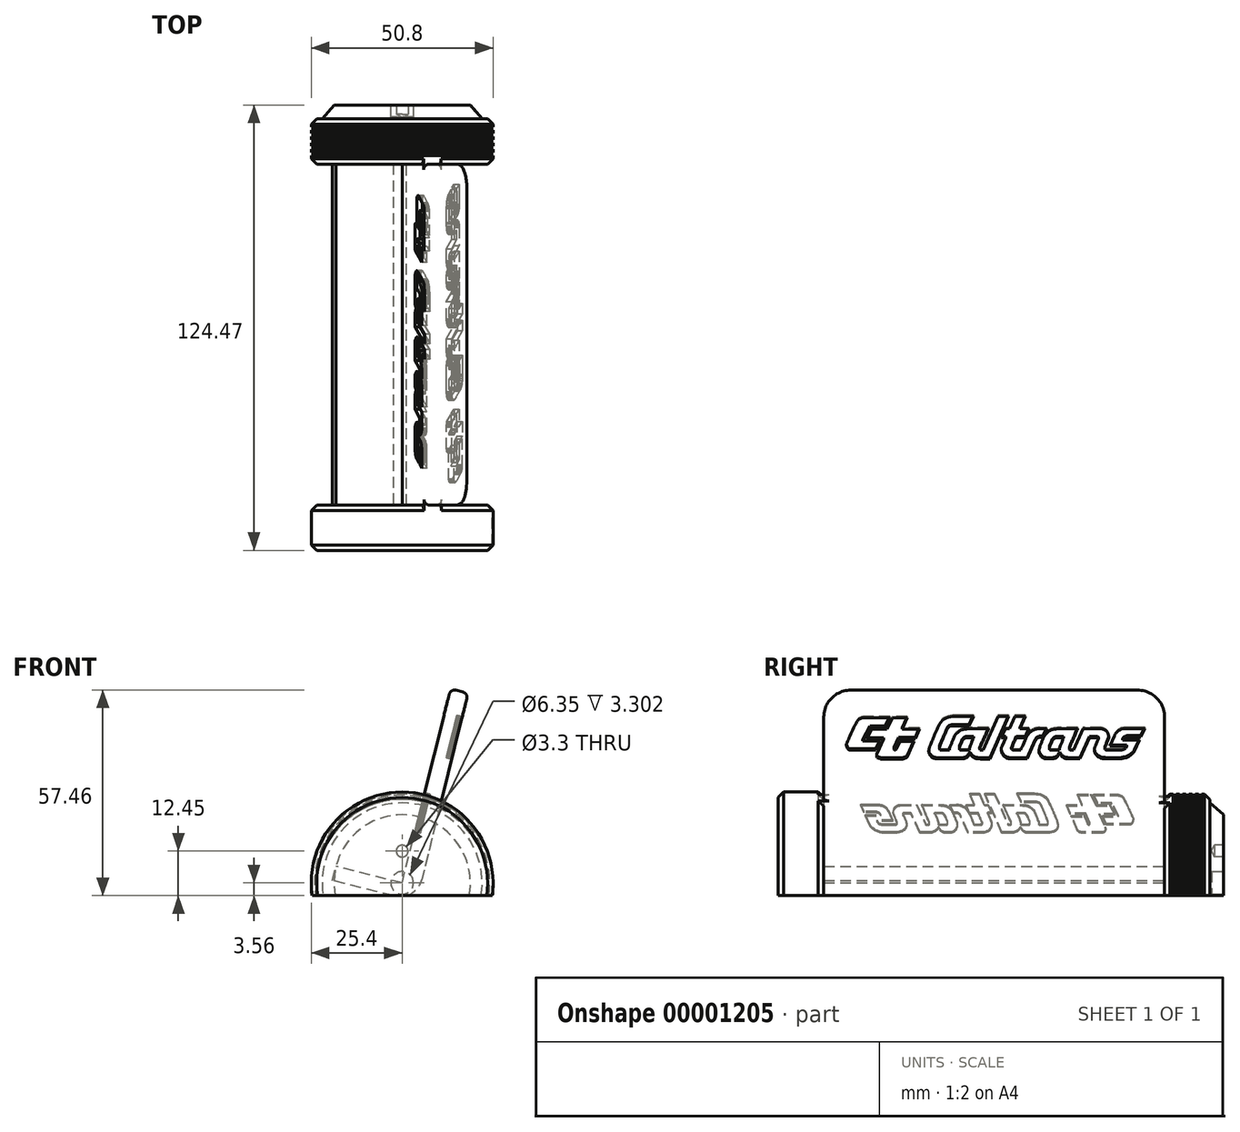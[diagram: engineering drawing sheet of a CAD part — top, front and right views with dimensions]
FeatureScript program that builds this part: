
annotation { "Feature Type Name" : "Feature", "Feature Type Description" : "" }
export const myFeature = defineFeature(function(context is Context, id is Id, definition is map)
    precondition{}
    {
        {
            var Q0;
            Q0=qCreatedBy(makeId("Front.planeOp"),FACE);
            var sketch = newSketch(context, id + "F0", { "sketchPlane" : qUnion([Q0])});
            skLineSegment(sketch, "E0", {"start": v(0, 0) * mm, "end": v(13.52, 54.22) * mm});
            skLineSegment(sketch, "E1", {"start": v(0, 0) * mm, "end": v(-18.48, 4.6) * mm});
            skLineSegment(sketch, "E2", {"start": v(13.52, 54.22) * mm, "end": v(18.45, 53) * mm});
            skLineSegment(sketch, "E3", {"start": v(18.45, 53) * mm, "end": v(3.95, -5.17) * mm});
            skLineSegment(sketch, "E4", {"start": v(3.95, -5.17) * mm, "end": v(-19.47, 0.67) * mm});
            skLineSegment(sketch, "E5", {"start": v(-19.47, 0.67) * mm, "end": v(-18.48, 4.6) * mm});
            skSolve(sketch);
        }
        {
            var Q0;
            Q0 = qSketchRegion(id + "F0", true);
            extrude(context, id + "F1", {"entities" : qUnion([Q0]), "depth" : 95.25 * mm, "offsetDistance" : 25.4 * mm, "symmetric" : true});
        }
        {
            var Q0;
            Q0=makeQuery(id+"F1.opExtrude","CAP_FACE",FACE,{"disambiguationData":[OSD([sQuery(id+"F0.wireOp",EDGE,"E0"),sQuery(id+"F0.wireOp",EDGE,"E1"),sQuery(id+"F0.wireOp",EDGE,"E2"),sQuery(id+"F0.wireOp",EDGE,"E3"),sQuery(id+"F0.wireOp",EDGE,"E4"),sQuery(id+"F0.wireOp",EDGE,"E5")])],"isStart":false});
            var sketch = newSketch(context, id + "F2", { "sketchPlane" : qUnion([Q0])});
            skCircle(sketch, "E6", {"center": v(0, 0) * mm, "radius": 25.4 * mm});
            skSolve(sketch);
        }
        {
            var Q0;
            Q0 = qSketchRegion(id + "F2", true);
            extrude(context, id + "F3", {"entities" : qUnion([Q0]), "operationType" : NewBodyOperationType.ADD, "depth" : 12.7 * mm, "offsetDistance" : 25.4 * mm});
        }
        {
            var Q0;
            Q0=makeQuery(id+"F1.opExtrude","SWEPT_FACE",FACE,{"disambiguationData":[OSD([sQuery(id+"F0.wireOp",EDGE,"E0")])]});
            var sketch = newSketch(context, id + "F4", { "sketchPlane" : qUnion([Q0])});
            skLineSegment(sketch, "E7", {"start": v(-27.75, 25.53) * mm, "end": v(-34.38, 25.53) * mm});
            skLineSegment(sketch, "E8", {"start": v(-34.38, 25.53) * mm, "end": v(-34.43, 25.53) * mm});
            skLineSegment(sketch, "E9", {"start": v(-34.43, 25.53) * mm, "end": v(-34.56, 25.52) * mm});
            skLineSegment(sketch, "E10", {"start": v(-34.56, 25.52) * mm, "end": v(-34.77, 25.48) * mm});
            skLineSegment(sketch, "E11", {"start": v(-34.77, 25.48) * mm, "end": v(-35.02, 25.41) * mm});
            skLineSegment(sketch, "E12", {"start": v(-35.02, 25.41) * mm, "end": v(-35.3, 25.3) * mm});
            skLineSegment(sketch, "E13", {"start": v(-35.3, 25.3) * mm, "end": v(-35.58, 25.15) * mm});
            skLineSegment(sketch, "E14", {"start": v(-35.58, 25.15) * mm, "end": v(-35.85, 24.93) * mm});
            skLineSegment(sketch, "E15", {"start": v(-35.85, 24.93) * mm, "end": v(-36.04, 24.72) * mm});
            skLineSegment(sketch, "E16", {"start": v(-36.04, 24.72) * mm, "end": v(-36.1, 24.64) * mm});
            skLineSegment(sketch, "E17", {"start": v(-36.1, 24.64) * mm, "end": v(-36.12, 24.6) * mm});
            skLineSegment(sketch, "E18", {"start": v(-36.12, 24.6) * mm, "end": v(-36.22, 24.43) * mm});
            skLineSegment(sketch, "E19", {"start": v(-36.22, 24.43) * mm, "end": v(-36.38, 24.14) * mm});
            skLineSegment(sketch, "E20", {"start": v(-36.38, 24.14) * mm, "end": v(-36.56, 23.77) * mm});
            skLineSegment(sketch, "E21", {"start": v(-36.56, 23.77) * mm, "end": v(-36.77, 23.34) * mm});
            skLineSegment(sketch, "E22", {"start": v(-36.77, 23.34) * mm, "end": v(-37, 22.86) * mm});
            skLineSegment(sketch, "E23", {"start": v(-37, 22.86) * mm, "end": v(-37.23, 22.36) * mm});
            skLineSegment(sketch, "E24", {"start": v(-37.23, 22.36) * mm, "end": v(-37.46, 21.84) * mm});
            skLineSegment(sketch, "E25", {"start": v(-37.46, 21.84) * mm, "end": v(-37.7, 21.3) * mm});
            skLineSegment(sketch, "E26", {"start": v(-37.7, 21.3) * mm, "end": v(-37.93, 20.8) * mm});
            skLineSegment(sketch, "E27", {"start": v(-37.93, 20.8) * mm, "end": v(-38.15, 20.3) * mm});
            skLineSegment(sketch, "E28", {"start": v(-38.15, 20.3) * mm, "end": v(-38.35, 19.85) * mm});
            skLineSegment(sketch, "E29", {"start": v(-38.35, 19.85) * mm, "end": v(-38.52, 19.44) * mm});
            skLineSegment(sketch, "E30", {"start": v(-38.52, 19.44) * mm, "end": v(-38.67, 19.1) * mm});
            skLineSegment(sketch, "E31", {"start": v(-38.67, 19.1) * mm, "end": v(-38.78, 18.85) * mm});
            skLineSegment(sketch, "E32", {"start": v(-38.78, 18.85) * mm, "end": v(-38.85, 18.68) * mm});
            skLineSegment(sketch, "E33", {"start": v(-38.85, 18.68) * mm, "end": v(-38.88, 18.62) * mm});
            skLineSegment(sketch, "E34", {"start": v(-38.88, 18.62) * mm, "end": v(-38.88, 18.57) * mm});
            skLineSegment(sketch, "E35", {"start": v(-38.88, 18.57) * mm, "end": v(-38.88, 18.42) * mm});
            skLineSegment(sketch, "E36", {"start": v(-38.88, 18.42) * mm, "end": v(-38.86, 18.21) * mm});
            skLineSegment(sketch, "E37", {"start": v(-38.86, 18.21) * mm, "end": v(-38.81, 17.96) * mm});
            skLineSegment(sketch, "E38", {"start": v(-38.81, 17.96) * mm, "end": v(-38.71, 17.7) * mm});
            skLineSegment(sketch, "E39", {"start": v(-38.71, 17.7) * mm, "end": v(-38.55, 17.43) * mm});
            skLineSegment(sketch, "E40", {"start": v(-38.55, 17.43) * mm, "end": v(-38.31, 17.2) * mm});
            skLineSegment(sketch, "E41", {"start": v(-38.31, 17.2) * mm, "end": v(-38.07, 17.07) * mm});
            skLineSegment(sketch, "E42", {"start": v(-38.07, 17.07) * mm, "end": v(-37.98, 17.05) * mm});
            skLineSegment(sketch, "E43", {"start": v(-37.98, 17.05) * mm, "end": v(-31.35, 17.05) * mm});
            skLineSegment(sketch, "E44", {"start": v(-31.35, 17.05) * mm, "end": v(-30.26, 19.42) * mm});
            skLineSegment(sketch, "E45", {"start": v(-30.26, 19.42) * mm, "end": v(-34.7, 19.42) * mm});
            skLineSegment(sketch, "E46", {"start": v(-34.7, 19.42) * mm, "end": v(-32.84, 23.08) * mm});
            skLineSegment(sketch, "E47", {"start": v(-32.84, 23.08) * mm, "end": v(-28.97, 23.08) * mm});
            skLineSegment(sketch, "E48", {"start": v(-28.97, 23.08) * mm, "end": v(-27.75, 25.53) * mm});
            skLineSegment(sketch, "E49", {"start": v(-28.52, 22.53) * mm, "end": v(-32.34, 22.53) * mm});
            skLineSegment(sketch, "E50", {"start": v(-32.34, 22.53) * mm, "end": v(-33.7, 19.9) * mm});
            skLineSegment(sketch, "E51", {"start": v(-33.7, 19.9) * mm, "end": v(-29.37, 19.9) * mm});
            skLineSegment(sketch, "E52", {"start": v(-29.37, 19.9) * mm, "end": v(-31.03, 16.2) * mm});
            skLineSegment(sketch, "E53", {"start": v(-31.03, 16.2) * mm, "end": v(-31.05, 16.15) * mm});
            skLineSegment(sketch, "E54", {"start": v(-31.05, 16.15) * mm, "end": v(-31.1, 16) * mm});
            skLineSegment(sketch, "E55", {"start": v(-31.1, 16) * mm, "end": v(-31.15, 15.8) * mm});
            skLineSegment(sketch, "E56", {"start": v(-31.15, 15.8) * mm, "end": v(-31.16, 15.55) * mm});
            skLineSegment(sketch, "E57", {"start": v(-31.16, 15.55) * mm, "end": v(-31.1, 15.3) * mm});
            skLineSegment(sketch, "E58", {"start": v(-31.1, 15.3) * mm, "end": v(-30.94, 15.05) * mm});
            skLineSegment(sketch, "E59", {"start": v(-30.94, 15.05) * mm, "end": v(-30.65, 14.84) * mm});
            skLineSegment(sketch, "E60", {"start": v(-30.65, 14.84) * mm, "end": v(-30.32, 14.72) * mm});
            skLineSegment(sketch, "E61", {"start": v(-30.32, 14.72) * mm, "end": v(-30.2, 14.7) * mm});
            skLineSegment(sketch, "E62", {"start": v(-30.2, 14.7) * mm, "end": v(-24.7, 14.7) * mm});
            skLineSegment(sketch, "E63", {"start": v(-24.7, 14.7) * mm, "end": v(-24.68, 14.7) * mm});
            skLineSegment(sketch, "E64", {"start": v(-24.68, 14.7) * mm, "end": v(-24.6, 14.7) * mm});
            skLineSegment(sketch, "E65", {"start": v(-24.6, 14.7) * mm, "end": v(-24.47, 14.7) * mm});
            skLineSegment(sketch, "E66", {"start": v(-24.47, 14.7) * mm, "end": v(-24.3, 14.73) * mm});
            skLineSegment(sketch, "E67", {"start": v(-24.3, 14.73) * mm, "end": v(-24.1, 14.79) * mm});
            skLineSegment(sketch, "E68", {"start": v(-24.1, 14.79) * mm, "end": v(-23.87, 14.88) * mm});
            skLineSegment(sketch, "E69", {"start": v(-23.87, 14.88) * mm, "end": v(-23.62, 15.02) * mm});
            skLineSegment(sketch, "E70", {"start": v(-23.62, 15.02) * mm, "end": v(-23.42, 15.17) * mm});
            skLineSegment(sketch, "E71", {"start": v(-23.42, 15.17) * mm, "end": v(-23.36, 15.23) * mm});
            skLineSegment(sketch, "E72", {"start": v(-23.36, 15.23) * mm, "end": v(-21.58, 19.36) * mm});
            skLineSegment(sketch, "E73", {"start": v(-21.58, 19.36) * mm, "end": v(-25.2, 19.36) * mm});
            skLineSegment(sketch, "E74", {"start": v(-25.2, 19.36) * mm, "end": v(-26.07, 17.34) * mm});
            skLineSegment(sketch, "E75", {"start": v(-26.07, 17.34) * mm, "end": v(-26.1, 17.3) * mm});
            skLineSegment(sketch, "E76", {"start": v(-26.1, 17.3) * mm, "end": v(-26.16, 17.24) * mm});
            skLineSegment(sketch, "E77", {"start": v(-26.16, 17.24) * mm, "end": v(-26.25, 17.16) * mm});
            skLineSegment(sketch, "E78", {"start": v(-26.25, 17.16) * mm, "end": v(-26.35, 17.09) * mm});
            skLineSegment(sketch, "E79", {"start": v(-26.35, 17.09) * mm, "end": v(-26.46, 17.05) * mm});
            skLineSegment(sketch, "E80", {"start": v(-26.46, 17.05) * mm, "end": v(-26.57, 17.06) * mm});
            skLineSegment(sketch, "E81", {"start": v(-26.57, 17.06) * mm, "end": v(-26.66, 17.16) * mm});
            skLineSegment(sketch, "E82", {"start": v(-26.66, 17.16) * mm, "end": v(-26.7, 17.3) * mm});
            skLineSegment(sketch, "E83", {"start": v(-26.7, 17.3) * mm, "end": v(-26.72, 17.36) * mm});
            skLineSegment(sketch, "E84", {"start": v(-26.72, 17.36) * mm, "end": v(-25.56, 20.05) * mm});
            skLineSegment(sketch, "E85", {"start": v(-25.56, 20.05) * mm, "end": v(-21.28, 20.05) * mm});
            skLineSegment(sketch, "E86", {"start": v(-21.28, 20.05) * mm, "end": v(-20.23, 22.53) * mm});
            skLineSegment(sketch, "E87", {"start": v(-20.23, 22.53) * mm, "end": v(-24.56, 22.53) * mm});
            skLineSegment(sketch, "E88", {"start": v(-24.56, 22.53) * mm, "end": v(-23.35, 25.55) * mm});
            skLineSegment(sketch, "E89", {"start": v(-23.35, 25.55) * mm, "end": v(-27.05, 25.55) * mm});
            skLineSegment(sketch, "E90", {"start": v(-27.05, 25.55) * mm, "end": v(-28.52, 22.53) * mm});
            skLineSegment(sketch, "E91", {"start": v(14.7, 20.26) * mm, "end": v(16.64, 20.25) * mm});
            skLineSegment(sketch, "E92", {"start": v(16.64, 20.25) * mm, "end": v(16.59, 20.13) * mm});
            skLineSegment(sketch, "E93", {"start": v(16.59, 20.13) * mm, "end": v(16.42, 19.76) * mm});
            skLineSegment(sketch, "E94", {"start": v(16.42, 19.76) * mm, "end": v(16.19, 19.25) * mm});
            skLineSegment(sketch, "E95", {"start": v(16.19, 19.25) * mm, "end": v(15.97, 18.75) * mm});
            skLineSegment(sketch, "E96", {"start": v(15.97, 18.75) * mm, "end": v(15.77, 18.26) * mm});
            skLineSegment(sketch, "E97", {"start": v(15.77, 18.26) * mm, "end": v(15.62, 17.83) * mm});
            skLineSegment(sketch, "E98", {"start": v(15.62, 17.83) * mm, "end": v(15.51, 17.45) * mm});
            skLineSegment(sketch, "E99", {"start": v(15.51, 17.45) * mm, "end": v(15.48, 17.17) * mm});
            skLineSegment(sketch, "E100", {"start": v(15.48, 17.17) * mm, "end": v(15.51, 17.02) * mm});
            skLineSegment(sketch, "E101", {"start": v(15.51, 17.02) * mm, "end": v(15.54, 16.99) * mm});
            skLineSegment(sketch, "E102", {"start": v(15.54, 16.99) * mm, "end": v(13.29, 16.99) * mm});
            skLineSegment(sketch, "E103", {"start": v(13.29, 16.99) * mm, "end": v(13.27, 16.99) * mm});
            skLineSegment(sketch, "E104", {"start": v(13.27, 16.99) * mm, "end": v(13.2, 17.01) * mm});
            skLineSegment(sketch, "E105", {"start": v(13.2, 17.01) * mm, "end": v(13.13, 17.06) * mm});
            skLineSegment(sketch, "E106", {"start": v(13.13, 17.06) * mm, "end": v(13.08, 17.13) * mm});
            skLineSegment(sketch, "E107", {"start": v(13.08, 17.13) * mm, "end": v(13.04, 17.2) * mm});
            skLineSegment(sketch, "E108", {"start": v(13.04, 17.2) * mm, "end": v(13.01, 17.29) * mm});
            skLineSegment(sketch, "E109", {"start": v(13.01, 17.29) * mm, "end": v(13, 17.35) * mm});
            skLineSegment(sketch, "E110", {"start": v(13, 17.35) * mm, "end": v(13, 17.4) * mm});
            skLineSegment(sketch, "E111", {"start": v(13, 17.4) * mm, "end": v(13.01, 17.42) * mm});
            skLineSegment(sketch, "E112", {"start": v(13.01, 17.42) * mm, "end": v(13.02, 17.42) * mm});
            skLineSegment(sketch, "E113", {"start": v(13.02, 17.42) * mm, "end": v(13.02, 17.51) * mm});
            skLineSegment(sketch, "E114", {"start": v(13.02, 17.51) * mm, "end": v(13.05, 17.78) * mm});
            skLineSegment(sketch, "E115", {"start": v(13.05, 17.78) * mm, "end": v(13.13, 18.09) * mm});
            skLineSegment(sketch, "E116", {"start": v(13.13, 18.09) * mm, "end": v(13.24, 18.38) * mm});
            skLineSegment(sketch, "E117", {"start": v(13.24, 18.38) * mm, "end": v(13.35, 18.63) * mm});
            skLineSegment(sketch, "E118", {"start": v(13.35, 18.63) * mm, "end": v(13.38, 18.7) * mm});
            skLineSegment(sketch, "E119", {"start": v(13.38, 18.7) * mm, "end": v(13.42, 18.8) * mm});
            skLineSegment(sketch, "E120", {"start": v(13.42, 18.8) * mm, "end": v(13.56, 19.18) * mm});
            skLineSegment(sketch, "E121", {"start": v(13.56, 19.18) * mm, "end": v(13.74, 19.54) * mm});
            skLineSegment(sketch, "E122", {"start": v(13.74, 19.54) * mm, "end": v(13.8, 19.62) * mm});
            skLineSegment(sketch, "E123", {"start": v(13.8, 19.62) * mm, "end": v(13.84, 19.68) * mm});
            skLineSegment(sketch, "E124", {"start": v(13.84, 19.68) * mm, "end": v(13.98, 19.86) * mm});
            skLineSegment(sketch, "E125", {"start": v(13.98, 19.86) * mm, "end": v(14.17, 20.06) * mm});
            skLineSegment(sketch, "E126", {"start": v(14.17, 20.06) * mm, "end": v(14.4, 20.2) * mm});
            skLineSegment(sketch, "E127", {"start": v(14.4, 20.2) * mm, "end": v(14.62, 20.26) * mm});
            skLineSegment(sketch, "E128", {"start": v(14.62, 20.26) * mm, "end": v(14.7, 20.26) * mm});
            skLineSegment(sketch, "E129", {"start": v(-8.28, 20.26) * mm, "end": v(-6.34, 20.25) * mm});
            skLineSegment(sketch, "E130", {"start": v(-6.34, 20.25) * mm, "end": v(-6.4, 20.13) * mm});
            skLineSegment(sketch, "E131", {"start": v(-6.4, 20.13) * mm, "end": v(-6.56, 19.76) * mm});
            skLineSegment(sketch, "E132", {"start": v(-6.56, 19.76) * mm, "end": v(-6.79, 19.25) * mm});
            skLineSegment(sketch, "E133", {"start": v(-6.79, 19.25) * mm, "end": v(-7.01, 18.75) * mm});
            skLineSegment(sketch, "E134", {"start": v(-7.01, 18.75) * mm, "end": v(-7.2, 18.26) * mm});
            skLineSegment(sketch, "E135", {"start": v(-7.2, 18.26) * mm, "end": v(-7.36, 17.83) * mm});
            skLineSegment(sketch, "E136", {"start": v(-7.36, 17.83) * mm, "end": v(-7.46, 17.45) * mm});
            skLineSegment(sketch, "E137", {"start": v(-7.46, 17.45) * mm, "end": v(-7.5, 17.17) * mm});
            skLineSegment(sketch, "E138", {"start": v(-7.5, 17.17) * mm, "end": v(-7.47, 17.02) * mm});
            skLineSegment(sketch, "E139", {"start": v(-7.47, 17.02) * mm, "end": v(-7.44, 16.99) * mm});
            skLineSegment(sketch, "E140", {"start": v(-7.44, 16.99) * mm, "end": v(-9.7, 16.99) * mm});
            skLineSegment(sketch, "E141", {"start": v(-9.7, 16.99) * mm, "end": v(-9.71, 16.99) * mm});
            skLineSegment(sketch, "E142", {"start": v(-9.71, 16.99) * mm, "end": v(-9.78, 17.01) * mm});
            skLineSegment(sketch, "E143", {"start": v(-9.78, 17.01) * mm, "end": v(-9.85, 17.06) * mm});
            skLineSegment(sketch, "E144", {"start": v(-9.85, 17.06) * mm, "end": v(-9.9, 17.13) * mm});
            skLineSegment(sketch, "E145", {"start": v(-9.9, 17.13) * mm, "end": v(-9.94, 17.2) * mm});
            skLineSegment(sketch, "E146", {"start": v(-9.94, 17.2) * mm, "end": v(-9.97, 17.29) * mm});
            skLineSegment(sketch, "E147", {"start": v(-9.97, 17.29) * mm, "end": v(-9.98, 17.35) * mm});
            skLineSegment(sketch, "E148", {"start": v(-9.98, 17.35) * mm, "end": v(-9.98, 17.4) * mm});
            skLineSegment(sketch, "E149", {"start": v(-9.98, 17.4) * mm, "end": v(-9.97, 17.42) * mm});
            skLineSegment(sketch, "E150", {"start": v(-9.97, 17.42) * mm, "end": v(-9.96, 17.42) * mm});
            skLineSegment(sketch, "E151", {"start": v(-9.96, 17.42) * mm, "end": v(-9.96, 17.51) * mm});
            skLineSegment(sketch, "E152", {"start": v(-9.96, 17.51) * mm, "end": v(-9.93, 17.78) * mm});
            skLineSegment(sketch, "E153", {"start": v(-9.93, 17.78) * mm, "end": v(-9.85, 18.09) * mm});
            skLineSegment(sketch, "E154", {"start": v(-9.85, 18.09) * mm, "end": v(-9.74, 18.38) * mm});
            skLineSegment(sketch, "E155", {"start": v(-9.74, 18.38) * mm, "end": v(-9.63, 18.63) * mm});
            skLineSegment(sketch, "E156", {"start": v(-9.63, 18.63) * mm, "end": v(-9.6, 18.7) * mm});
            skLineSegment(sketch, "E157", {"start": v(-9.6, 18.7) * mm, "end": v(-9.57, 18.8) * mm});
            skLineSegment(sketch, "E158", {"start": v(-9.57, 18.8) * mm, "end": v(-9.42, 19.18) * mm});
            skLineSegment(sketch, "E159", {"start": v(-9.42, 19.18) * mm, "end": v(-9.24, 19.54) * mm});
            skLineSegment(sketch, "E160", {"start": v(-9.24, 19.54) * mm, "end": v(-9.19, 19.62) * mm});
            skLineSegment(sketch, "E161", {"start": v(-9.19, 19.62) * mm, "end": v(-9.14, 19.68) * mm});
            skLineSegment(sketch, "E162", {"start": v(-9.14, 19.68) * mm, "end": v(-9, 19.86) * mm});
            skLineSegment(sketch, "E163", {"start": v(-9, 19.86) * mm, "end": v(-8.8, 20.06) * mm});
            skLineSegment(sketch, "E164", {"start": v(-8.8, 20.06) * mm, "end": v(-8.57, 20.2) * mm});
            skLineSegment(sketch, "E165", {"start": v(-8.57, 20.2) * mm, "end": v(-8.36, 20.26) * mm});
            skLineSegment(sketch, "E166", {"start": v(-8.36, 20.26) * mm, "end": v(-8.28, 20.26) * mm});
            skLineSegment(sketch, "E167", {"start": v(30.97, 14.72) * mm, "end": v(31.09, 14.72) * mm});
            skLineSegment(sketch, "E168", {"start": v(31.09, 14.72) * mm, "end": v(31.45, 14.75) * mm});
            skLineSegment(sketch, "E169", {"start": v(31.45, 14.75) * mm, "end": v(31.97, 14.85) * mm});
            skLineSegment(sketch, "E170", {"start": v(31.97, 14.85) * mm, "end": v(32.57, 15.05) * mm});
            skLineSegment(sketch, "E171", {"start": v(32.57, 15.05) * mm, "end": v(33.1, 15.29) * mm});
            skLineSegment(sketch, "E172", {"start": v(33.1, 15.29) * mm, "end": v(33.27, 15.38) * mm});
            skLineSegment(sketch, "E173", {"start": v(33.27, 15.38) * mm, "end": v(33.37, 15.43) * mm});
            skLineSegment(sketch, "E174", {"start": v(33.37, 15.43) * mm, "end": v(33.63, 15.6) * mm});
            skLineSegment(sketch, "E175", {"start": v(33.63, 15.6) * mm, "end": v(33.94, 15.83) * mm});
            skLineSegment(sketch, "E176", {"start": v(33.94, 15.83) * mm, "end": v(34.19, 16.07) * mm});
            skLineSegment(sketch, "E177", {"start": v(34.19, 16.07) * mm, "end": v(34.4, 16.3) * mm});
            skLineSegment(sketch, "E178", {"start": v(34.4, 16.3) * mm, "end": v(34.55, 16.51) * mm});
            skLineSegment(sketch, "E179", {"start": v(34.55, 16.51) * mm, "end": v(34.65, 16.68) * mm});
            skLineSegment(sketch, "E180", {"start": v(34.65, 16.68) * mm, "end": v(34.72, 16.8) * mm});
            skLineSegment(sketch, "E181", {"start": v(34.72, 16.8) * mm, "end": v(34.74, 16.83) * mm});
            skLineSegment(sketch, "E182", {"start": v(34.74, 16.83) * mm, "end": v(36, 19.68) * mm});
            skLineSegment(sketch, "E183", {"start": v(36, 19.68) * mm, "end": v(31.64, 19.68) * mm});
            skLineSegment(sketch, "E184", {"start": v(31.64, 19.68) * mm, "end": v(31.63, 19.67) * mm});
            skLineSegment(sketch, "E185", {"start": v(31.63, 19.67) * mm, "end": v(31.61, 19.63) * mm});
            skLineSegment(sketch, "E186", {"start": v(31.61, 19.63) * mm, "end": v(31.6, 19.6) * mm});
            skLineSegment(sketch, "E187", {"start": v(31.6, 19.6) * mm, "end": v(31.58, 19.57) * mm});
            skLineSegment(sketch, "E188", {"start": v(31.58, 19.57) * mm, "end": v(31.58, 19.57) * mm});
            skLineSegment(sketch, "E189", {"start": v(31.58, 19.57) * mm, "end": v(31.6, 19.61) * mm});
            skLineSegment(sketch, "E190", {"start": v(31.6, 19.61) * mm, "end": v(31.66, 19.7) * mm});
            skLineSegment(sketch, "E191", {"start": v(31.66, 19.7) * mm, "end": v(31.73, 19.82) * mm});
            skLineSegment(sketch, "E192", {"start": v(31.73, 19.82) * mm, "end": v(31.75, 19.86) * mm});
            skLineSegment(sketch, "E193", {"start": v(31.75, 19.86) * mm, "end": v(31.78, 19.91) * mm});
            skLineSegment(sketch, "E194", {"start": v(31.78, 19.91) * mm, "end": v(31.89, 20.05) * mm});
            skLineSegment(sketch, "E195", {"start": v(31.89, 20.05) * mm, "end": v(32.05, 20.2) * mm});
            skLineSegment(sketch, "E196", {"start": v(32.05, 20.2) * mm, "end": v(32.22, 20.31) * mm});
            skLineSegment(sketch, "E197", {"start": v(32.22, 20.31) * mm, "end": v(32.4, 20.4) * mm});
            skLineSegment(sketch, "E198", {"start": v(32.4, 20.4) * mm, "end": v(32.56, 20.46) * mm});
            skLineSegment(sketch, "E199", {"start": v(32.56, 20.46) * mm, "end": v(32.69, 20.5) * mm});
            skLineSegment(sketch, "E200", {"start": v(32.69, 20.5) * mm, "end": v(32.78, 20.52) * mm});
            skLineSegment(sketch, "E201", {"start": v(32.78, 20.52) * mm, "end": v(32.8, 20.53) * mm});
            skLineSegment(sketch, "E202", {"start": v(32.8, 20.53) * mm, "end": v(36.37, 20.53) * mm});
            skLineSegment(sketch, "E203", {"start": v(36.37, 20.53) * mm, "end": v(37.32, 22.64) * mm});
            skLineSegment(sketch, "E204", {"start": v(37.32, 22.64) * mm, "end": v(37.27, 22.64) * mm});
            skLineSegment(sketch, "E205", {"start": v(37.27, 22.64) * mm, "end": v(37.11, 22.64) * mm});
            skLineSegment(sketch, "E206", {"start": v(37.11, 22.64) * mm, "end": v(36.88, 22.64) * mm});
            skLineSegment(sketch, "E207", {"start": v(36.88, 22.64) * mm, "end": v(36.57, 22.64) * mm});
            skLineSegment(sketch, "E208", {"start": v(36.57, 22.64) * mm, "end": v(36.2, 22.64) * mm});
            skLineSegment(sketch, "E209", {"start": v(36.2, 22.64) * mm, "end": v(35.8, 22.64) * mm});
            skLineSegment(sketch, "E210", {"start": v(35.8, 22.64) * mm, "end": v(35.36, 22.64) * mm});
            skLineSegment(sketch, "E211", {"start": v(35.36, 22.64) * mm, "end": v(34.9, 22.64) * mm});
            skLineSegment(sketch, "E212", {"start": v(34.9, 22.64) * mm, "end": v(34.44, 22.64) * mm});
            skLineSegment(sketch, "E213", {"start": v(34.44, 22.64) * mm, "end": v(33.98, 22.64) * mm});
            skLineSegment(sketch, "E214", {"start": v(33.98, 22.64) * mm, "end": v(33.55, 22.64) * mm});
            skLineSegment(sketch, "E215", {"start": v(33.55, 22.64) * mm, "end": v(33.15, 22.64) * mm});
            skLineSegment(sketch, "E216", {"start": v(33.15, 22.64) * mm, "end": v(32.8, 22.64) * mm});
            skLineSegment(sketch, "E217", {"start": v(32.8, 22.64) * mm, "end": v(32.5, 22.64) * mm});
            skLineSegment(sketch, "E218", {"start": v(32.5, 22.64) * mm, "end": v(32.3, 22.64) * mm});
            skLineSegment(sketch, "E219", {"start": v(32.3, 22.64) * mm, "end": v(32.2, 22.64) * mm});
            skLineSegment(sketch, "E220", {"start": v(32.2, 22.64) * mm, "end": v(32.17, 22.64) * mm});
            skLineSegment(sketch, "E221", {"start": v(32.17, 22.64) * mm, "end": v(32.07, 22.65) * mm});
            skLineSegment(sketch, "E222", {"start": v(32.07, 22.65) * mm, "end": v(31.8, 22.61) * mm});
            skLineSegment(sketch, "E223", {"start": v(31.8, 22.61) * mm, "end": v(31.36, 22.5) * mm});
            skLineSegment(sketch, "E224", {"start": v(31.36, 22.5) * mm, "end": v(30.94, 22.34) * mm});
            skLineSegment(sketch, "E225", {"start": v(30.94, 22.34) * mm, "end": v(30.68, 22.2) * mm});
            skLineSegment(sketch, "E226", {"start": v(30.68, 22.2) * mm, "end": v(30.6, 22.13) * mm});
            skLineSegment(sketch, "E227", {"start": v(30.6, 22.13) * mm, "end": v(30.53, 22.06) * mm});
            skLineSegment(sketch, "E228", {"start": v(30.53, 22.06) * mm, "end": v(30.31, 21.86) * mm});
            skLineSegment(sketch, "E229", {"start": v(30.31, 21.86) * mm, "end": v(30.08, 21.6) * mm});
            skLineSegment(sketch, "E230", {"start": v(30.08, 21.6) * mm, "end": v(29.9, 21.38) * mm});
            skLineSegment(sketch, "E231", {"start": v(29.9, 21.38) * mm, "end": v(29.76, 21.18) * mm});
            skLineSegment(sketch, "E232", {"start": v(29.76, 21.18) * mm, "end": v(29.67, 21.03) * mm});
            skLineSegment(sketch, "E233", {"start": v(29.67, 21.03) * mm, "end": v(29.6, 20.9) * mm});
            skLineSegment(sketch, "E234", {"start": v(29.6, 20.9) * mm, "end": v(29.58, 20.83) * mm});
            skLineSegment(sketch, "E235", {"start": v(29.58, 20.83) * mm, "end": v(29.57, 20.8) * mm});
            skLineSegment(sketch, "E236", {"start": v(29.57, 20.8) * mm, "end": v(28.42, 18.07) * mm});
            skLineSegment(sketch, "E237", {"start": v(28.42, 18.07) * mm, "end": v(32.74, 18.07) * mm});
            skLineSegment(sketch, "E238", {"start": v(32.74, 18.07) * mm, "end": v(32.73, 18.04) * mm});
            skLineSegment(sketch, "E239", {"start": v(32.73, 18.04) * mm, "end": v(32.71, 17.97) * mm});
            skLineSegment(sketch, "E240", {"start": v(32.71, 17.97) * mm, "end": v(32.69, 17.9) * mm});
            skLineSegment(sketch, "E241", {"start": v(32.69, 17.9) * mm, "end": v(32.67, 17.85) * mm});
            skLineSegment(sketch, "E242", {"start": v(32.67, 17.85) * mm, "end": v(32.67, 17.84) * mm});
            skLineSegment(sketch, "E243", {"start": v(32.67, 17.84) * mm, "end": v(32.63, 17.77) * mm});
            skLineSegment(sketch, "E244", {"start": v(32.63, 17.77) * mm, "end": v(32.49, 17.57) * mm});
            skLineSegment(sketch, "E245", {"start": v(32.49, 17.57) * mm, "end": v(32.26, 17.36) * mm});
            skLineSegment(sketch, "E246", {"start": v(32.26, 17.36) * mm, "end": v(32, 17.22) * mm});
            skLineSegment(sketch, "E247", {"start": v(32, 17.22) * mm, "end": v(31.75, 17.13) * mm});
            skLineSegment(sketch, "E248", {"start": v(31.75, 17.13) * mm, "end": v(31.51, 17.07) * mm});
            skLineSegment(sketch, "E249", {"start": v(31.51, 17.07) * mm, "end": v(31.32, 17.05) * mm});
            skLineSegment(sketch, "E250", {"start": v(31.32, 17.05) * mm, "end": v(31.18, 17.04) * mm});
            skLineSegment(sketch, "E251", {"start": v(31.18, 17.04) * mm, "end": v(31.13, 17.04) * mm});
            skLineSegment(sketch, "E252", {"start": v(31.13, 17.04) * mm, "end": v(31, 17.04) * mm});
            skLineSegment(sketch, "E253", {"start": v(31, 17.04) * mm, "end": v(30.65, 17.03) * mm});
            skLineSegment(sketch, "E254", {"start": v(30.65, 17.03) * mm, "end": v(30.14, 17.03) * mm});
            skLineSegment(sketch, "E255", {"start": v(30.14, 17.03) * mm, "end": v(29.54, 17.03) * mm});
            skLineSegment(sketch, "E256", {"start": v(29.54, 17.03) * mm, "end": v(28.92, 17.03) * mm});
            skLineSegment(sketch, "E257", {"start": v(28.92, 17.03) * mm, "end": v(28.34, 17.03) * mm});
            skLineSegment(sketch, "E258", {"start": v(28.34, 17.03) * mm, "end": v(27.87, 17.03) * mm});
            skLineSegment(sketch, "E259", {"start": v(27.87, 17.03) * mm, "end": v(27.65, 17.03) * mm});
            skLineSegment(sketch, "E260", {"start": v(27.65, 17.03) * mm, "end": v(27.57, 17.04) * mm});
            skLineSegment(sketch, "E261", {"start": v(27.57, 17.04) * mm, "end": v(27.53, 17.04) * mm});
            skLineSegment(sketch, "E262", {"start": v(27.53, 17.04) * mm, "end": v(27.4, 17.07) * mm});
            skLineSegment(sketch, "E263", {"start": v(27.4, 17.07) * mm, "end": v(27.28, 17.13) * mm});
            skLineSegment(sketch, "E264", {"start": v(27.28, 17.13) * mm, "end": v(27.2, 17.22) * mm});
            skLineSegment(sketch, "E265", {"start": v(27.2, 17.22) * mm, "end": v(27.16, 17.33) * mm});
            skLineSegment(sketch, "E266", {"start": v(27.16, 17.33) * mm, "end": v(27.15, 17.46) * mm});
            skLineSegment(sketch, "E267", {"start": v(27.15, 17.46) * mm, "end": v(27.16, 17.59) * mm});
            skLineSegment(sketch, "E268", {"start": v(27.16, 17.59) * mm, "end": v(27.18, 17.72) * mm});
            skLineSegment(sketch, "E269", {"start": v(27.18, 17.72) * mm, "end": v(27.21, 17.81) * mm});
            skLineSegment(sketch, "E270", {"start": v(27.21, 17.81) * mm, "end": v(27.23, 17.84) * mm});
            skLineSegment(sketch, "E271", {"start": v(27.23, 17.84) * mm, "end": v(27.28, 17.99) * mm});
            skLineSegment(sketch, "E272", {"start": v(27.28, 17.99) * mm, "end": v(27.46, 18.4) * mm});
            skLineSegment(sketch, "E273", {"start": v(27.46, 18.4) * mm, "end": v(27.67, 18.91) * mm});
            skLineSegment(sketch, "E274", {"start": v(27.67, 18.91) * mm, "end": v(27.87, 19.39) * mm});
            skLineSegment(sketch, "E275", {"start": v(27.87, 19.39) * mm, "end": v(28.03, 19.76) * mm});
            skLineSegment(sketch, "E276", {"start": v(28.03, 19.76) * mm, "end": v(28.07, 19.89) * mm});
            skLineSegment(sketch, "E277", {"start": v(28.07, 19.89) * mm, "end": v(28.12, 20) * mm});
            skLineSegment(sketch, "E278", {"start": v(28.12, 20) * mm, "end": v(28.19, 20.4) * mm});
            skLineSegment(sketch, "E279", {"start": v(28.19, 20.4) * mm, "end": v(28.14, 20.9) * mm});
            skLineSegment(sketch, "E280", {"start": v(28.14, 20.9) * mm, "end": v(27.94, 21.4) * mm});
            skLineSegment(sketch, "E281", {"start": v(27.94, 21.4) * mm, "end": v(27.7, 21.79) * mm});
            skLineSegment(sketch, "E282", {"start": v(27.7, 21.79) * mm, "end": v(27.61, 21.9) * mm});
            skLineSegment(sketch, "E283", {"start": v(27.61, 21.9) * mm, "end": v(27.57, 21.97) * mm});
            skLineSegment(sketch, "E284", {"start": v(27.57, 21.97) * mm, "end": v(27.4, 22.14) * mm});
            skLineSegment(sketch, "E285", {"start": v(27.4, 22.14) * mm, "end": v(27.18, 22.31) * mm});
            skLineSegment(sketch, "E286", {"start": v(27.18, 22.31) * mm, "end": v(26.95, 22.44) * mm});
            skLineSegment(sketch, "E287", {"start": v(26.95, 22.44) * mm, "end": v(26.72, 22.53) * mm});
            skLineSegment(sketch, "E288", {"start": v(26.72, 22.53) * mm, "end": v(26.52, 22.58) * mm});
            skLineSegment(sketch, "E289", {"start": v(26.52, 22.58) * mm, "end": v(26.36, 22.6) * mm});
            skLineSegment(sketch, "E290", {"start": v(26.36, 22.6) * mm, "end": v(26.25, 22.62) * mm});
            skLineSegment(sketch, "E291", {"start": v(26.25, 22.62) * mm, "end": v(26.21, 22.62) * mm});
            skLineSegment(sketch, "E292", {"start": v(26.21, 22.62) * mm, "end": v(21.62, 22.62) * mm});
            skLineSegment(sketch, "E293", {"start": v(21.62, 22.62) * mm, "end": v(19.11, 17) * mm});
            skLineSegment(sketch, "E294", {"start": v(19.11, 17) * mm, "end": v(19.09, 17) * mm});
            skLineSegment(sketch, "E295", {"start": v(19.09, 17) * mm, "end": v(19, 17) * mm});
            skLineSegment(sketch, "E296", {"start": v(19, 17) * mm, "end": v(18.8, 17) * mm});
            skLineSegment(sketch, "E297", {"start": v(18.8, 17) * mm, "end": v(18.57, 17) * mm});
            skLineSegment(sketch, "E298", {"start": v(18.57, 17) * mm, "end": v(18.5, 17) * mm});
            skLineSegment(sketch, "E299", {"start": v(18.5, 17) * mm, "end": v(18.45, 17) * mm});
            skLineSegment(sketch, "E300", {"start": v(18.45, 17) * mm, "end": v(18.33, 17.02) * mm});
            skLineSegment(sketch, "E301", {"start": v(18.33, 17.02) * mm, "end": v(18.21, 17.08) * mm});
            skLineSegment(sketch, "E302", {"start": v(18.21, 17.08) * mm, "end": v(18.14, 17.17) * mm});
            skLineSegment(sketch, "E303", {"start": v(18.14, 17.17) * mm, "end": v(18.1, 17.28) * mm});
            skLineSegment(sketch, "E304", {"start": v(18.1, 17.28) * mm, "end": v(18.1, 17.4) * mm});
            skLineSegment(sketch, "E305", {"start": v(18.1, 17.4) * mm, "end": v(18.12, 17.54) * mm});
            skLineSegment(sketch, "E306", {"start": v(18.12, 17.54) * mm, "end": v(18.15, 17.67) * mm});
            skLineSegment(sketch, "E307", {"start": v(18.15, 17.67) * mm, "end": v(18.18, 17.77) * mm});
            skLineSegment(sketch, "E308", {"start": v(18.18, 17.77) * mm, "end": v(18.2, 17.8) * mm});
            skLineSegment(sketch, "E309", {"start": v(18.2, 17.8) * mm, "end": v(18.23, 17.89) * mm});
            skLineSegment(sketch, "E310", {"start": v(18.23, 17.89) * mm, "end": v(18.35, 18.16) * mm});
            skLineSegment(sketch, "E311", {"start": v(18.35, 18.16) * mm, "end": v(18.5, 18.54) * mm});
            skLineSegment(sketch, "E312", {"start": v(18.5, 18.54) * mm, "end": v(18.68, 18.94) * mm});
            skLineSegment(sketch, "E313", {"start": v(18.68, 18.94) * mm, "end": v(18.84, 19.34) * mm});
            skLineSegment(sketch, "E314", {"start": v(18.84, 19.34) * mm, "end": v(19.01, 19.75) * mm});
            skLineSegment(sketch, "E315", {"start": v(19.01, 19.75) * mm, "end": v(19.18, 20.15) * mm});
            skLineSegment(sketch, "E316", {"start": v(19.18, 20.15) * mm, "end": v(19.34, 20.54) * mm});
            skLineSegment(sketch, "E317", {"start": v(19.34, 20.54) * mm, "end": v(19.5, 20.91) * mm});
            skLineSegment(sketch, "E318", {"start": v(19.5, 20.91) * mm, "end": v(19.64, 21.26) * mm});
            skLineSegment(sketch, "E319", {"start": v(19.64, 21.26) * mm, "end": v(19.77, 21.59) * mm});
            skLineSegment(sketch, "E320", {"start": v(19.77, 21.59) * mm, "end": v(19.9, 21.88) * mm});
            skLineSegment(sketch, "E321", {"start": v(19.9, 21.88) * mm, "end": v(20, 22.13) * mm});
            skLineSegment(sketch, "E322", {"start": v(20, 22.13) * mm, "end": v(20.08, 22.34) * mm});
            skLineSegment(sketch, "E323", {"start": v(20.08, 22.34) * mm, "end": v(20.14, 22.5) * mm});
            skLineSegment(sketch, "E324", {"start": v(20.14, 22.5) * mm, "end": v(20.18, 22.59) * mm});
            skLineSegment(sketch, "E325", {"start": v(20.18, 22.59) * mm, "end": v(20.2, 22.62) * mm});
            skLineSegment(sketch, "E326", {"start": v(20.2, 22.62) * mm, "end": v(15.12, 22.62) * mm});
            skLineSegment(sketch, "E327", {"start": v(15.12, 22.62) * mm, "end": v(15.06, 22.62) * mm});
            skLineSegment(sketch, "E328", {"start": v(15.06, 22.62) * mm, "end": v(14.9, 22.61) * mm});
            skLineSegment(sketch, "E329", {"start": v(14.9, 22.61) * mm, "end": v(14.69, 22.6) * mm});
            skLineSegment(sketch, "E330", {"start": v(14.69, 22.6) * mm, "end": v(14.42, 22.56) * mm});
            skLineSegment(sketch, "E331", {"start": v(14.42, 22.56) * mm, "end": v(14.13, 22.52) * mm});
            skLineSegment(sketch, "E332", {"start": v(14.13, 22.52) * mm, "end": v(13.83, 22.46) * mm});
            skLineSegment(sketch, "E333", {"start": v(13.83, 22.46) * mm, "end": v(13.57, 22.38) * mm});
            skLineSegment(sketch, "E334", {"start": v(13.57, 22.38) * mm, "end": v(13.4, 22.3) * mm});
            skLineSegment(sketch, "E335", {"start": v(13.4, 22.3) * mm, "end": v(13.35, 22.28) * mm});
            skLineSegment(sketch, "E336", {"start": v(13.35, 22.28) * mm, "end": v(13.3, 22.25) * mm});
            skLineSegment(sketch, "E337", {"start": v(13.3, 22.25) * mm, "end": v(13.14, 22.15) * mm});
            skLineSegment(sketch, "E338", {"start": v(13.14, 22.15) * mm, "end": v(12.92, 22.01) * mm});
            skLineSegment(sketch, "E339", {"start": v(12.92, 22.01) * mm, "end": v(12.68, 21.84) * mm});
            skLineSegment(sketch, "E340", {"start": v(12.68, 21.84) * mm, "end": v(12.42, 21.63) * mm});
            skLineSegment(sketch, "E341", {"start": v(12.42, 21.63) * mm, "end": v(12.17, 21.37) * mm});
            skLineSegment(sketch, "E342", {"start": v(12.17, 21.37) * mm, "end": v(11.92, 21.06) * mm});
            skLineSegment(sketch, "E343", {"start": v(11.92, 21.06) * mm, "end": v(11.68, 20.7) * mm});
            skLineSegment(sketch, "E344", {"start": v(11.68, 20.7) * mm, "end": v(11.51, 20.37) * mm});
            skLineSegment(sketch, "E345", {"start": v(11.51, 20.37) * mm, "end": v(11.46, 20.25) * mm});
            skLineSegment(sketch, "E346", {"start": v(11.46, 20.25) * mm, "end": v(11.42, 20.15) * mm});
            skLineSegment(sketch, "E347", {"start": v(11.42, 20.15) * mm, "end": v(11.29, 19.84) * mm});
            skLineSegment(sketch, "E348", {"start": v(11.29, 19.84) * mm, "end": v(11.16, 19.52) * mm});
            skLineSegment(sketch, "E349", {"start": v(11.16, 19.52) * mm, "end": v(11.06, 19.26) * mm});
            skLineSegment(sketch, "E350", {"start": v(11.06, 19.26) * mm, "end": v(10.99, 19.05) * mm});
            skLineSegment(sketch, "E351", {"start": v(10.99, 19.05) * mm, "end": v(10.91, 18.85) * mm});
            skLineSegment(sketch, "E352", {"start": v(10.91, 18.85) * mm, "end": v(10.82, 18.62) * mm});
            skLineSegment(sketch, "E353", {"start": v(10.82, 18.62) * mm, "end": v(10.7, 18.35) * mm});
            skLineSegment(sketch, "E354", {"start": v(10.7, 18.35) * mm, "end": v(10.6, 18.09) * mm});
            skLineSegment(sketch, "E355", {"start": v(10.6, 18.09) * mm, "end": v(10.55, 18) * mm});
            skLineSegment(sketch, "E356", {"start": v(10.55, 18) * mm, "end": v(10.5, 17.89) * mm});
            skLineSegment(sketch, "E357", {"start": v(10.5, 17.89) * mm, "end": v(10.4, 17.52) * mm});
            skLineSegment(sketch, "E358", {"start": v(10.4, 17.52) * mm, "end": v(10.33, 17) * mm});
            skLineSegment(sketch, "E359", {"start": v(10.33, 17) * mm, "end": v(10.36, 16.47) * mm});
            skLineSegment(sketch, "E360", {"start": v(10.36, 16.47) * mm, "end": v(10.47, 16.09) * mm});
            skLineSegment(sketch, "E361", {"start": v(10.47, 16.09) * mm, "end": v(10.52, 15.97) * mm});
            skLineSegment(sketch, "E362", {"start": v(10.52, 15.97) * mm, "end": v(10.55, 15.91) * mm});
            skLineSegment(sketch, "E363", {"start": v(10.55, 15.91) * mm, "end": v(10.64, 15.74) * mm});
            skLineSegment(sketch, "E364", {"start": v(10.64, 15.74) * mm, "end": v(10.77, 15.5) * mm});
            skLineSegment(sketch, "E365", {"start": v(10.77, 15.5) * mm, "end": v(10.92, 15.3) * mm});
            skLineSegment(sketch, "E366", {"start": v(10.92, 15.3) * mm, "end": v(11.1, 15.11) * mm});
            skLineSegment(sketch, "E367", {"start": v(11.1, 15.11) * mm, "end": v(11.34, 14.95) * mm});
            skLineSegment(sketch, "E368", {"start": v(11.34, 14.95) * mm, "end": v(11.62, 14.83) * mm});
            skLineSegment(sketch, "E369", {"start": v(11.62, 14.83) * mm, "end": v(11.96, 14.75) * mm});
            skLineSegment(sketch, "E370", {"start": v(11.96, 14.75) * mm, "end": v(12.28, 14.72) * mm});
            skLineSegment(sketch, "E371", {"start": v(12.28, 14.72) * mm, "end": v(12.38, 14.72) * mm});
            skLineSegment(sketch, "E372", {"start": v(12.38, 14.72) * mm, "end": v(12.57, 14.72) * mm});
            skLineSegment(sketch, "E373", {"start": v(12.57, 14.72) * mm, "end": v(13.14, 14.72) * mm});
            skLineSegment(sketch, "E374", {"start": v(13.14, 14.72) * mm, "end": v(13.61, 14.72) * mm});
            skLineSegment(sketch, "E375", {"start": v(13.61, 14.72) * mm, "end": v(13.85, 14.72) * mm});
            skLineSegment(sketch, "E376", {"start": v(13.85, 14.72) * mm, "end": v(13.92, 14.72) * mm});
            skLineSegment(sketch, "E377", {"start": v(13.92, 14.72) * mm, "end": v(13.95, 14.72) * mm});
            skLineSegment(sketch, "E378", {"start": v(13.95, 14.72) * mm, "end": v(14.04, 14.74) * mm});
            skLineSegment(sketch, "E379", {"start": v(14.04, 14.74) * mm, "end": v(14.17, 14.78) * mm});
            skLineSegment(sketch, "E380", {"start": v(14.17, 14.78) * mm, "end": v(14.33, 14.83) * mm});
            skLineSegment(sketch, "E381", {"start": v(14.33, 14.83) * mm, "end": v(14.51, 14.91) * mm});
            skLineSegment(sketch, "E382", {"start": v(14.51, 14.91) * mm, "end": v(14.7, 15.02) * mm});
            skLineSegment(sketch, "E383", {"start": v(14.7, 15.02) * mm, "end": v(14.87, 15.16) * mm});
            skLineSegment(sketch, "E384", {"start": v(14.87, 15.16) * mm, "end": v(15, 15.3) * mm});
            skLineSegment(sketch, "E385", {"start": v(15, 15.3) * mm, "end": v(15.03, 15.34) * mm});
            skLineSegment(sketch, "E386", {"start": v(15.03, 15.34) * mm, "end": v(15.09, 15.43) * mm});
            skLineSegment(sketch, "E387", {"start": v(15.09, 15.43) * mm, "end": v(15.28, 15.7) * mm});
            skLineSegment(sketch, "E388", {"start": v(15.28, 15.7) * mm, "end": v(15.46, 15.96) * mm});
            skLineSegment(sketch, "E389", {"start": v(15.46, 15.96) * mm, "end": v(15.58, 16.13) * mm});
            skLineSegment(sketch, "E390", {"start": v(15.58, 16.13) * mm, "end": v(15.62, 16.19) * mm});
            skLineSegment(sketch, "E391", {"start": v(15.62, 16.19) * mm, "end": v(15.63, 16.16) * mm});
            skLineSegment(sketch, "E392", {"start": v(15.63, 16.16) * mm, "end": v(15.67, 16.08) * mm});
            skLineSegment(sketch, "E393", {"start": v(15.67, 16.08) * mm, "end": v(15.73, 15.96) * mm});
            skLineSegment(sketch, "E394", {"start": v(15.73, 15.96) * mm, "end": v(15.81, 15.8) * mm});
            skLineSegment(sketch, "E395", {"start": v(15.81, 15.8) * mm, "end": v(15.93, 15.64) * mm});
            skLineSegment(sketch, "E396", {"start": v(15.93, 15.64) * mm, "end": v(16.08, 15.47) * mm});
            skLineSegment(sketch, "E397", {"start": v(16.08, 15.47) * mm, "end": v(16.26, 15.3) * mm});
            skLineSegment(sketch, "E398", {"start": v(16.26, 15.3) * mm, "end": v(16.42, 15.18) * mm});
            skLineSegment(sketch, "E399", {"start": v(16.42, 15.18) * mm, "end": v(16.48, 15.15) * mm});
            skLineSegment(sketch, "E400", {"start": v(16.48, 15.15) * mm, "end": v(16.58, 15.09) * mm});
            skLineSegment(sketch, "E401", {"start": v(16.58, 15.09) * mm, "end": v(16.88, 14.92) * mm});
            skLineSegment(sketch, "E402", {"start": v(16.88, 14.92) * mm, "end": v(17.2, 14.8) * mm});
            skLineSegment(sketch, "E403", {"start": v(17.2, 14.8) * mm, "end": v(17.5, 14.74) * mm});
            skLineSegment(sketch, "E404", {"start": v(17.5, 14.74) * mm, "end": v(17.75, 14.72) * mm});
            skLineSegment(sketch, "E405", {"start": v(17.75, 14.72) * mm, "end": v(17.83, 14.72) * mm});
            skLineSegment(sketch, "E406", {"start": v(17.83, 14.72) * mm, "end": v(17.9, 14.72) * mm});
            skLineSegment(sketch, "E407", {"start": v(17.9, 14.72) * mm, "end": v(18.1, 14.72) * mm});
            skLineSegment(sketch, "E408", {"start": v(18.1, 14.72) * mm, "end": v(18.5, 14.72) * mm});
            skLineSegment(sketch, "E409", {"start": v(18.5, 14.72) * mm, "end": v(18.98, 14.72) * mm});
            skLineSegment(sketch, "E410", {"start": v(18.98, 14.72) * mm, "end": v(19.5, 14.72) * mm});
            skLineSegment(sketch, "E411", {"start": v(19.5, 14.72) * mm, "end": v(19.98, 14.72) * mm});
            skLineSegment(sketch, "E412", {"start": v(19.98, 14.72) * mm, "end": v(20.4, 14.72) * mm});
            skLineSegment(sketch, "E413", {"start": v(20.4, 14.72) * mm, "end": v(20.68, 14.72) * mm});
            skLineSegment(sketch, "E414", {"start": v(20.68, 14.72) * mm, "end": v(20.8, 14.72) * mm});
            skLineSegment(sketch, "E415", {"start": v(20.8, 14.72) * mm, "end": v(23.23, 20.26) * mm});
            skLineSegment(sketch, "E416", {"start": v(23.23, 20.26) * mm, "end": v(25.27, 20.26) * mm});
            skLineSegment(sketch, "E417", {"start": v(25.27, 20.26) * mm, "end": v(25.29, 20.25) * mm});
            skLineSegment(sketch, "E418", {"start": v(25.29, 20.25) * mm, "end": v(25.32, 20.24) * mm});
            skLineSegment(sketch, "E419", {"start": v(25.32, 20.24) * mm, "end": v(25.37, 20.22) * mm});
            skLineSegment(sketch, "E420", {"start": v(25.37, 20.22) * mm, "end": v(25.42, 20.18) * mm});
            skLineSegment(sketch, "E421", {"start": v(25.42, 20.18) * mm, "end": v(25.46, 20.12) * mm});
            skLineSegment(sketch, "E422", {"start": v(25.46, 20.12) * mm, "end": v(25.48, 20.04) * mm});
            skLineSegment(sketch, "E423", {"start": v(25.48, 20.04) * mm, "end": v(25.48, 19.92) * mm});
            skLineSegment(sketch, "E424", {"start": v(25.48, 19.92) * mm, "end": v(25.45, 19.8) * mm});
            skLineSegment(sketch, "E425", {"start": v(25.45, 19.8) * mm, "end": v(25.43, 19.77) * mm});
            skLineSegment(sketch, "E426", {"start": v(25.43, 19.77) * mm, "end": v(25.41, 19.72) * mm});
            skLineSegment(sketch, "E427", {"start": v(25.41, 19.72) * mm, "end": v(25.34, 19.57) * mm});
            skLineSegment(sketch, "E428", {"start": v(25.34, 19.57) * mm, "end": v(25.23, 19.3) * mm});
            skLineSegment(sketch, "E429", {"start": v(25.23, 19.3) * mm, "end": v(25.1, 18.98) * mm});
            skLineSegment(sketch, "E430", {"start": v(25.1, 18.98) * mm, "end": v(24.95, 18.67) * mm});
            skLineSegment(sketch, "E431", {"start": v(24.95, 18.67) * mm, "end": v(24.82, 18.37) * mm});
            skLineSegment(sketch, "E432", {"start": v(24.82, 18.37) * mm, "end": v(24.7, 18.12) * mm});
            skLineSegment(sketch, "E433", {"start": v(24.7, 18.12) * mm, "end": v(24.63, 17.95) * mm});
            skLineSegment(sketch, "E434", {"start": v(24.63, 17.95) * mm, "end": v(24.6, 17.9) * mm});
            skLineSegment(sketch, "E435", {"start": v(24.6, 17.9) * mm, "end": v(24.6, 17.85) * mm});
            skLineSegment(sketch, "E436", {"start": v(24.6, 17.85) * mm, "end": v(24.56, 17.72) * mm});
            skLineSegment(sketch, "E437", {"start": v(24.56, 17.72) * mm, "end": v(24.51, 17.53) * mm});
            skLineSegment(sketch, "E438", {"start": v(24.51, 17.53) * mm, "end": v(24.48, 17.3) * mm});
            skLineSegment(sketch, "E439", {"start": v(24.48, 17.3) * mm, "end": v(24.47, 17.02) * mm});
            skLineSegment(sketch, "E440", {"start": v(24.47, 17.02) * mm, "end": v(24.5, 16.71) * mm});
            skLineSegment(sketch, "E441", {"start": v(24.5, 16.71) * mm, "end": v(24.56, 16.4) * mm});
            skLineSegment(sketch, "E442", {"start": v(24.56, 16.4) * mm, "end": v(24.66, 16.16) * mm});
            skLineSegment(sketch, "E443", {"start": v(24.66, 16.16) * mm, "end": v(24.7, 16.1) * mm});
            skLineSegment(sketch, "E444", {"start": v(24.7, 16.1) * mm, "end": v(24.75, 16.02) * mm});
            skLineSegment(sketch, "E445", {"start": v(24.75, 16.02) * mm, "end": v(24.9, 15.8) * mm});
            skLineSegment(sketch, "E446", {"start": v(24.9, 15.8) * mm, "end": v(25.13, 15.53) * mm});
            skLineSegment(sketch, "E447", {"start": v(25.13, 15.53) * mm, "end": v(25.42, 15.3) * mm});
            skLineSegment(sketch, "E448", {"start": v(25.42, 15.3) * mm, "end": v(25.76, 15.1) * mm});
            skLineSegment(sketch, "E449", {"start": v(25.76, 15.1) * mm, "end": v(26.15, 14.94) * mm});
            skLineSegment(sketch, "E450", {"start": v(26.15, 14.94) * mm, "end": v(26.6, 14.82) * mm});
            skLineSegment(sketch, "E451", {"start": v(26.6, 14.82) * mm, "end": v(27.13, 14.74) * mm});
            skLineSegment(sketch, "E452", {"start": v(27.13, 14.74) * mm, "end": v(27.58, 14.72) * mm});
            skLineSegment(sketch, "E453", {"start": v(27.58, 14.72) * mm, "end": v(27.73, 14.72) * mm});
            skLineSegment(sketch, "E454", {"start": v(27.73, 14.72) * mm, "end": v(27.97, 14.72) * mm});
            skLineSegment(sketch, "E455", {"start": v(27.97, 14.72) * mm, "end": v(28.68, 14.72) * mm});
            skLineSegment(sketch, "E456", {"start": v(28.68, 14.72) * mm, "end": v(29.6, 14.72) * mm});
            skLineSegment(sketch, "E457", {"start": v(29.6, 14.72) * mm, "end": v(30.38, 14.72) * mm});
            skLineSegment(sketch, "E458", {"start": v(30.38, 14.72) * mm, "end": v(30.82, 14.72) * mm});
            skLineSegment(sketch, "E459", {"start": v(30.82, 14.72) * mm, "end": v(30.97, 14.72) * mm});
            skLineSegment(sketch, "E460", {"start": v(9.33, 19.38) * mm, "end": v(9.35, 19.43) * mm});
            skLineSegment(sketch, "E461", {"start": v(9.35, 19.43) * mm, "end": v(9.4, 19.54) * mm});
            skLineSegment(sketch, "E462", {"start": v(9.4, 19.54) * mm, "end": v(9.5, 19.7) * mm});
            skLineSegment(sketch, "E463", {"start": v(9.5, 19.7) * mm, "end": v(9.62, 19.88) * mm});
            skLineSegment(sketch, "E464", {"start": v(9.62, 19.88) * mm, "end": v(9.78, 20.06) * mm});
            skLineSegment(sketch, "E465", {"start": v(9.78, 20.06) * mm, "end": v(9.96, 20.22) * mm});
            skLineSegment(sketch, "E466", {"start": v(9.96, 20.22) * mm, "end": v(10.16, 20.33) * mm});
            skLineSegment(sketch, "E467", {"start": v(10.16, 20.33) * mm, "end": v(10.33, 20.37) * mm});
            skLineSegment(sketch, "E468", {"start": v(10.33, 20.37) * mm, "end": v(10.39, 20.37) * mm});
            skLineSegment(sketch, "E469", {"start": v(10.39, 20.37) * mm, "end": v(10.49, 20.37) * mm});
            skLineSegment(sketch, "E470", {"start": v(10.49, 20.37) * mm, "end": v(10.8, 20.37) * mm});
            skLineSegment(sketch, "E471", {"start": v(10.8, 20.37) * mm, "end": v(11.08, 20.37) * mm});
            skLineSegment(sketch, "E472", {"start": v(11.08, 20.37) * mm, "end": v(11.25, 20.37) * mm});
            skLineSegment(sketch, "E473", {"start": v(11.25, 20.37) * mm, "end": v(11.3, 20.37) * mm});
            skLineSegment(sketch, "E474", {"start": v(11.3, 20.37) * mm, "end": v(12.32, 22.62) * mm});
            skLineSegment(sketch, "E475", {"start": v(12.32, 22.62) * mm, "end": v(10.58, 22.62) * mm});
            skLineSegment(sketch, "E476", {"start": v(10.58, 22.62) * mm, "end": v(10.54, 22.62) * mm});
            skLineSegment(sketch, "E477", {"start": v(10.54, 22.62) * mm, "end": v(10.43, 22.63) * mm});
            skLineSegment(sketch, "E478", {"start": v(10.43, 22.63) * mm, "end": v(10.27, 22.63) * mm});
            skLineSegment(sketch, "E479", {"start": v(10.27, 22.63) * mm, "end": v(10.07, 22.63) * mm});
            skLineSegment(sketch, "E480", {"start": v(10.07, 22.63) * mm, "end": v(9.84, 22.61) * mm});
            skLineSegment(sketch, "E481", {"start": v(9.84, 22.61) * mm, "end": v(9.6, 22.58) * mm});
            skLineSegment(sketch, "E482", {"start": v(9.6, 22.58) * mm, "end": v(9.35, 22.52) * mm});
            skLineSegment(sketch, "E483", {"start": v(9.35, 22.52) * mm, "end": v(9.18, 22.46) * mm});
            skLineSegment(sketch, "E484", {"start": v(9.18, 22.46) * mm, "end": v(9.13, 22.43) * mm});
            skLineSegment(sketch, "E485", {"start": v(9.13, 22.43) * mm, "end": v(9.07, 22.4) * mm});
            skLineSegment(sketch, "E486", {"start": v(9.07, 22.4) * mm, "end": v(8.9, 22.32) * mm});
            skLineSegment(sketch, "E487", {"start": v(8.9, 22.32) * mm, "end": v(8.64, 22.18) * mm});
            skLineSegment(sketch, "E488", {"start": v(8.64, 22.18) * mm, "end": v(8.37, 22) * mm});
            skLineSegment(sketch, "E489", {"start": v(8.37, 22) * mm, "end": v(8.09, 21.78) * mm});
            skLineSegment(sketch, "E490", {"start": v(8.09, 21.78) * mm, "end": v(7.8, 21.5) * mm});
            skLineSegment(sketch, "E491", {"start": v(7.8, 21.5) * mm, "end": v(7.51, 21.15) * mm});
            skLineSegment(sketch, "E492", {"start": v(7.51, 21.15) * mm, "end": v(7.24, 20.73) * mm});
            skLineSegment(sketch, "E493", {"start": v(7.24, 20.73) * mm, "end": v(7.04, 20.34) * mm});
            skLineSegment(sketch, "E494", {"start": v(7.04, 20.34) * mm, "end": v(6.99, 20.2) * mm});
            skLineSegment(sketch, "E495", {"start": v(6.99, 20.2) * mm, "end": v(6.92, 20.05) * mm});
            skLineSegment(sketch, "E496", {"start": v(6.92, 20.05) * mm, "end": v(6.71, 19.56) * mm});
            skLineSegment(sketch, "E497", {"start": v(6.71, 19.56) * mm, "end": v(6.46, 18.96) * mm});
            skLineSegment(sketch, "E498", {"start": v(6.46, 18.96) * mm, "end": v(6.23, 18.41) * mm});
            skLineSegment(sketch, "E499", {"start": v(6.23, 18.41) * mm, "end": v(6.03, 17.94) * mm});
            skLineSegment(sketch, "E500", {"start": v(6.03, 17.94) * mm, "end": v(5.86, 17.54) * mm});
            skLineSegment(sketch, "E501", {"start": v(5.86, 17.54) * mm, "end": v(5.74, 17.24) * mm});
            skLineSegment(sketch, "E502", {"start": v(5.74, 17.24) * mm, "end": v(5.66, 17.05) * mm});
            skLineSegment(sketch, "E503", {"start": v(5.66, 17.05) * mm, "end": v(5.64, 16.99) * mm});
            skLineSegment(sketch, "E504", {"start": v(5.64, 16.99) * mm, "end": v(3.87, 16.99) * mm});
            skLineSegment(sketch, "E505", {"start": v(3.87, 16.99) * mm, "end": v(3.83, 17) * mm});
            skLineSegment(sketch, "E506", {"start": v(3.83, 17) * mm, "end": v(3.75, 17.01) * mm});
            skLineSegment(sketch, "E507", {"start": v(3.75, 17.01) * mm, "end": v(3.64, 17.05) * mm});
            skLineSegment(sketch, "E508", {"start": v(3.64, 17.05) * mm, "end": v(3.51, 17.1) * mm});
            skLineSegment(sketch, "E509", {"start": v(3.51, 17.1) * mm, "end": v(3.4, 17.18) * mm});
            skLineSegment(sketch, "E510", {"start": v(3.4, 17.18) * mm, "end": v(3.32, 17.29) * mm});
            skLineSegment(sketch, "E511", {"start": v(3.32, 17.29) * mm, "end": v(3.3, 17.42) * mm});
            skLineSegment(sketch, "E512", {"start": v(3.3, 17.42) * mm, "end": v(3.32, 17.55) * mm});
            skLineSegment(sketch, "E513", {"start": v(3.32, 17.55) * mm, "end": v(3.33, 17.6) * mm});
            skLineSegment(sketch, "E514", {"start": v(3.33, 17.6) * mm, "end": v(3.36, 17.64) * mm});
            skLineSegment(sketch, "E515", {"start": v(3.36, 17.64) * mm, "end": v(3.42, 17.8) * mm});
            skLineSegment(sketch, "E516", {"start": v(3.42, 17.8) * mm, "end": v(3.57, 18.14) * mm});
            skLineSegment(sketch, "E517", {"start": v(3.57, 18.14) * mm, "end": v(3.75, 18.57) * mm});
            skLineSegment(sketch, "E518", {"start": v(3.75, 18.57) * mm, "end": v(3.95, 19.04) * mm});
            skLineSegment(sketch, "E519", {"start": v(3.95, 19.04) * mm, "end": v(4.15, 19.5) * mm});
            skLineSegment(sketch, "E520", {"start": v(4.15, 19.5) * mm, "end": v(4.3, 19.88) * mm});
            skLineSegment(sketch, "E521", {"start": v(4.3, 19.88) * mm, "end": v(4.42, 20.15) * mm});
            skLineSegment(sketch, "E522", {"start": v(4.42, 20.15) * mm, "end": v(4.47, 20.25) * mm});
            skLineSegment(sketch, "E523", {"start": v(4.47, 20.25) * mm, "end": v(6.9, 20.25) * mm});
            skLineSegment(sketch, "E524", {"start": v(6.9, 20.25) * mm, "end": v(7.75, 22.62) * mm});
            skLineSegment(sketch, "E525", {"start": v(7.75, 22.62) * mm, "end": v(5.5, 22.62) * mm});
            skLineSegment(sketch, "E526", {"start": v(5.5, 22.62) * mm, "end": v(6.82, 25.86) * mm});
            skLineSegment(sketch, "E527", {"start": v(6.82, 25.86) * mm, "end": v(4.16, 25.86) * mm});
            skLineSegment(sketch, "E528", {"start": v(4.16, 25.86) * mm, "end": v(2.76, 22.62) * mm});
            skLineSegment(sketch, "E529", {"start": v(2.76, 22.62) * mm, "end": v(1.68, 22.62) * mm});
            skLineSegment(sketch, "E530", {"start": v(1.68, 22.62) * mm, "end": v(0.7, 20.28) * mm});
            skLineSegment(sketch, "E531", {"start": v(0.7, 20.28) * mm, "end": v(1.86, 20.28) * mm});
            skLineSegment(sketch, "E532", {"start": v(1.86, 20.28) * mm, "end": v(0.9, 18.1) * mm});
            skLineSegment(sketch, "E533", {"start": v(0.9, 18.1) * mm, "end": v(0.88, 18.06) * mm});
            skLineSegment(sketch, "E534", {"start": v(0.88, 18.06) * mm, "end": v(0.84, 17.97) * mm});
            skLineSegment(sketch, "E535", {"start": v(0.84, 17.97) * mm, "end": v(0.79, 17.83) * mm});
            skLineSegment(sketch, "E536", {"start": v(0.79, 17.83) * mm, "end": v(0.74, 17.64) * mm});
            skLineSegment(sketch, "E537", {"start": v(0.74, 17.64) * mm, "end": v(0.7, 17.42) * mm});
            skLineSegment(sketch, "E538", {"start": v(0.7, 17.42) * mm, "end": v(0.67, 17.18) * mm});
            skLineSegment(sketch, "E539", {"start": v(0.67, 17.18) * mm, "end": v(0.68, 16.92) * mm});
            skLineSegment(sketch, "E540", {"start": v(0.68, 16.92) * mm, "end": v(0.72, 16.71) * mm});
            skLineSegment(sketch, "E541", {"start": v(0.72, 16.71) * mm, "end": v(0.74, 16.65) * mm});
            skLineSegment(sketch, "E542", {"start": v(0.74, 16.65) * mm, "end": v(0.76, 16.57) * mm});
            skLineSegment(sketch, "E543", {"start": v(0.76, 16.57) * mm, "end": v(0.83, 16.36) * mm});
            skLineSegment(sketch, "E544", {"start": v(0.83, 16.36) * mm, "end": v(0.97, 16.04) * mm});
            skLineSegment(sketch, "E545", {"start": v(0.97, 16.04) * mm, "end": v(1.16, 15.72) * mm});
            skLineSegment(sketch, "E546", {"start": v(1.16, 15.72) * mm, "end": v(1.4, 15.4) * mm});
            skLineSegment(sketch, "E547", {"start": v(1.4, 15.4) * mm, "end": v(1.7, 15.13) * mm});
            skLineSegment(sketch, "E548", {"start": v(1.7, 15.13) * mm, "end": v(2.07, 14.91) * mm});
            skLineSegment(sketch, "E549", {"start": v(2.07, 14.91) * mm, "end": v(2.5, 14.77) * mm});
            skLineSegment(sketch, "E550", {"start": v(2.5, 14.77) * mm, "end": v(2.89, 14.71) * mm});
            skLineSegment(sketch, "E551", {"start": v(2.89, 14.71) * mm, "end": v(3.02, 14.71) * mm});
            skLineSegment(sketch, "E552", {"start": v(3.02, 14.71) * mm, "end": v(7.31, 14.71) * mm});
            skLineSegment(sketch, "E553", {"start": v(7.31, 14.71) * mm, "end": v(9.33, 19.38) * mm});
            skLineSegment(sketch, "E554", {"start": v(-4.42, 17) * mm, "end": v(-4.46, 17) * mm});
            skLineSegment(sketch, "E555", {"start": v(-4.46, 17) * mm, "end": v(-4.58, 17.02) * mm});
            skLineSegment(sketch, "E556", {"start": v(-4.58, 17.02) * mm, "end": v(-4.7, 17.08) * mm});
            skLineSegment(sketch, "E557", {"start": v(-4.7, 17.08) * mm, "end": v(-4.78, 17.17) * mm});
            skLineSegment(sketch, "E558", {"start": v(-4.78, 17.17) * mm, "end": v(-4.82, 17.29) * mm});
            skLineSegment(sketch, "E559", {"start": v(-4.82, 17.29) * mm, "end": v(-4.82, 17.41) * mm});
            skLineSegment(sketch, "E560", {"start": v(-4.82, 17.41) * mm, "end": v(-4.8, 17.55) * mm});
            skLineSegment(sketch, "E561", {"start": v(-4.8, 17.55) * mm, "end": v(-4.77, 17.68) * mm});
            skLineSegment(sketch, "E562", {"start": v(-4.77, 17.68) * mm, "end": v(-4.74, 17.77) * mm});
            skLineSegment(sketch, "E563", {"start": v(-4.74, 17.77) * mm, "end": v(-4.72, 17.8) * mm});
            skLineSegment(sketch, "E564", {"start": v(-4.72, 17.8) * mm, "end": v(-4.68, 17.89) * mm});
            skLineSegment(sketch, "E565", {"start": v(-4.68, 17.89) * mm, "end": v(-4.55, 18.16) * mm});
            skLineSegment(sketch, "E566", {"start": v(-4.55, 18.16) * mm, "end": v(-4.37, 18.54) * mm});
            skLineSegment(sketch, "E567", {"start": v(-4.37, 18.54) * mm, "end": v(-4.18, 18.93) * mm});
            skLineSegment(sketch, "E568", {"start": v(-4.18, 18.93) * mm, "end": v(-4, 19.33) * mm});
            skLineSegment(sketch, "E569", {"start": v(-4, 19.33) * mm, "end": v(-3.81, 19.74) * mm});
            skLineSegment(sketch, "E570", {"start": v(-3.81, 19.74) * mm, "end": v(-3.63, 20.14) * mm});
            skLineSegment(sketch, "E571", {"start": v(-3.63, 20.14) * mm, "end": v(-3.46, 20.53) * mm});
            skLineSegment(sketch, "E572", {"start": v(-3.46, 20.53) * mm, "end": v(-3.3, 20.9) * mm});
            skLineSegment(sketch, "E573", {"start": v(-3.3, 20.9) * mm, "end": v(-3.14, 21.26) * mm});
            skLineSegment(sketch, "E574", {"start": v(-3.14, 21.26) * mm, "end": v(-3, 21.58) * mm});
            skLineSegment(sketch, "E575", {"start": v(-3, 21.58) * mm, "end": v(-2.87, 21.88) * mm});
            skLineSegment(sketch, "E576", {"start": v(-2.87, 21.88) * mm, "end": v(-2.76, 22.13) * mm});
            skLineSegment(sketch, "E577", {"start": v(-2.76, 22.13) * mm, "end": v(-2.67, 22.33) * mm});
            skLineSegment(sketch, "E578", {"start": v(-2.67, 22.33) * mm, "end": v(-2.6, 22.49) * mm});
            skLineSegment(sketch, "E579", {"start": v(-2.6, 22.49) * mm, "end": v(-2.56, 22.59) * mm});
            skLineSegment(sketch, "E580", {"start": v(-2.56, 22.59) * mm, "end": v(-2.55, 22.62) * mm});
            skLineSegment(sketch, "E581", {"start": v(-2.55, 22.62) * mm, "end": v(-7.8, 22.62) * mm});
            skLineSegment(sketch, "E582", {"start": v(-7.8, 22.62) * mm, "end": v(-7.85, 22.62) * mm});
            skLineSegment(sketch, "E583", {"start": v(-7.85, 22.62) * mm, "end": v(-8, 22.6) * mm});
            skLineSegment(sketch, "E584", {"start": v(-8, 22.6) * mm, "end": v(-8.23, 22.6) * mm});
            skLineSegment(sketch, "E585", {"start": v(-8.23, 22.6) * mm, "end": v(-8.5, 22.56) * mm});
            skLineSegment(sketch, "E586", {"start": v(-8.5, 22.56) * mm, "end": v(-8.79, 22.52) * mm});
            skLineSegment(sketch, "E587", {"start": v(-8.79, 22.52) * mm, "end": v(-9.08, 22.46) * mm});
            skLineSegment(sketch, "E588", {"start": v(-9.08, 22.46) * mm, "end": v(-9.35, 22.38) * mm});
            skLineSegment(sketch, "E589", {"start": v(-9.35, 22.38) * mm, "end": v(-9.52, 22.3) * mm});
            skLineSegment(sketch, "E590", {"start": v(-9.52, 22.3) * mm, "end": v(-9.57, 22.28) * mm});
            skLineSegment(sketch, "E591", {"start": v(-9.57, 22.28) * mm, "end": v(-9.62, 22.25) * mm});
            skLineSegment(sketch, "E592", {"start": v(-9.62, 22.25) * mm, "end": v(-9.77, 22.15) * mm});
            skLineSegment(sketch, "E593", {"start": v(-9.77, 22.15) * mm, "end": v(-10, 22.01) * mm});
            skLineSegment(sketch, "E594", {"start": v(-10, 22.01) * mm, "end": v(-10.24, 21.84) * mm});
            skLineSegment(sketch, "E595", {"start": v(-10.24, 21.84) * mm, "end": v(-10.5, 21.63) * mm});
            skLineSegment(sketch, "E596", {"start": v(-10.5, 21.63) * mm, "end": v(-10.75, 21.37) * mm});
            skLineSegment(sketch, "E597", {"start": v(-10.75, 21.37) * mm, "end": v(-11, 21.06) * mm});
            skLineSegment(sketch, "E598", {"start": v(-11, 21.06) * mm, "end": v(-11.24, 20.7) * mm});
            skLineSegment(sketch, "E599", {"start": v(-11.24, 20.7) * mm, "end": v(-11.4, 20.37) * mm});
            skLineSegment(sketch, "E600", {"start": v(-11.4, 20.37) * mm, "end": v(-11.45, 20.25) * mm});
            skLineSegment(sketch, "E601", {"start": v(-11.45, 20.25) * mm, "end": v(-11.5, 20.15) * mm});
            skLineSegment(sketch, "E602", {"start": v(-11.5, 20.15) * mm, "end": v(-11.63, 19.84) * mm});
            skLineSegment(sketch, "E603", {"start": v(-11.63, 19.84) * mm, "end": v(-11.76, 19.52) * mm});
            skLineSegment(sketch, "E604", {"start": v(-11.76, 19.52) * mm, "end": v(-11.85, 19.26) * mm});
            skLineSegment(sketch, "E605", {"start": v(-11.85, 19.26) * mm, "end": v(-11.93, 19.05) * mm});
            skLineSegment(sketch, "E606", {"start": v(-11.93, 19.05) * mm, "end": v(-12, 18.85) * mm});
            skLineSegment(sketch, "E607", {"start": v(-12, 18.85) * mm, "end": v(-12.1, 18.62) * mm});
            skLineSegment(sketch, "E608", {"start": v(-12.1, 18.62) * mm, "end": v(-12.2, 18.35) * mm});
            skLineSegment(sketch, "E609", {"start": v(-12.2, 18.35) * mm, "end": v(-12.32, 18.09) * mm});
            skLineSegment(sketch, "E610", {"start": v(-12.32, 18.09) * mm, "end": v(-12.36, 18) * mm});
            skLineSegment(sketch, "E611", {"start": v(-12.36, 18) * mm, "end": v(-12.4, 17.93) * mm});
            skLineSegment(sketch, "E612", {"start": v(-12.4, 17.93) * mm, "end": v(-12.5, 17.53) * mm});
            skLineSegment(sketch, "E613", {"start": v(-12.5, 17.53) * mm, "end": v(-12.56, 17.1) * mm});
            skLineSegment(sketch, "E614", {"start": v(-12.56, 17.1) * mm, "end": v(-12.56, 17) * mm});
            skLineSegment(sketch, "E615", {"start": v(-12.56, 17) * mm, "end": v(-14.58, 17) * mm});
            skLineSegment(sketch, "E616", {"start": v(-14.58, 17) * mm, "end": v(-14.62, 17) * mm});
            skLineSegment(sketch, "E617", {"start": v(-14.62, 17) * mm, "end": v(-14.78, 17.01) * mm});
            skLineSegment(sketch, "E618", {"start": v(-14.78, 17.01) * mm, "end": v(-14.93, 17.09) * mm});
            skLineSegment(sketch, "E619", {"start": v(-14.93, 17.09) * mm, "end": v(-14.96, 17.11) * mm});
            skLineSegment(sketch, "E620", {"start": v(-14.96, 17.11) * mm, "end": v(-15, 17.14) * mm});
            skLineSegment(sketch, "E621", {"start": v(-15, 17.14) * mm, "end": v(-15.06, 17.23) * mm});
            skLineSegment(sketch, "E622", {"start": v(-15.06, 17.23) * mm, "end": v(-15.12, 17.36) * mm});
            skLineSegment(sketch, "E623", {"start": v(-15.12, 17.36) * mm, "end": v(-15.13, 17.5) * mm});
            skLineSegment(sketch, "E624", {"start": v(-15.13, 17.5) * mm, "end": v(-15.11, 17.64) * mm});
            skLineSegment(sketch, "E625", {"start": v(-15.11, 17.64) * mm, "end": v(-15.1, 17.68) * mm});
            skLineSegment(sketch, "E626", {"start": v(-15.1, 17.68) * mm, "end": v(-15.08, 17.76) * mm});
            skLineSegment(sketch, "E627", {"start": v(-15.08, 17.76) * mm, "end": v(-14.99, 18.1) * mm});
            skLineSegment(sketch, "E628", {"start": v(-14.99, 18.1) * mm, "end": v(-14.87, 18.44) * mm});
            skLineSegment(sketch, "E629", {"start": v(-14.87, 18.44) * mm, "end": v(-14.84, 18.52) * mm});
            skLineSegment(sketch, "E630", {"start": v(-14.84, 18.52) * mm, "end": v(-14.78, 18.66) * mm});
            skLineSegment(sketch, "E631", {"start": v(-14.78, 18.66) * mm, "end": v(-14.6, 19.07) * mm});
            skLineSegment(sketch, "E632", {"start": v(-14.6, 19.07) * mm, "end": v(-14.4, 19.57) * mm});
            skLineSegment(sketch, "E633", {"start": v(-14.4, 19.57) * mm, "end": v(-14.2, 20.04) * mm});
            skLineSegment(sketch, "E634", {"start": v(-14.2, 20.04) * mm, "end": v(-14.02, 20.49) * mm});
            skLineSegment(sketch, "E635", {"start": v(-14.02, 20.49) * mm, "end": v(-13.83, 20.94) * mm});
            skLineSegment(sketch, "E636", {"start": v(-13.83, 20.94) * mm, "end": v(-13.63, 21.4) * mm});
            skLineSegment(sketch, "E637", {"start": v(-13.63, 21.4) * mm, "end": v(-13.41, 21.89) * mm});
            skLineSegment(sketch, "E638", {"start": v(-13.41, 21.89) * mm, "end": v(-13.23, 22.3) * mm});
            skLineSegment(sketch, "E639", {"start": v(-13.23, 22.3) * mm, "end": v(-13.17, 22.43) * mm});
            skLineSegment(sketch, "E640", {"start": v(-13.17, 22.43) * mm, "end": v(-13.16, 22.45) * mm});
            skLineSegment(sketch, "E641", {"start": v(-13.16, 22.45) * mm, "end": v(-13.13, 22.54) * mm});
            skLineSegment(sketch, "E642", {"start": v(-13.13, 22.54) * mm, "end": v(-13.1, 22.63) * mm});
            skLineSegment(sketch, "E643", {"start": v(-13.1, 22.63) * mm, "end": v(-13.09, 22.66) * mm});
            skLineSegment(sketch, "E644", {"start": v(-13.09, 22.66) * mm, "end": v(-13.05, 22.74) * mm});
            skLineSegment(sketch, "E645", {"start": v(-13.05, 22.74) * mm, "end": v(-12.87, 22.97) * mm});
            skLineSegment(sketch, "E646", {"start": v(-12.87, 22.97) * mm, "end": v(-12.6, 23.19) * mm});
            skLineSegment(sketch, "E647", {"start": v(-12.6, 23.19) * mm, "end": v(-12.26, 23.33) * mm});
            skLineSegment(sketch, "E648", {"start": v(-12.26, 23.33) * mm, "end": v(-11.97, 23.4) * mm});
            skLineSegment(sketch, "E649", {"start": v(-11.97, 23.4) * mm, "end": v(-11.88, 23.42) * mm});
            skLineSegment(sketch, "E650", {"start": v(-11.88, 23.42) * mm, "end": v(-11.84, 23.42) * mm});
            skLineSegment(sketch, "E651", {"start": v(-11.84, 23.42) * mm, "end": v(-11.71, 23.43) * mm});
            skLineSegment(sketch, "E652", {"start": v(-11.71, 23.43) * mm, "end": v(-11.55, 23.44) * mm});
            skLineSegment(sketch, "E653", {"start": v(-11.55, 23.44) * mm, "end": v(-11.42, 23.44) * mm});
            skLineSegment(sketch, "E654", {"start": v(-11.42, 23.44) * mm, "end": v(-11.37, 23.44) * mm});
            skLineSegment(sketch, "E655", {"start": v(-11.37, 23.44) * mm, "end": v(-7.5, 23.44) * mm});
            skLineSegment(sketch, "E656", {"start": v(-7.5, 23.44) * mm, "end": v(-6.4, 25.9) * mm});
            skLineSegment(sketch, "E657", {"start": v(-6.4, 25.9) * mm, "end": v(-6.6, 25.9) * mm});
            skLineSegment(sketch, "E658", {"start": v(-6.6, 25.9) * mm, "end": v(-7.21, 25.9) * mm});
            skLineSegment(sketch, "E659", {"start": v(-7.21, 25.9) * mm, "end": v(-7.91, 25.9) * mm});
            skLineSegment(sketch, "E660", {"start": v(-7.91, 25.9) * mm, "end": v(-8.53, 25.91) * mm});
            skLineSegment(sketch, "E661", {"start": v(-8.53, 25.91) * mm, "end": v(-9.08, 25.91) * mm});
            skLineSegment(sketch, "E662", {"start": v(-9.08, 25.91) * mm, "end": v(-9.6, 25.91) * mm});
            skLineSegment(sketch, "E663", {"start": v(-9.6, 25.91) * mm, "end": v(-10.1, 25.9) * mm});
            skLineSegment(sketch, "E664", {"start": v(-10.1, 25.9) * mm, "end": v(-10.6, 25.9) * mm});
            skLineSegment(sketch, "E665", {"start": v(-10.6, 25.9) * mm, "end": v(-11, 25.9) * mm});
            skLineSegment(sketch, "E666", {"start": v(-11, 25.9) * mm, "end": v(-11.14, 25.9) * mm});
            skLineSegment(sketch, "E667", {"start": v(-11.14, 25.9) * mm, "end": v(-11.29, 25.9) * mm});
            skLineSegment(sketch, "E668", {"start": v(-11.29, 25.9) * mm, "end": v(-11.73, 25.87) * mm});
            skLineSegment(sketch, "E669", {"start": v(-11.73, 25.87) * mm, "end": v(-12.31, 25.8) * mm});
            skLineSegment(sketch, "E670", {"start": v(-12.31, 25.8) * mm, "end": v(-12.88, 25.66) * mm});
            skLineSegment(sketch, "E671", {"start": v(-12.88, 25.66) * mm, "end": v(-13.41, 25.45) * mm});
            skLineSegment(sketch, "E672", {"start": v(-13.41, 25.45) * mm, "end": v(-13.91, 25.16) * mm});
            skLineSegment(sketch, "E673", {"start": v(-13.91, 25.16) * mm, "end": v(-14.38, 24.78) * mm});
            skLineSegment(sketch, "E674", {"start": v(-14.38, 24.78) * mm, "end": v(-14.79, 24.3) * mm});
            skLineSegment(sketch, "E675", {"start": v(-14.79, 24.3) * mm, "end": v(-15.07, 23.84) * mm});
            skLineSegment(sketch, "E676", {"start": v(-15.07, 23.84) * mm, "end": v(-15.15, 23.69) * mm});
            skLineSegment(sketch, "E677", {"start": v(-15.15, 23.69) * mm, "end": v(-15.2, 23.6) * mm});
            skLineSegment(sketch, "E678", {"start": v(-15.2, 23.6) * mm, "end": v(-15.32, 23.33) * mm});
            skLineSegment(sketch, "E679", {"start": v(-15.32, 23.33) * mm, "end": v(-15.5, 22.93) * mm});
            skLineSegment(sketch, "E680", {"start": v(-15.5, 22.93) * mm, "end": v(-15.7, 22.5) * mm});
            skLineSegment(sketch, "E681", {"start": v(-15.7, 22.5) * mm, "end": v(-15.9, 22.04) * mm});
            skLineSegment(sketch, "E682", {"start": v(-15.9, 22.04) * mm, "end": v(-16.1, 21.57) * mm});
            skLineSegment(sketch, "E683", {"start": v(-16.1, 21.57) * mm, "end": v(-16.31, 21.09) * mm});
            skLineSegment(sketch, "E684", {"start": v(-16.31, 21.09) * mm, "end": v(-16.51, 20.61) * mm});
            skLineSegment(sketch, "E685", {"start": v(-16.51, 20.61) * mm, "end": v(-16.7, 20.15) * mm});
            skLineSegment(sketch, "E686", {"start": v(-16.7, 20.15) * mm, "end": v(-16.9, 19.7) * mm});
            skLineSegment(sketch, "E687", {"start": v(-16.9, 19.7) * mm, "end": v(-17.06, 19.3) * mm});
            skLineSegment(sketch, "E688", {"start": v(-17.06, 19.3) * mm, "end": v(-17.22, 18.92) * mm});
            skLineSegment(sketch, "E689", {"start": v(-17.22, 18.92) * mm, "end": v(-17.35, 18.6) * mm});
            skLineSegment(sketch, "E690", {"start": v(-17.35, 18.6) * mm, "end": v(-17.46, 18.33) * mm});
            skLineSegment(sketch, "E691", {"start": v(-17.46, 18.33) * mm, "end": v(-17.54, 18.12) * mm});
            skLineSegment(sketch, "E692", {"start": v(-17.54, 18.12) * mm, "end": v(-17.6, 18) * mm});
            skLineSegment(sketch, "E693", {"start": v(-17.6, 18) * mm, "end": v(-17.61, 17.95) * mm});
            skLineSegment(sketch, "E694", {"start": v(-17.61, 17.95) * mm, "end": v(-17.62, 17.9) * mm});
            skLineSegment(sketch, "E695", {"start": v(-17.62, 17.9) * mm, "end": v(-17.65, 17.8) * mm});
            skLineSegment(sketch, "E696", {"start": v(-17.65, 17.8) * mm, "end": v(-17.7, 17.64) * mm});
            skLineSegment(sketch, "E697", {"start": v(-17.7, 17.64) * mm, "end": v(-17.74, 17.45) * mm});
            skLineSegment(sketch, "E698", {"start": v(-17.74, 17.45) * mm, "end": v(-17.78, 17.25) * mm});
            skLineSegment(sketch, "E699", {"start": v(-17.78, 17.25) * mm, "end": v(-17.82, 17.04) * mm});
            skLineSegment(sketch, "E700", {"start": v(-17.82, 17.04) * mm, "end": v(-17.84, 16.85) * mm});
            skLineSegment(sketch, "E701", {"start": v(-17.84, 16.85) * mm, "end": v(-17.84, 16.73) * mm});
            skLineSegment(sketch, "E702", {"start": v(-17.84, 16.73) * mm, "end": v(-17.84, 16.7) * mm});
            skLineSegment(sketch, "E703", {"start": v(-17.84, 16.7) * mm, "end": v(-17.83, 16.63) * mm});
            skLineSegment(sketch, "E704", {"start": v(-17.83, 16.63) * mm, "end": v(-17.8, 16.42) * mm});
            skLineSegment(sketch, "E705", {"start": v(-17.8, 16.42) * mm, "end": v(-17.7, 16.1) * mm});
            skLineSegment(sketch, "E706", {"start": v(-17.7, 16.1) * mm, "end": v(-17.56, 15.78) * mm});
            skLineSegment(sketch, "E707", {"start": v(-17.56, 15.78) * mm, "end": v(-17.34, 15.46) * mm});
            skLineSegment(sketch, "E708", {"start": v(-17.34, 15.46) * mm, "end": v(-17.03, 15.17) * mm});
            skLineSegment(sketch, "E709", {"start": v(-17.03, 15.17) * mm, "end": v(-16.62, 14.94) * mm});
            skLineSegment(sketch, "E710", {"start": v(-16.62, 14.94) * mm, "end": v(-16.1, 14.78) * mm});
            skLineSegment(sketch, "E711", {"start": v(-16.1, 14.78) * mm, "end": v(-15.6, 14.72) * mm});
            skLineSegment(sketch, "E712", {"start": v(-15.6, 14.72) * mm, "end": v(-15.44, 14.72) * mm});
            skLineSegment(sketch, "E713", {"start": v(-15.44, 14.72) * mm, "end": v(-15.32, 14.72) * mm});
            skLineSegment(sketch, "E714", {"start": v(-15.32, 14.72) * mm, "end": v(-14.94, 14.72) * mm});
            skLineSegment(sketch, "E715", {"start": v(-14.94, 14.72) * mm, "end": v(-14.33, 14.72) * mm});
            skLineSegment(sketch, "E716", {"start": v(-14.33, 14.72) * mm, "end": v(-13.6, 14.72) * mm});
            skLineSegment(sketch, "E717", {"start": v(-13.6, 14.72) * mm, "end": v(-12.8, 14.71) * mm});
            skLineSegment(sketch, "E718", {"start": v(-12.8, 14.71) * mm, "end": v(-11.92, 14.71) * mm});
            skLineSegment(sketch, "E719", {"start": v(-11.92, 14.71) * mm, "end": v(-10.99, 14.71) * mm});
            skLineSegment(sketch, "E720", {"start": v(-10.99, 14.71) * mm, "end": v(-10, 14.71) * mm});
            skLineSegment(sketch, "E721", {"start": v(-10, 14.71) * mm, "end": v(-9.24, 14.72) * mm});
            skLineSegment(sketch, "E722", {"start": v(-9.24, 14.72) * mm, "end": v(-9, 14.72) * mm});
            skLineSegment(sketch, "E723", {"start": v(-9, 14.72) * mm, "end": v(-8.96, 14.72) * mm});
            skLineSegment(sketch, "E724", {"start": v(-8.96, 14.72) * mm, "end": v(-8.87, 14.74) * mm});
            skLineSegment(sketch, "E725", {"start": v(-8.87, 14.74) * mm, "end": v(-8.74, 14.78) * mm});
            skLineSegment(sketch, "E726", {"start": v(-8.74, 14.78) * mm, "end": v(-8.58, 14.83) * mm});
            skLineSegment(sketch, "E727", {"start": v(-8.58, 14.83) * mm, "end": v(-8.4, 14.91) * mm});
            skLineSegment(sketch, "E728", {"start": v(-8.4, 14.91) * mm, "end": v(-8.22, 15.02) * mm});
            skLineSegment(sketch, "E729", {"start": v(-8.22, 15.02) * mm, "end": v(-8.05, 15.16) * mm});
            skLineSegment(sketch, "E730", {"start": v(-8.05, 15.16) * mm, "end": v(-7.93, 15.3) * mm});
            skLineSegment(sketch, "E731", {"start": v(-7.93, 15.3) * mm, "end": v(-7.9, 15.34) * mm});
            skLineSegment(sketch, "E732", {"start": v(-7.9, 15.34) * mm, "end": v(-7.83, 15.43) * mm});
            skLineSegment(sketch, "E733", {"start": v(-7.83, 15.43) * mm, "end": v(-7.64, 15.7) * mm});
            skLineSegment(sketch, "E734", {"start": v(-7.64, 15.7) * mm, "end": v(-7.45, 15.96) * mm});
            skLineSegment(sketch, "E735", {"start": v(-7.45, 15.96) * mm, "end": v(-7.34, 16.13) * mm});
            skLineSegment(sketch, "E736", {"start": v(-7.34, 16.13) * mm, "end": v(-7.3, 16.19) * mm});
            skLineSegment(sketch, "E737", {"start": v(-7.3, 16.19) * mm, "end": v(-7.28, 16.16) * mm});
            skLineSegment(sketch, "E738", {"start": v(-7.28, 16.16) * mm, "end": v(-7.25, 16.08) * mm});
            skLineSegment(sketch, "E739", {"start": v(-7.25, 16.08) * mm, "end": v(-7.19, 15.96) * mm});
            skLineSegment(sketch, "E740", {"start": v(-7.19, 15.96) * mm, "end": v(-7.1, 15.8) * mm});
            skLineSegment(sketch, "E741", {"start": v(-7.1, 15.8) * mm, "end": v(-6.99, 15.64) * mm});
            skLineSegment(sketch, "E742", {"start": v(-6.99, 15.64) * mm, "end": v(-6.84, 15.47) * mm});
            skLineSegment(sketch, "E743", {"start": v(-6.84, 15.47) * mm, "end": v(-6.66, 15.3) * mm});
            skLineSegment(sketch, "E744", {"start": v(-6.66, 15.3) * mm, "end": v(-6.5, 15.18) * mm});
            skLineSegment(sketch, "E745", {"start": v(-6.5, 15.18) * mm, "end": v(-6.44, 15.15) * mm});
            skLineSegment(sketch, "E746", {"start": v(-6.44, 15.15) * mm, "end": v(-6.34, 15.09) * mm});
            skLineSegment(sketch, "E747", {"start": v(-6.34, 15.09) * mm, "end": v(-6.03, 14.92) * mm});
            skLineSegment(sketch, "E748", {"start": v(-6.03, 14.92) * mm, "end": v(-5.71, 14.8) * mm});
            skLineSegment(sketch, "E749", {"start": v(-5.71, 14.8) * mm, "end": v(-5.42, 14.74) * mm});
            skLineSegment(sketch, "E750", {"start": v(-5.42, 14.74) * mm, "end": v(-5.17, 14.72) * mm});
            skLineSegment(sketch, "E751", {"start": v(-5.17, 14.72) * mm, "end": v(-5.09, 14.72) * mm});
            skLineSegment(sketch, "E752", {"start": v(-5.09, 14.72) * mm, "end": v(-4.59, 14.68) * mm});
            skLineSegment(sketch, "E753", {"start": v(-4.59, 14.68) * mm, "end": v(-4.5, 14.68) * mm});
            skLineSegment(sketch, "E754", {"start": v(-4.5, 14.68) * mm, "end": v(-4.2, 14.68) * mm});
            skLineSegment(sketch, "E755", {"start": v(-4.2, 14.68) * mm, "end": v(-3.8, 14.68) * mm});
            skLineSegment(sketch, "E756", {"start": v(-3.8, 14.68) * mm, "end": v(-3.39, 14.68) * mm});
            skLineSegment(sketch, "E757", {"start": v(-3.39, 14.68) * mm, "end": v(-3, 14.68) * mm});
            skLineSegment(sketch, "E758", {"start": v(-3, 14.68) * mm, "end": v(-2.67, 14.68) * mm});
            skLineSegment(sketch, "E759", {"start": v(-2.67, 14.68) * mm, "end": v(-2.4, 14.68) * mm});
            skLineSegment(sketch, "E760", {"start": v(-2.4, 14.68) * mm, "end": v(-2.23, 14.68) * mm});
            skLineSegment(sketch, "E761", {"start": v(-2.23, 14.68) * mm, "end": v(-2.17, 14.68) * mm});
            skLineSegment(sketch, "E762", {"start": v(-2.17, 14.68) * mm, "end": v(2.6, 25.88) * mm});
            skLineSegment(sketch, "E763", {"start": v(2.6, 25.88) * mm, "end": v(-0.08, 25.86) * mm});
            skLineSegment(sketch, "E764", {"start": v(-0.08, 25.86) * mm, "end": v(-3.9, 17) * mm});
            skLineSegment(sketch, "E765", {"start": v(-3.9, 17) * mm, "end": v(-4.42, 17) * mm});
            skSolve(sketch);
        }
        {
            var Q0;
            Q0 = qSketchRegion(id + "F4", true);
            extrude(context, id + "F5", {"entities" : qUnion([Q0]), "operationType" : NewBodyOperationType.REMOVE, "oppositeDirection" : true, "depth" : 1.52 * mm, "offsetDistance" : 25.4 * mm});
        }
        {
            var Q0;
            Q0=makeQuery(id+"F1.opExtrude","CAP_EDGE",EDGE,{"disambiguationData":[OSD([sQuery(id+"F0.wireOp",EDGE,"E2")])],"isStart":true});
            var Q1;
            Q1=makeQuery(id+"F1.opExtrude","CAP_EDGE",EDGE,{"disambiguationData":[OSD([sQuery(id+"F0.wireOp",EDGE,"E2")])],"isStart":false});
            fillet(context, id + "F6", {"entities" : qUnion([Q0, Q1]), "tangentPropagation" : true, "radius" : 7.62 * mm, "defaultsChanged" : true, "vertexSettings" : [], "allowEdgeOverflow" : false});
        }
        {
            var Q0;
            Q0=makeQuery(id+"F1.opExtrude","CAP_FACE",FACE,{"disambiguationData":[OSD([sQuery(id+"F0.wireOp",EDGE,"E0"),sQuery(id+"F0.wireOp",EDGE,"E1"),sQuery(id+"F0.wireOp",EDGE,"E2"),sQuery(id+"F0.wireOp",EDGE,"E3"),sQuery(id+"F0.wireOp",EDGE,"E4"),sQuery(id+"F0.wireOp",EDGE,"E5")])],"isStart":true});
            var sketch = newSketch(context, id + "F7", { "sketchPlane" : qUnion([Q0])});
            skCircle(sketch, "E766", {"center": v(0, -0.55) * mm, "radius": 25.4 * mm});
            skSolve(sketch);
        }
        {
            var Q0;
            Q0 = qSketchRegion(id + "F7", true);
            extrude(context, id + "F8", {"entities" : qUnion([Q0]), "operationType" : NewBodyOperationType.ADD, "depth" : 12.7 * mm, "offsetDistance" : 25.4 * mm});
        }
        {
            var Q0;
            Q0=makeQuery(id+"F1.opExtrude","SWEPT_EDGE",EDGE,{"disambiguationData":[OSD([sQuery(id+"F0.wireOp",EDGE,"E3"),sQuery(id+"F0.wireOp",EDGE,"E4")])]});
            fillet(context, id + "F9", {"entities" : qUnion([Q0]), "tangentPropagation" : true, "radius" : 6.35 * mm, "defaultsChanged" : true, "vertexSettings" : [], "allowEdgeOverflow" : false});
        }
        {
            var Q0;
            {var subQ0=sQuery(id+"F0.wireOp",EDGE,"E0");Q0=makeQuery(id+"F8.boolean.opBoolean","SPLIT",EDGE,{"disambiguationData":[topologyDisambiguationEdgeConnected([makeQuery(id+"F1.opExtrude","CAP_FACE",FACE,{"disambiguationData":[OSD([subQ0,sQuery(id+"F0.wireOp",EDGE,"E1"),sQuery(id+"F0.wireOp",EDGE,"E2"),sQuery(id+"F0.wireOp",EDGE,"E3"),sQuery(id+"F0.wireOp",EDGE,"E4"),sQuery(id+"F0.wireOp",EDGE,"E5")])],"isStart":true})])],"derivedFrom":makeQuery(id+"F1.opExtrude","CAP_EDGE",EDGE,{"disambiguationData":[OSD([subQ0])],"isStart":true})});}
            var Q1;
            Q1=makeQuery(id+"F1.opExtrude","SWEPT_EDGE",EDGE,{"disambiguationData":[OSD([sQuery(id+"F0.wireOp",EDGE,"E2"),sQuery(id+"F0.wireOp",EDGE,"E3")])]});
            fillet(context, id + "F10", {"entities" : qUnion([Q0, Q1]), "tangentPropagation" : true, "radius" : 1.52 * mm, "defaultsChanged" : false, "vertexSettings" : [], "allowEdgeOverflow" : false});
        }
        {
            var Q0;
            Q0=makeQuery(id+"F8.opExtrude","CAP_EDGE",EDGE,{"disambiguationData":[OSD([sQuery(id+"F7.wireOp",EDGE,"E766")])],"isStart":false});
            var Q1;
            {var subQ0=sQuery(id+"F7.wireOp",EDGE,"E766");Q1=makeQuery(id+"F8.boolean.opBoolean","SPLIT",EDGE,{"disambiguationData":[topologyDisambiguationEdgeConnected([makeQuery(id+"F8.opExtrude","CAP_FACE",FACE,{"disambiguationData":[OSD([subQ0])],"isStart":true})])],"derivedFrom":makeQuery(id+"F8.opExtrude","CAP_EDGE",EDGE,{"disambiguationData":[OSD([subQ0])],"isStart":true})});}
            var Q2;
            {var subQ0=sQuery(id+"F2.wireOp",EDGE,"E6");Q2=makeQuery(id+"F3.boolean.opBoolean","SPLIT",EDGE,{"disambiguationData":[topologyDisambiguationEdgeConnected([makeQuery(id+"F3.opExtrude","CAP_FACE",FACE,{"disambiguationData":[OSD([subQ0])],"isStart":true})])],"derivedFrom":makeQuery(id+"F3.opExtrude","CAP_EDGE",EDGE,{"disambiguationData":[OSD([subQ0])],"isStart":true})});}
            var Q3;
            Q3=makeQuery(id+"F3.opExtrude","CAP_EDGE",EDGE,{"disambiguationData":[OSD([sQuery(id+"F2.wireOp",EDGE,"E6")])],"isStart":false});
            chamfer(context, id + "F11", {"entities" : qUnion([Q0, Q1, Q2, Q3]), "width" : 1.52 * mm, "tangentPropagation" : true});
        }
        {
            var Q0;
            Q0=qCreatedBy(makeId("Top.planeOp"),FACE);
            var sketch = newSketch(context, id + "F12", { "sketchPlane" : qUnion([Q0])});
            skLineSegment(sketch, "E767", {"start": v(0, 63.66) * mm, "end": v(0, 42.88) * mm, "construction": true});
            skLineSegment(sketch, "E768.bottom", {"start": v(25.48, 57.99) * mm, "end": v(24.51, 57.99) * mm});
            skLineSegment(sketch, "E768.top", {"start": v(25.48, 57.1) * mm, "end": v(24.51, 57.1) * mm});
            skLineSegment(sketch, "E768.left", {"start": v(25.48, 57.99) * mm, "end": v(25.48, 57.1) * mm});
            skLineSegment(sketch, "E768.right", {"start": v(24.51, 57.99) * mm, "end": v(24.51, 57.1) * mm});
            skLineSegment(sketch, "E769", {"start": v(24.51, 57.99) * mm, "end": v(24.51, 49.16) * mm, "construction": true});
            skLineSegment(sketch, "E770.bottom", {"start": v(24.51, 56.21) * mm, "end": v(25.48, 56.21) * mm});
            skLineSegment(sketch, "E770.top", {"start": v(24.51, 55.32) * mm, "end": v(25.48, 55.32) * mm});
            skLineSegment(sketch, "E770.left", {"start": v(24.51, 56.21) * mm, "end": v(24.51, 55.32) * mm});
            skLineSegment(sketch, "E770.right", {"start": v(25.48, 56.21) * mm, "end": v(25.48, 55.32) * mm});
            skLineSegment(sketch, "E771.bottom", {"start": v(24.51, 54.43) * mm, "end": v(25.48, 54.43) * mm});
            skLineSegment(sketch, "E771.top", {"start": v(24.51, 53.54) * mm, "end": v(25.48, 53.54) * mm});
            skLineSegment(sketch, "E771.left", {"start": v(24.51, 54.43) * mm, "end": v(24.51, 53.54) * mm});
            skLineSegment(sketch, "E771.right", {"start": v(25.48, 54.43) * mm, "end": v(25.48, 53.54) * mm});
            skLineSegment(sketch, "E772.bottom", {"start": v(24.51, 52.65) * mm, "end": v(25.48, 52.65) * mm});
            skLineSegment(sketch, "E772.top", {"start": v(24.51, 51.77) * mm, "end": v(25.48, 51.77) * mm});
            skLineSegment(sketch, "E772.left", {"start": v(24.51, 52.65) * mm, "end": v(24.51, 51.77) * mm});
            skLineSegment(sketch, "E772.right", {"start": v(25.48, 52.65) * mm, "end": v(25.48, 51.77) * mm});
            skLineSegment(sketch, "E773.bottom", {"start": v(24.51, 50.88) * mm, "end": v(25.48, 50.88) * mm});
            skLineSegment(sketch, "E773.top", {"start": v(24.51, 49.96) * mm, "end": v(25.48, 49.96) * mm});
            skLineSegment(sketch, "E773.left", {"start": v(24.51, 50.88) * mm, "end": v(24.51, 49.96) * mm});
            skLineSegment(sketch, "E773.right", {"start": v(25.48, 50.88) * mm, "end": v(25.48, 49.96) * mm});
            skLineSegment(sketch, "E774", {"start": v(25.48, 57.99) * mm, "end": v(25.48, 49.87) * mm, "construction": true});
            skSolve(sketch);
        }
        {
            var Q0;
            Q0 = qSketchRegion(id + "F12", true);
            var Q1;
            Q1=sQuery(id+"F12.wireOp",EDGE,"E767");
            revolve(context, id + "F13", {"operationType" : NewBodyOperationType.REMOVE, "surfaceOperationType" : NewSurfaceOperationType.NEW, "entities" : qUnion([Q0]), "axis" : qUnion([Q1]), "revolveType" : RevolveType.FULL, "oppositeDirection" : true});
        }
        {
            var Q0;
            Q0=qCreatedBy(makeId("Right.planeOp"),FACE);
            var sketch = newSketch(context, id + "F14", { "sketchPlane" : qUnion([Q0])});
            skLineSegment(sketch, "E775", {"start": v(60.33, 0) * mm, "end": v(60.33, 22.35) * mm});
            skLineSegment(sketch, "E776", {"start": v(60.33, 22.35) * mm, "end": v(64.14, 19.05) * mm});
            skLineSegment(sketch, "E777", {"start": v(64.14, 19.05) * mm, "end": v(64.14, 3.18) * mm});
            skLineSegment(sketch, "E778", {"start": v(64.14, 3.18) * mm, "end": v(60.83, 3.18) * mm});
            skLineSegment(sketch, "E779", {"start": v(60.83, 3.18) * mm, "end": v(60.83, 0) * mm});
            skLineSegment(sketch, "E780", {"start": v(60.83, 0) * mm, "end": v(60.33, 0) * mm});
            skLineSegment(sketch, "E781", {"start": v(72.3, 0) * mm, "end": v(45.47, 0) * mm, "construction": true});
            skSolve(sketch);
        }
        {
            var Q0;
            Q0 = qSketchRegion(id + "F14", true);
            var Q1;
            Q1=sQuery(id+"F14.wireOp",EDGE,"E781");
            revolve(context, id + "F15", {"operationType" : NewBodyOperationType.ADD, "surfaceOperationType" : NewSurfaceOperationType.NEW, "entities" : qUnion([Q0]), "axis" : qUnion([Q1]), "revolveType" : RevolveType.FULL});
        }
        {
            var Q0;
            Q0=makeQuery(id+"F15.opRevolve","SWEPT_FACE",FACE,{"disambiguationData":[OSD([sQuery(id+"F14.wireOp",EDGE,"E777")])]});
            var sketch = newSketch(context, id + "F16", { "sketchPlane" : qUnion([Q0])});
            skPoint(sketch, "E782", {"position": v(0, 8.9) * mm});
            skSolve(sketch);
        }
        {
            var Q0;
            Q0=sQuery(id+"F16.wireOp",VERTEX,"E782");
            var Q1;
            Q1=makeQuery(id+"F1.opExtrude","SWEPT_BODY",BODY,{"disambiguationData":[OSD([sQuery(id+"F0.wireOp",EDGE,"E0"),sQuery(id+"F0.wireOp",EDGE,"E1"),sQuery(id+"F0.wireOp",EDGE,"E2"),sQuery(id+"F0.wireOp",EDGE,"E3"),sQuery(id+"F0.wireOp",EDGE,"E4"),sQuery(id+"F0.wireOp",EDGE,"E5")])]});
            hole(context, id + "F17", {"style" : HoleStyle.SIMPLE, "endStyle" : HoleEndStyle.BLIND, "holeDiameter" : 3.3 * mm, "majorDiameter" : 6.35 * mm, "holeDepth" : 2.54 * mm, "isTappedThrough" : true, "tappedDepth" : 12.7 * mm, "tapClearance" : 3, "locations" : qUnion([Q0]), "scope" : qUnion([Q1]), "startStyle" : HoleStartStyle.SKETCH});
        }
        {
            var Q0;
            Q0=makeQuery(id+"F15.opRevolve","SWEPT_FACE",FACE,{"disambiguationData":[OSD([sQuery(id+"F14.wireOp",EDGE,"E777")])]});
            var sketch = newSketch(context, id + "F18", { "sketchPlane" : qUnion([Q0])});
            skLineSegment(sketch, "E783.bottom", {"start": v(-25.4, -3.56) * mm, "end": v(25.4, -3.56) * mm});
            skLineSegment(sketch, "E783.top", {"start": v(-25.4, -34.04) * mm, "end": v(25.4, -34.04) * mm});
            skLineSegment(sketch, "E783.left", {"start": v(-25.4, -3.56) * mm, "end": v(-25.4, -34.04) * mm});
            skLineSegment(sketch, "E783.right", {"start": v(25.4, -3.56) * mm, "end": v(25.4, -34.04) * mm});
            skSolve(sketch);
        }
        {
            var Q0;
            Q0 = qSketchRegion(id + "F18", true);
            extrude(context, id + "F19", {"entities" : qUnion([Q0]), "operationType" : NewBodyOperationType.REMOVE, "endBound" : BoundingType.THROUGH_ALL, "oppositeDirection" : true, "depth" : 25.4 * mm, "offsetDistance" : 25.4 * mm});
        }
        {
            var Q0;
            Q0=makeQuery(id+"F1.opExtrude","SWEPT_FACE",FACE,{"disambiguationData":[OSD([sQuery(id+"F0.wireOp",EDGE,"E3")])]});
            var sketch = newSketch(context, id + "F20", { "sketchPlane" : qUnion([Q0])});
            skLineSegment(sketch, "E784", {"start": v(-29.14, 48.82) * mm, "end": v(-36.4, 48.82) * mm});
            skLineSegment(sketch, "E785", {"start": v(-36.4, 48.82) * mm, "end": v(-36.45, 48.82) * mm});
            skLineSegment(sketch, "E786", {"start": v(-36.45, 48.82) * mm, "end": v(-36.6, 48.8) * mm});
            skLineSegment(sketch, "E787", {"start": v(-36.6, 48.8) * mm, "end": v(-36.82, 48.76) * mm});
            skLineSegment(sketch, "E788", {"start": v(-36.82, 48.76) * mm, "end": v(-37.1, 48.69) * mm});
            skLineSegment(sketch, "E789", {"start": v(-37.1, 48.69) * mm, "end": v(-37.4, 48.57) * mm});
            skLineSegment(sketch, "E790", {"start": v(-37.4, 48.57) * mm, "end": v(-37.7, 48.4) * mm});
            skLineSegment(sketch, "E791", {"start": v(-37.7, 48.4) * mm, "end": v(-38, 48.16) * mm});
            skLineSegment(sketch, "E792", {"start": v(-38, 48.16) * mm, "end": v(-38.2, 47.93) * mm});
            skLineSegment(sketch, "E793", {"start": v(-38.2, 47.93) * mm, "end": v(-38.27, 47.85) * mm});
            skLineSegment(sketch, "E794", {"start": v(-38.27, 47.85) * mm, "end": v(-38.3, 47.8) * mm});
            skLineSegment(sketch, "E795", {"start": v(-38.3, 47.8) * mm, "end": v(-38.4, 47.62) * mm});
            skLineSegment(sketch, "E796", {"start": v(-38.4, 47.62) * mm, "end": v(-38.58, 47.3) * mm});
            skLineSegment(sketch, "E797", {"start": v(-38.58, 47.3) * mm, "end": v(-38.78, 46.89) * mm});
            skLineSegment(sketch, "E798", {"start": v(-38.78, 46.89) * mm, "end": v(-39, 46.42) * mm});
            skLineSegment(sketch, "E799", {"start": v(-39, 46.42) * mm, "end": v(-39.25, 45.9) * mm});
            skLineSegment(sketch, "E800", {"start": v(-39.25, 45.9) * mm, "end": v(-39.5, 45.35) * mm});
            skLineSegment(sketch, "E801", {"start": v(-39.5, 45.35) * mm, "end": v(-39.77, 44.78) * mm});
            skLineSegment(sketch, "E802", {"start": v(-39.77, 44.78) * mm, "end": v(-40.03, 44.2) * mm});
            skLineSegment(sketch, "E803", {"start": v(-40.03, 44.2) * mm, "end": v(-40.28, 43.63) * mm});
            skLineSegment(sketch, "E804", {"start": v(-40.28, 43.63) * mm, "end": v(-40.52, 43.1) * mm});
            skLineSegment(sketch, "E805", {"start": v(-40.52, 43.1) * mm, "end": v(-40.73, 42.6) * mm});
            skLineSegment(sketch, "E806", {"start": v(-40.73, 42.6) * mm, "end": v(-40.93, 42.16) * mm});
            skLineSegment(sketch, "E807", {"start": v(-40.93, 42.16) * mm, "end": v(-41.09, 41.79) * mm});
            skLineSegment(sketch, "E808", {"start": v(-41.09, 41.79) * mm, "end": v(-41.2, 41.5) * mm});
            skLineSegment(sketch, "E809", {"start": v(-41.2, 41.5) * mm, "end": v(-41.29, 41.33) * mm});
            skLineSegment(sketch, "E810", {"start": v(-41.29, 41.33) * mm, "end": v(-41.31, 41.26) * mm});
            skLineSegment(sketch, "E811", {"start": v(-41.31, 41.26) * mm, "end": v(-41.32, 41.2) * mm});
            skLineSegment(sketch, "E812", {"start": v(-41.32, 41.2) * mm, "end": v(-41.32, 41.04) * mm});
            skLineSegment(sketch, "E813", {"start": v(-41.32, 41.04) * mm, "end": v(-41.3, 40.81) * mm});
            skLineSegment(sketch, "E814", {"start": v(-41.3, 40.81) * mm, "end": v(-41.24, 40.54) * mm});
            skLineSegment(sketch, "E815", {"start": v(-41.24, 40.54) * mm, "end": v(-41.13, 40.24) * mm});
            skLineSegment(sketch, "E816", {"start": v(-41.13, 40.24) * mm, "end": v(-40.96, 39.96) * mm});
            skLineSegment(sketch, "E817", {"start": v(-40.96, 39.96) * mm, "end": v(-40.7, 39.71) * mm});
            skLineSegment(sketch, "E818", {"start": v(-40.7, 39.71) * mm, "end": v(-40.43, 39.57) * mm});
            skLineSegment(sketch, "E819", {"start": v(-40.43, 39.57) * mm, "end": v(-40.33, 39.53) * mm});
            skLineSegment(sketch, "E820", {"start": v(-40.33, 39.53) * mm, "end": v(-33.08, 39.53) * mm});
            skLineSegment(sketch, "E821", {"start": v(-33.08, 39.53) * mm, "end": v(-31.89, 42.14) * mm});
            skLineSegment(sketch, "E822", {"start": v(-31.89, 42.14) * mm, "end": v(-36.73, 42.14) * mm});
            skLineSegment(sketch, "E823", {"start": v(-36.73, 42.14) * mm, "end": v(-34.7, 46.13) * mm});
            skLineSegment(sketch, "E824", {"start": v(-34.7, 46.13) * mm, "end": v(-30.48, 46.13) * mm});
            skLineSegment(sketch, "E825", {"start": v(-30.48, 46.13) * mm, "end": v(-29.14, 48.82) * mm});
            skLineSegment(sketch, "E826", {"start": v(-29.98, 45.54) * mm, "end": v(-34.16, 45.54) * mm});
            skLineSegment(sketch, "E827", {"start": v(-34.16, 45.54) * mm, "end": v(-35.65, 42.66) * mm});
            skLineSegment(sketch, "E828", {"start": v(-35.65, 42.66) * mm, "end": v(-30.91, 42.66) * mm});
            skLineSegment(sketch, "E829", {"start": v(-30.91, 42.66) * mm, "end": v(-32.72, 38.61) * mm});
            skLineSegment(sketch, "E830", {"start": v(-32.72, 38.61) * mm, "end": v(-32.75, 38.55) * mm});
            skLineSegment(sketch, "E831", {"start": v(-32.75, 38.55) * mm, "end": v(-32.8, 38.4) * mm});
            skLineSegment(sketch, "E832", {"start": v(-32.8, 38.4) * mm, "end": v(-32.86, 38.17) * mm});
            skLineSegment(sketch, "E833", {"start": v(-32.86, 38.17) * mm, "end": v(-32.87, 37.9) * mm});
            skLineSegment(sketch, "E834", {"start": v(-32.87, 37.9) * mm, "end": v(-32.8, 37.62) * mm});
            skLineSegment(sketch, "E835", {"start": v(-32.8, 37.62) * mm, "end": v(-32.63, 37.35) * mm});
            skLineSegment(sketch, "E836", {"start": v(-32.63, 37.35) * mm, "end": v(-32.32, 37.13) * mm});
            skLineSegment(sketch, "E837", {"start": v(-32.32, 37.13) * mm, "end": v(-31.95, 37) * mm});
            skLineSegment(sketch, "E838", {"start": v(-31.95, 37) * mm, "end": v(-31.82, 36.97) * mm});
            skLineSegment(sketch, "E839", {"start": v(-31.82, 36.97) * mm, "end": v(-25.8, 36.97) * mm});
            skLineSegment(sketch, "E840", {"start": v(-25.8, 36.97) * mm, "end": v(-25.78, 36.97) * mm});
            skLineSegment(sketch, "E841", {"start": v(-25.78, 36.97) * mm, "end": v(-25.69, 36.97) * mm});
            skLineSegment(sketch, "E842", {"start": v(-25.69, 36.97) * mm, "end": v(-25.55, 36.97) * mm});
            skLineSegment(sketch, "E843", {"start": v(-25.55, 36.97) * mm, "end": v(-25.37, 37) * mm});
            skLineSegment(sketch, "E844", {"start": v(-25.37, 37) * mm, "end": v(-25.15, 37.06) * mm});
            skLineSegment(sketch, "E845", {"start": v(-25.15, 37.06) * mm, "end": v(-24.9, 37.17) * mm});
            skLineSegment(sketch, "E846", {"start": v(-24.9, 37.17) * mm, "end": v(-24.63, 37.32) * mm});
            skLineSegment(sketch, "E847", {"start": v(-24.63, 37.32) * mm, "end": v(-24.4, 37.48) * mm});
            skLineSegment(sketch, "E848", {"start": v(-24.4, 37.48) * mm, "end": v(-24.34, 37.54) * mm});
            skLineSegment(sketch, "E849", {"start": v(-24.34, 37.54) * mm, "end": v(-22.4, 42.06) * mm});
            skLineSegment(sketch, "E850", {"start": v(-22.4, 42.06) * mm, "end": v(-26.36, 42.06) * mm});
            skLineSegment(sketch, "E851", {"start": v(-26.36, 42.06) * mm, "end": v(-27.3, 39.85) * mm});
            skLineSegment(sketch, "E852", {"start": v(-27.3, 39.85) * mm, "end": v(-27.33, 39.82) * mm});
            skLineSegment(sketch, "E853", {"start": v(-27.33, 39.82) * mm, "end": v(-27.4, 39.75) * mm});
            skLineSegment(sketch, "E854", {"start": v(-27.4, 39.75) * mm, "end": v(-27.5, 39.66) * mm});
            skLineSegment(sketch, "E855", {"start": v(-27.5, 39.66) * mm, "end": v(-27.61, 39.58) * mm});
            skLineSegment(sketch, "E856", {"start": v(-27.61, 39.58) * mm, "end": v(-27.73, 39.54) * mm});
            skLineSegment(sketch, "E857", {"start": v(-27.73, 39.54) * mm, "end": v(-27.85, 39.55) * mm});
            skLineSegment(sketch, "E858", {"start": v(-27.85, 39.55) * mm, "end": v(-27.94, 39.66) * mm});
            skLineSegment(sketch, "E859", {"start": v(-27.94, 39.66) * mm, "end": v(-28, 39.82) * mm});
            skLineSegment(sketch, "E860", {"start": v(-28, 39.82) * mm, "end": v(-28, 39.88) * mm});
            skLineSegment(sketch, "E861", {"start": v(-28, 39.88) * mm, "end": v(-26.75, 42.82) * mm});
            skLineSegment(sketch, "E862", {"start": v(-26.75, 42.82) * mm, "end": v(-22.06, 42.82) * mm});
            skLineSegment(sketch, "E863", {"start": v(-22.06, 42.82) * mm, "end": v(-20.91, 45.54) * mm});
            skLineSegment(sketch, "E864", {"start": v(-20.91, 45.54) * mm, "end": v(-25.65, 45.54) * mm});
            skLineSegment(sketch, "E865", {"start": v(-25.65, 45.54) * mm, "end": v(-24.33, 48.84) * mm});
            skLineSegment(sketch, "E866", {"start": v(-24.33, 48.84) * mm, "end": v(-28.37, 48.84) * mm});
            skLineSegment(sketch, "E867", {"start": v(-28.37, 48.84) * mm, "end": v(-29.98, 45.54) * mm});
            skLineSegment(sketch, "E868", {"start": v(17.3, 43.05) * mm, "end": v(19.43, 43.04) * mm});
            skLineSegment(sketch, "E869", {"start": v(19.43, 43.04) * mm, "end": v(19.37, 42.9) * mm});
            skLineSegment(sketch, "E870", {"start": v(19.37, 42.9) * mm, "end": v(19.19, 42.5) * mm});
            skLineSegment(sketch, "E871", {"start": v(19.19, 42.5) * mm, "end": v(18.93, 41.95) * mm});
            skLineSegment(sketch, "E872", {"start": v(18.93, 41.95) * mm, "end": v(18.7, 41.4) * mm});
            skLineSegment(sketch, "E873", {"start": v(18.7, 41.4) * mm, "end": v(18.48, 40.87) * mm});
            skLineSegment(sketch, "E874", {"start": v(18.48, 40.87) * mm, "end": v(18.3, 40.39) * mm});
            skLineSegment(sketch, "E875", {"start": v(18.3, 40.39) * mm, "end": v(18.2, 39.98) * mm});
            skLineSegment(sketch, "E876", {"start": v(18.2, 39.98) * mm, "end": v(18.16, 39.67) * mm});
            skLineSegment(sketch, "E877", {"start": v(18.16, 39.67) * mm, "end": v(18.2, 39.5) * mm});
            skLineSegment(sketch, "E878", {"start": v(18.2, 39.5) * mm, "end": v(18.22, 39.47) * mm});
            skLineSegment(sketch, "E879", {"start": v(18.22, 39.47) * mm, "end": v(15.76, 39.47) * mm});
            skLineSegment(sketch, "E880", {"start": v(15.76, 39.47) * mm, "end": v(15.74, 39.47) * mm});
            skLineSegment(sketch, "E881", {"start": v(15.74, 39.47) * mm, "end": v(15.67, 39.5) * mm});
            skLineSegment(sketch, "E882", {"start": v(15.67, 39.5) * mm, "end": v(15.6, 39.55) * mm});
            skLineSegment(sketch, "E883", {"start": v(15.6, 39.55) * mm, "end": v(15.53, 39.63) * mm});
            skLineSegment(sketch, "E884", {"start": v(15.53, 39.63) * mm, "end": v(15.49, 39.71) * mm});
            skLineSegment(sketch, "E885", {"start": v(15.49, 39.71) * mm, "end": v(15.46, 39.8) * mm});
            skLineSegment(sketch, "E886", {"start": v(15.46, 39.8) * mm, "end": v(15.45, 39.87) * mm});
            skLineSegment(sketch, "E887", {"start": v(15.45, 39.87) * mm, "end": v(15.45, 39.92) * mm});
            skLineSegment(sketch, "E888", {"start": v(15.45, 39.92) * mm, "end": v(15.46, 39.95) * mm});
            skLineSegment(sketch, "E889", {"start": v(15.46, 39.95) * mm, "end": v(15.46, 39.95) * mm});
            skLineSegment(sketch, "E890", {"start": v(15.46, 39.95) * mm, "end": v(15.46, 40.04) * mm});
            skLineSegment(sketch, "E891", {"start": v(15.46, 40.04) * mm, "end": v(15.5, 40.34) * mm});
            skLineSegment(sketch, "E892", {"start": v(15.5, 40.34) * mm, "end": v(15.58, 40.67) * mm});
            skLineSegment(sketch, "E893", {"start": v(15.58, 40.67) * mm, "end": v(15.71, 41) * mm});
            skLineSegment(sketch, "E894", {"start": v(15.71, 41) * mm, "end": v(15.83, 41.26) * mm});
            skLineSegment(sketch, "E895", {"start": v(15.83, 41.26) * mm, "end": v(15.86, 41.35) * mm});
            skLineSegment(sketch, "E896", {"start": v(15.86, 41.35) * mm, "end": v(15.9, 41.45) * mm});
            skLineSegment(sketch, "E897", {"start": v(15.9, 41.45) * mm, "end": v(16.06, 41.87) * mm});
            skLineSegment(sketch, "E898", {"start": v(16.06, 41.87) * mm, "end": v(16.26, 42.27) * mm});
            skLineSegment(sketch, "E899", {"start": v(16.26, 42.27) * mm, "end": v(16.31, 42.35) * mm});
            skLineSegment(sketch, "E900", {"start": v(16.31, 42.35) * mm, "end": v(16.36, 42.41) * mm});
            skLineSegment(sketch, "E901", {"start": v(16.36, 42.41) * mm, "end": v(16.51, 42.61) * mm});
            skLineSegment(sketch, "E902", {"start": v(16.51, 42.61) * mm, "end": v(16.73, 42.84) * mm});
            skLineSegment(sketch, "E903", {"start": v(16.73, 42.84) * mm, "end": v(16.98, 42.99) * mm});
            skLineSegment(sketch, "E904", {"start": v(16.98, 42.99) * mm, "end": v(17.22, 43.05) * mm});
            skLineSegment(sketch, "E905", {"start": v(17.22, 43.05) * mm, "end": v(17.3, 43.05) * mm});
            skLineSegment(sketch, "E906", {"start": v(-7.84, 43.05) * mm, "end": v(-5.71, 43.04) * mm});
            skLineSegment(sketch, "E907", {"start": v(-5.71, 43.04) * mm, "end": v(-5.77, 42.9) * mm});
            skLineSegment(sketch, "E908", {"start": v(-5.77, 42.9) * mm, "end": v(-5.96, 42.5) * mm});
            skLineSegment(sketch, "E909", {"start": v(-5.96, 42.5) * mm, "end": v(-6.2, 41.95) * mm});
            skLineSegment(sketch, "E910", {"start": v(-6.2, 41.95) * mm, "end": v(-6.45, 41.4) * mm});
            skLineSegment(sketch, "E911", {"start": v(-6.45, 41.4) * mm, "end": v(-6.66, 40.87) * mm});
            skLineSegment(sketch, "E912", {"start": v(-6.66, 40.87) * mm, "end": v(-6.83, 40.39) * mm});
            skLineSegment(sketch, "E913", {"start": v(-6.83, 40.39) * mm, "end": v(-6.94, 39.98) * mm});
            skLineSegment(sketch, "E914", {"start": v(-6.94, 39.98) * mm, "end": v(-6.98, 39.67) * mm});
            skLineSegment(sketch, "E915", {"start": v(-6.98, 39.67) * mm, "end": v(-6.95, 39.5) * mm});
            skLineSegment(sketch, "E916", {"start": v(-6.95, 39.5) * mm, "end": v(-6.92, 39.47) * mm});
            skLineSegment(sketch, "E917", {"start": v(-6.92, 39.47) * mm, "end": v(-9.38, 39.47) * mm});
            skLineSegment(sketch, "E918", {"start": v(-9.38, 39.47) * mm, "end": v(-9.4, 39.47) * mm});
            skLineSegment(sketch, "E919", {"start": v(-9.4, 39.47) * mm, "end": v(-9.48, 39.5) * mm});
            skLineSegment(sketch, "E920", {"start": v(-9.48, 39.5) * mm, "end": v(-9.55, 39.55) * mm});
            skLineSegment(sketch, "E921", {"start": v(-9.55, 39.55) * mm, "end": v(-9.61, 39.63) * mm});
            skLineSegment(sketch, "E922", {"start": v(-9.61, 39.63) * mm, "end": v(-9.66, 39.71) * mm});
            skLineSegment(sketch, "E923", {"start": v(-9.66, 39.71) * mm, "end": v(-9.68, 39.8) * mm});
            skLineSegment(sketch, "E924", {"start": v(-9.68, 39.8) * mm, "end": v(-9.7, 39.87) * mm});
            skLineSegment(sketch, "E925", {"start": v(-9.7, 39.87) * mm, "end": v(-9.7, 39.92) * mm});
            skLineSegment(sketch, "E926", {"start": v(-9.7, 39.92) * mm, "end": v(-9.68, 39.95) * mm});
            skLineSegment(sketch, "E927", {"start": v(-9.68, 39.95) * mm, "end": v(-9.68, 39.95) * mm});
            skLineSegment(sketch, "E928", {"start": v(-9.68, 39.95) * mm, "end": v(-9.68, 40.04) * mm});
            skLineSegment(sketch, "E929", {"start": v(-9.68, 40.04) * mm, "end": v(-9.65, 40.34) * mm});
            skLineSegment(sketch, "E930", {"start": v(-9.65, 40.34) * mm, "end": v(-9.56, 40.67) * mm});
            skLineSegment(sketch, "E931", {"start": v(-9.56, 40.67) * mm, "end": v(-9.43, 41) * mm});
            skLineSegment(sketch, "E932", {"start": v(-9.43, 41) * mm, "end": v(-9.32, 41.26) * mm});
            skLineSegment(sketch, "E933", {"start": v(-9.32, 41.26) * mm, "end": v(-9.28, 41.35) * mm});
            skLineSegment(sketch, "E934", {"start": v(-9.28, 41.35) * mm, "end": v(-9.25, 41.45) * mm});
            skLineSegment(sketch, "E935", {"start": v(-9.25, 41.45) * mm, "end": v(-9.08, 41.87) * mm});
            skLineSegment(sketch, "E936", {"start": v(-9.08, 41.87) * mm, "end": v(-8.88, 42.27) * mm});
            skLineSegment(sketch, "E937", {"start": v(-8.88, 42.27) * mm, "end": v(-8.83, 42.35) * mm});
            skLineSegment(sketch, "E938", {"start": v(-8.83, 42.35) * mm, "end": v(-8.78, 42.41) * mm});
            skLineSegment(sketch, "E939", {"start": v(-8.78, 42.41) * mm, "end": v(-8.63, 42.61) * mm});
            skLineSegment(sketch, "E940", {"start": v(-8.63, 42.61) * mm, "end": v(-8.41, 42.84) * mm});
            skLineSegment(sketch, "E941", {"start": v(-8.41, 42.84) * mm, "end": v(-8.16, 42.99) * mm});
            skLineSegment(sketch, "E942", {"start": v(-8.16, 42.99) * mm, "end": v(-7.92, 43.05) * mm});
            skLineSegment(sketch, "E943", {"start": v(-7.92, 43.05) * mm, "end": v(-7.84, 43.05) * mm});
            skLineSegment(sketch, "E944", {"start": v(35.1, 36.99) * mm, "end": v(35.24, 37) * mm});
            skLineSegment(sketch, "E945", {"start": v(35.24, 37) * mm, "end": v(35.62, 37.02) * mm});
            skLineSegment(sketch, "E946", {"start": v(35.62, 37.02) * mm, "end": v(36.2, 37.13) * mm});
            skLineSegment(sketch, "E947", {"start": v(36.2, 37.13) * mm, "end": v(36.85, 37.35) * mm});
            skLineSegment(sketch, "E948", {"start": v(36.85, 37.35) * mm, "end": v(37.44, 37.61) * mm});
            skLineSegment(sketch, "E949", {"start": v(37.44, 37.61) * mm, "end": v(37.63, 37.71) * mm});
            skLineSegment(sketch, "E950", {"start": v(37.63, 37.71) * mm, "end": v(37.73, 37.76) * mm});
            skLineSegment(sketch, "E951", {"start": v(37.73, 37.76) * mm, "end": v(38.02, 37.95) * mm});
            skLineSegment(sketch, "E952", {"start": v(38.02, 37.95) * mm, "end": v(38.35, 38.2) * mm});
            skLineSegment(sketch, "E953", {"start": v(38.35, 38.2) * mm, "end": v(38.63, 38.47) * mm});
            skLineSegment(sketch, "E954", {"start": v(38.63, 38.47) * mm, "end": v(38.85, 38.73) * mm});
            skLineSegment(sketch, "E955", {"start": v(38.85, 38.73) * mm, "end": v(39.02, 38.95) * mm});
            skLineSegment(sketch, "E956", {"start": v(39.02, 38.95) * mm, "end": v(39.14, 39.14) * mm});
            skLineSegment(sketch, "E957", {"start": v(39.14, 39.14) * mm, "end": v(39.2, 39.26) * mm});
            skLineSegment(sketch, "E958", {"start": v(39.2, 39.26) * mm, "end": v(39.23, 39.3) * mm});
            skLineSegment(sketch, "E959", {"start": v(39.23, 39.3) * mm, "end": v(40.61, 42.42) * mm});
            skLineSegment(sketch, "E960", {"start": v(40.61, 42.42) * mm, "end": v(35.84, 42.42) * mm});
            skLineSegment(sketch, "E961", {"start": v(35.84, 42.42) * mm, "end": v(35.83, 42.4) * mm});
            skLineSegment(sketch, "E962", {"start": v(35.83, 42.4) * mm, "end": v(35.8, 42.37) * mm});
            skLineSegment(sketch, "E963", {"start": v(35.8, 42.37) * mm, "end": v(35.78, 42.33) * mm});
            skLineSegment(sketch, "E964", {"start": v(35.78, 42.33) * mm, "end": v(35.77, 42.3) * mm});
            skLineSegment(sketch, "E965", {"start": v(35.77, 42.3) * mm, "end": v(35.77, 42.3) * mm});
            skLineSegment(sketch, "E966", {"start": v(35.77, 42.3) * mm, "end": v(35.8, 42.34) * mm});
            skLineSegment(sketch, "E967", {"start": v(35.8, 42.34) * mm, "end": v(35.85, 42.44) * mm});
            skLineSegment(sketch, "E968", {"start": v(35.85, 42.44) * mm, "end": v(35.93, 42.57) * mm});
            skLineSegment(sketch, "E969", {"start": v(35.93, 42.57) * mm, "end": v(35.96, 42.62) * mm});
            skLineSegment(sketch, "E970", {"start": v(35.96, 42.62) * mm, "end": v(35.99, 42.67) * mm});
            skLineSegment(sketch, "E971", {"start": v(35.99, 42.67) * mm, "end": v(36.1, 42.82) * mm});
            skLineSegment(sketch, "E972", {"start": v(36.1, 42.82) * mm, "end": v(36.29, 42.98) * mm});
            skLineSegment(sketch, "E973", {"start": v(36.29, 42.98) * mm, "end": v(36.48, 43.1) * mm});
            skLineSegment(sketch, "E974", {"start": v(36.48, 43.1) * mm, "end": v(36.67, 43.2) * mm});
            skLineSegment(sketch, "E975", {"start": v(36.67, 43.2) * mm, "end": v(36.84, 43.27) * mm});
            skLineSegment(sketch, "E976", {"start": v(36.84, 43.27) * mm, "end": v(36.98, 43.32) * mm});
            skLineSegment(sketch, "E977", {"start": v(36.98, 43.32) * mm, "end": v(37.08, 43.34) * mm});
            skLineSegment(sketch, "E978", {"start": v(37.08, 43.34) * mm, "end": v(37.12, 43.35) * mm});
            skLineSegment(sketch, "E979", {"start": v(37.12, 43.35) * mm, "end": v(41.01, 43.35) * mm});
            skLineSegment(sketch, "E980", {"start": v(41.01, 43.35) * mm, "end": v(42.05, 45.66) * mm});
            skLineSegment(sketch, "E981", {"start": v(42.05, 45.66) * mm, "end": v(42, 45.66) * mm});
            skLineSegment(sketch, "E982", {"start": v(42, 45.66) * mm, "end": v(41.83, 45.66) * mm});
            skLineSegment(sketch, "E983", {"start": v(41.83, 45.66) * mm, "end": v(41.57, 45.66) * mm});
            skLineSegment(sketch, "E984", {"start": v(41.57, 45.66) * mm, "end": v(41.23, 45.66) * mm});
            skLineSegment(sketch, "E985", {"start": v(41.23, 45.66) * mm, "end": v(40.84, 45.66) * mm});
            skLineSegment(sketch, "E986", {"start": v(40.84, 45.66) * mm, "end": v(40.39, 45.66) * mm});
            skLineSegment(sketch, "E987", {"start": v(40.39, 45.66) * mm, "end": v(39.9, 45.66) * mm});
            skLineSegment(sketch, "E988", {"start": v(39.9, 45.66) * mm, "end": v(39.4, 45.66) * mm});
            skLineSegment(sketch, "E989", {"start": v(39.4, 45.66) * mm, "end": v(38.9, 45.66) * mm});
            skLineSegment(sketch, "E990", {"start": v(38.9, 45.66) * mm, "end": v(38.4, 45.66) * mm});
            skLineSegment(sketch, "E991", {"start": v(38.4, 45.66) * mm, "end": v(37.92, 45.66) * mm});
            skLineSegment(sketch, "E992", {"start": v(37.92, 45.66) * mm, "end": v(37.49, 45.66) * mm});
            skLineSegment(sketch, "E993", {"start": v(37.49, 45.66) * mm, "end": v(37.1, 45.66) * mm});
            skLineSegment(sketch, "E994", {"start": v(37.1, 45.66) * mm, "end": v(36.79, 45.66) * mm});
            skLineSegment(sketch, "E995", {"start": v(36.79, 45.66) * mm, "end": v(36.55, 45.66) * mm});
            skLineSegment(sketch, "E996", {"start": v(36.55, 45.66) * mm, "end": v(36.45, 45.66) * mm});
            skLineSegment(sketch, "E997", {"start": v(36.45, 45.66) * mm, "end": v(36.41, 45.66) * mm});
            skLineSegment(sketch, "E998", {"start": v(36.41, 45.66) * mm, "end": v(36.31, 45.66) * mm});
            skLineSegment(sketch, "E999", {"start": v(36.31, 45.66) * mm, "end": v(36, 45.62) * mm});
            skLineSegment(sketch, "E1000", {"start": v(36, 45.62) * mm, "end": v(35.53, 45.5) * mm});
            skLineSegment(sketch, "E1001", {"start": v(35.53, 45.5) * mm, "end": v(35.07, 45.33) * mm});
            skLineSegment(sketch, "E1002", {"start": v(35.07, 45.33) * mm, "end": v(34.79, 45.17) * mm});
            skLineSegment(sketch, "E1003", {"start": v(34.79, 45.17) * mm, "end": v(34.71, 45.1) * mm});
            skLineSegment(sketch, "E1004", {"start": v(34.71, 45.1) * mm, "end": v(34.63, 45.03) * mm});
            skLineSegment(sketch, "E1005", {"start": v(34.63, 45.03) * mm, "end": v(34.39, 44.8) * mm});
            skLineSegment(sketch, "E1006", {"start": v(34.39, 44.8) * mm, "end": v(34.13, 44.52) * mm});
            skLineSegment(sketch, "E1007", {"start": v(34.13, 44.52) * mm, "end": v(33.93, 44.28) * mm});
            skLineSegment(sketch, "E1008", {"start": v(33.93, 44.28) * mm, "end": v(33.78, 44.06) * mm});
            skLineSegment(sketch, "E1009", {"start": v(33.78, 44.06) * mm, "end": v(33.68, 43.89) * mm});
            skLineSegment(sketch, "E1010", {"start": v(33.68, 43.89) * mm, "end": v(33.61, 43.76) * mm});
            skLineSegment(sketch, "E1011", {"start": v(33.61, 43.76) * mm, "end": v(33.58, 43.68) * mm});
            skLineSegment(sketch, "E1012", {"start": v(33.58, 43.68) * mm, "end": v(33.57, 43.65) * mm});
            skLineSegment(sketch, "E1013", {"start": v(33.57, 43.65) * mm, "end": v(32.31, 40.66) * mm});
            skLineSegment(sketch, "E1014", {"start": v(32.31, 40.66) * mm, "end": v(37.04, 40.66) * mm});
            skLineSegment(sketch, "E1015", {"start": v(37.04, 40.66) * mm, "end": v(37.03, 40.62) * mm});
            skLineSegment(sketch, "E1016", {"start": v(37.03, 40.62) * mm, "end": v(37, 40.54) * mm});
            skLineSegment(sketch, "E1017", {"start": v(37, 40.54) * mm, "end": v(36.98, 40.46) * mm});
            skLineSegment(sketch, "E1018", {"start": v(36.98, 40.46) * mm, "end": v(36.97, 40.41) * mm});
            skLineSegment(sketch, "E1019", {"start": v(36.97, 40.41) * mm, "end": v(36.96, 40.4) * mm});
            skLineSegment(sketch, "E1020", {"start": v(36.96, 40.4) * mm, "end": v(36.92, 40.33) * mm});
            skLineSegment(sketch, "E1021", {"start": v(36.92, 40.33) * mm, "end": v(36.76, 40.1) * mm});
            skLineSegment(sketch, "E1022", {"start": v(36.76, 40.1) * mm, "end": v(36.51, 39.88) * mm});
            skLineSegment(sketch, "E1023", {"start": v(36.51, 39.88) * mm, "end": v(36.24, 39.73) * mm});
            skLineSegment(sketch, "E1024", {"start": v(36.24, 39.73) * mm, "end": v(35.96, 39.62) * mm});
            skLineSegment(sketch, "E1025", {"start": v(35.96, 39.62) * mm, "end": v(35.7, 39.56) * mm});
            skLineSegment(sketch, "E1026", {"start": v(35.7, 39.56) * mm, "end": v(35.48, 39.54) * mm});
            skLineSegment(sketch, "E1027", {"start": v(35.48, 39.54) * mm, "end": v(35.34, 39.53) * mm});
            skLineSegment(sketch, "E1028", {"start": v(35.34, 39.53) * mm, "end": v(35.28, 39.53) * mm});
            skLineSegment(sketch, "E1029", {"start": v(35.28, 39.53) * mm, "end": v(35.14, 39.53) * mm});
            skLineSegment(sketch, "E1030", {"start": v(35.14, 39.53) * mm, "end": v(34.75, 39.52) * mm});
            skLineSegment(sketch, "E1031", {"start": v(34.75, 39.52) * mm, "end": v(34.2, 39.52) * mm});
            skLineSegment(sketch, "E1032", {"start": v(34.2, 39.52) * mm, "end": v(33.54, 39.51) * mm});
            skLineSegment(sketch, "E1033", {"start": v(33.54, 39.51) * mm, "end": v(32.86, 39.51) * mm});
            skLineSegment(sketch, "E1034", {"start": v(32.86, 39.51) * mm, "end": v(32.23, 39.51) * mm});
            skLineSegment(sketch, "E1035", {"start": v(32.23, 39.51) * mm, "end": v(31.71, 39.52) * mm});
            skLineSegment(sketch, "E1036", {"start": v(31.71, 39.52) * mm, "end": v(31.47, 39.52) * mm});
            skLineSegment(sketch, "E1037", {"start": v(31.47, 39.52) * mm, "end": v(31.39, 39.53) * mm});
            skLineSegment(sketch, "E1038", {"start": v(31.39, 39.53) * mm, "end": v(31.34, 39.53) * mm});
            skLineSegment(sketch, "E1039", {"start": v(31.34, 39.53) * mm, "end": v(31.2, 39.56) * mm});
            skLineSegment(sketch, "E1040", {"start": v(31.2, 39.56) * mm, "end": v(31.07, 39.63) * mm});
            skLineSegment(sketch, "E1041", {"start": v(31.07, 39.63) * mm, "end": v(30.99, 39.73) * mm});
            skLineSegment(sketch, "E1042", {"start": v(30.99, 39.73) * mm, "end": v(30.94, 39.85) * mm});
            skLineSegment(sketch, "E1043", {"start": v(30.94, 39.85) * mm, "end": v(30.92, 39.98) * mm});
            skLineSegment(sketch, "E1044", {"start": v(30.92, 39.98) * mm, "end": v(30.93, 40.13) * mm});
            skLineSegment(sketch, "E1045", {"start": v(30.93, 40.13) * mm, "end": v(30.96, 40.27) * mm});
            skLineSegment(sketch, "E1046", {"start": v(30.96, 40.27) * mm, "end": v(31, 40.37) * mm});
            skLineSegment(sketch, "E1047", {"start": v(31, 40.37) * mm, "end": v(31.01, 40.4) * mm});
            skLineSegment(sketch, "E1048", {"start": v(31.01, 40.4) * mm, "end": v(31.07, 40.56) * mm});
            skLineSegment(sketch, "E1049", {"start": v(31.07, 40.56) * mm, "end": v(31.26, 41.03) * mm});
            skLineSegment(sketch, "E1050", {"start": v(31.26, 41.03) * mm, "end": v(31.5, 41.58) * mm});
            skLineSegment(sketch, "E1051", {"start": v(31.5, 41.58) * mm, "end": v(31.72, 42.1) * mm});
            skLineSegment(sketch, "E1052", {"start": v(31.72, 42.1) * mm, "end": v(31.88, 42.5) * mm});
            skLineSegment(sketch, "E1053", {"start": v(31.88, 42.5) * mm, "end": v(31.94, 42.64) * mm});
            skLineSegment(sketch, "E1054", {"start": v(31.94, 42.64) * mm, "end": v(31.99, 42.78) * mm});
            skLineSegment(sketch, "E1055", {"start": v(31.99, 42.78) * mm, "end": v(32.06, 43.2) * mm});
            skLineSegment(sketch, "E1056", {"start": v(32.06, 43.2) * mm, "end": v(32, 43.75) * mm});
            skLineSegment(sketch, "E1057", {"start": v(32, 43.75) * mm, "end": v(31.8, 44.3) * mm});
            skLineSegment(sketch, "E1058", {"start": v(31.8, 44.3) * mm, "end": v(31.53, 44.72) * mm});
            skLineSegment(sketch, "E1059", {"start": v(31.53, 44.72) * mm, "end": v(31.43, 44.86) * mm});
            skLineSegment(sketch, "E1060", {"start": v(31.43, 44.86) * mm, "end": v(31.38, 44.92) * mm});
            skLineSegment(sketch, "E1061", {"start": v(31.38, 44.92) * mm, "end": v(31.2, 45.1) * mm});
            skLineSegment(sketch, "E1062", {"start": v(31.2, 45.1) * mm, "end": v(30.96, 45.3) * mm});
            skLineSegment(sketch, "E1063", {"start": v(30.96, 45.3) * mm, "end": v(30.7, 45.44) * mm});
            skLineSegment(sketch, "E1064", {"start": v(30.7, 45.44) * mm, "end": v(30.46, 45.53) * mm});
            skLineSegment(sketch, "E1065", {"start": v(30.46, 45.53) * mm, "end": v(30.24, 45.59) * mm});
            skLineSegment(sketch, "E1066", {"start": v(30.24, 45.59) * mm, "end": v(30.06, 45.62) * mm});
            skLineSegment(sketch, "E1067", {"start": v(30.06, 45.62) * mm, "end": v(29.95, 45.63) * mm});
            skLineSegment(sketch, "E1068", {"start": v(29.95, 45.63) * mm, "end": v(29.9, 45.63) * mm});
            skLineSegment(sketch, "E1069", {"start": v(29.9, 45.63) * mm, "end": v(24.87, 45.63) * mm});
            skLineSegment(sketch, "E1070", {"start": v(24.87, 45.63) * mm, "end": v(22.13, 39.48) * mm});
            skLineSegment(sketch, "E1071", {"start": v(22.13, 39.48) * mm, "end": v(22.1, 39.48) * mm});
            skLineSegment(sketch, "E1072", {"start": v(22.1, 39.48) * mm, "end": v(22, 39.47) * mm});
            skLineSegment(sketch, "E1073", {"start": v(22, 39.47) * mm, "end": v(21.8, 39.47) * mm});
            skLineSegment(sketch, "E1074", {"start": v(21.8, 39.47) * mm, "end": v(21.54, 39.48) * mm});
            skLineSegment(sketch, "E1075", {"start": v(21.54, 39.48) * mm, "end": v(21.45, 39.48) * mm});
            skLineSegment(sketch, "E1076", {"start": v(21.45, 39.48) * mm, "end": v(21.4, 39.48) * mm});
            skLineSegment(sketch, "E1077", {"start": v(21.4, 39.48) * mm, "end": v(21.27, 39.5) * mm});
            skLineSegment(sketch, "E1078", {"start": v(21.27, 39.5) * mm, "end": v(21.15, 39.57) * mm});
            skLineSegment(sketch, "E1079", {"start": v(21.15, 39.57) * mm, "end": v(21.07, 39.67) * mm});
            skLineSegment(sketch, "E1080", {"start": v(21.07, 39.67) * mm, "end": v(21.03, 39.8) * mm});
            skLineSegment(sketch, "E1081", {"start": v(21.03, 39.8) * mm, "end": v(21.02, 39.93) * mm});
            skLineSegment(sketch, "E1082", {"start": v(21.02, 39.93) * mm, "end": v(21.04, 40.08) * mm});
            skLineSegment(sketch, "E1083", {"start": v(21.04, 40.08) * mm, "end": v(21.08, 40.22) * mm});
            skLineSegment(sketch, "E1084", {"start": v(21.08, 40.22) * mm, "end": v(21.11, 40.32) * mm});
            skLineSegment(sketch, "E1085", {"start": v(21.11, 40.32) * mm, "end": v(21.13, 40.36) * mm});
            skLineSegment(sketch, "E1086", {"start": v(21.13, 40.36) * mm, "end": v(21.17, 40.46) * mm});
            skLineSegment(sketch, "E1087", {"start": v(21.17, 40.46) * mm, "end": v(21.3, 40.75) * mm});
            skLineSegment(sketch, "E1088", {"start": v(21.3, 40.75) * mm, "end": v(21.47, 41.17) * mm});
            skLineSegment(sketch, "E1089", {"start": v(21.47, 41.17) * mm, "end": v(21.65, 41.6) * mm});
            skLineSegment(sketch, "E1090", {"start": v(21.65, 41.6) * mm, "end": v(21.84, 42.05) * mm});
            skLineSegment(sketch, "E1091", {"start": v(21.84, 42.05) * mm, "end": v(22.02, 42.49) * mm});
            skLineSegment(sketch, "E1092", {"start": v(22.02, 42.49) * mm, "end": v(22.2, 42.93) * mm});
            skLineSegment(sketch, "E1093", {"start": v(22.2, 42.93) * mm, "end": v(22.38, 43.35) * mm});
            skLineSegment(sketch, "E1094", {"start": v(22.38, 43.35) * mm, "end": v(22.55, 43.76) * mm});
            skLineSegment(sketch, "E1095", {"start": v(22.55, 43.76) * mm, "end": v(22.7, 44.15) * mm});
            skLineSegment(sketch, "E1096", {"start": v(22.7, 44.15) * mm, "end": v(22.85, 44.5) * mm});
            skLineSegment(sketch, "E1097", {"start": v(22.85, 44.5) * mm, "end": v(22.98, 44.82) * mm});
            skLineSegment(sketch, "E1098", {"start": v(22.98, 44.82) * mm, "end": v(23.1, 45.1) * mm});
            skLineSegment(sketch, "E1099", {"start": v(23.1, 45.1) * mm, "end": v(23.19, 45.32) * mm});
            skLineSegment(sketch, "E1100", {"start": v(23.19, 45.32) * mm, "end": v(23.26, 45.5) * mm});
            skLineSegment(sketch, "E1101", {"start": v(23.26, 45.5) * mm, "end": v(23.3, 45.6) * mm});
            skLineSegment(sketch, "E1102", {"start": v(23.3, 45.6) * mm, "end": v(23.32, 45.63) * mm});
            skLineSegment(sketch, "E1103", {"start": v(23.32, 45.63) * mm, "end": v(17.76, 45.63) * mm});
            skLineSegment(sketch, "E1104", {"start": v(17.76, 45.63) * mm, "end": v(17.7, 45.63) * mm});
            skLineSegment(sketch, "E1105", {"start": v(17.7, 45.63) * mm, "end": v(17.53, 45.62) * mm});
            skLineSegment(sketch, "E1106", {"start": v(17.53, 45.62) * mm, "end": v(17.3, 45.6) * mm});
            skLineSegment(sketch, "E1107", {"start": v(17.3, 45.6) * mm, "end": v(17, 45.57) * mm});
            skLineSegment(sketch, "E1108", {"start": v(17, 45.57) * mm, "end": v(16.68, 45.52) * mm});
            skLineSegment(sketch, "E1109", {"start": v(16.68, 45.52) * mm, "end": v(16.36, 45.46) * mm});
            skLineSegment(sketch, "E1110", {"start": v(16.36, 45.46) * mm, "end": v(16.06, 45.37) * mm});
            skLineSegment(sketch, "E1111", {"start": v(16.06, 45.37) * mm, "end": v(15.88, 45.3) * mm});
            skLineSegment(sketch, "E1112", {"start": v(15.88, 45.3) * mm, "end": v(15.82, 45.26) * mm});
            skLineSegment(sketch, "E1113", {"start": v(15.82, 45.26) * mm, "end": v(15.77, 45.22) * mm});
            skLineSegment(sketch, "E1114", {"start": v(15.77, 45.22) * mm, "end": v(15.6, 45.12) * mm});
            skLineSegment(sketch, "E1115", {"start": v(15.6, 45.12) * mm, "end": v(15.35, 44.97) * mm});
            skLineSegment(sketch, "E1116", {"start": v(15.35, 44.97) * mm, "end": v(15.09, 44.78) * mm});
            skLineSegment(sketch, "E1117", {"start": v(15.09, 44.78) * mm, "end": v(14.81, 44.55) * mm});
            skLineSegment(sketch, "E1118", {"start": v(14.81, 44.55) * mm, "end": v(14.53, 44.27) * mm});
            skLineSegment(sketch, "E1119", {"start": v(14.53, 44.27) * mm, "end": v(14.26, 43.93) * mm});
            skLineSegment(sketch, "E1120", {"start": v(14.26, 43.93) * mm, "end": v(14, 43.53) * mm});
            skLineSegment(sketch, "E1121", {"start": v(14, 43.53) * mm, "end": v(13.82, 43.17) * mm});
            skLineSegment(sketch, "E1122", {"start": v(13.82, 43.17) * mm, "end": v(13.76, 43.05) * mm});
            skLineSegment(sketch, "E1123", {"start": v(13.76, 43.05) * mm, "end": v(13.71, 42.93) * mm});
            skLineSegment(sketch, "E1124", {"start": v(13.71, 42.93) * mm, "end": v(13.57, 42.59) * mm});
            skLineSegment(sketch, "E1125", {"start": v(13.57, 42.59) * mm, "end": v(13.43, 42.24) * mm});
            skLineSegment(sketch, "E1126", {"start": v(13.43, 42.24) * mm, "end": v(13.33, 41.96) * mm});
            skLineSegment(sketch, "E1127", {"start": v(13.33, 41.96) * mm, "end": v(13.24, 41.73) * mm});
            skLineSegment(sketch, "E1128", {"start": v(13.24, 41.73) * mm, "end": v(13.16, 41.5) * mm});
            skLineSegment(sketch, "E1129", {"start": v(13.16, 41.5) * mm, "end": v(13.06, 41.26) * mm});
            skLineSegment(sketch, "E1130", {"start": v(13.06, 41.26) * mm, "end": v(12.94, 40.96) * mm});
            skLineSegment(sketch, "E1131", {"start": v(12.94, 40.96) * mm, "end": v(12.81, 40.67) * mm});
            skLineSegment(sketch, "E1132", {"start": v(12.81, 40.67) * mm, "end": v(12.77, 40.58) * mm});
            skLineSegment(sketch, "E1133", {"start": v(12.77, 40.58) * mm, "end": v(12.71, 40.45) * mm});
            skLineSegment(sketch, "E1134", {"start": v(12.71, 40.45) * mm, "end": v(12.6, 40.06) * mm});
            skLineSegment(sketch, "E1135", {"start": v(12.6, 40.06) * mm, "end": v(12.52, 39.48) * mm});
            skLineSegment(sketch, "E1136", {"start": v(12.52, 39.48) * mm, "end": v(12.56, 38.9) * mm});
            skLineSegment(sketch, "E1137", {"start": v(12.56, 38.9) * mm, "end": v(12.67, 38.48) * mm});
            skLineSegment(sketch, "E1138", {"start": v(12.67, 38.48) * mm, "end": v(12.73, 38.36) * mm});
            skLineSegment(sketch, "E1139", {"start": v(12.73, 38.36) * mm, "end": v(12.77, 38.3) * mm});
            skLineSegment(sketch, "E1140", {"start": v(12.77, 38.3) * mm, "end": v(12.86, 38.1) * mm});
            skLineSegment(sketch, "E1141", {"start": v(12.86, 38.1) * mm, "end": v(13, 37.85) * mm});
            skLineSegment(sketch, "E1142", {"start": v(13, 37.85) * mm, "end": v(13.17, 37.62) * mm});
            skLineSegment(sketch, "E1143", {"start": v(13.17, 37.62) * mm, "end": v(13.37, 37.42) * mm});
            skLineSegment(sketch, "E1144", {"start": v(13.37, 37.42) * mm, "end": v(13.62, 37.24) * mm});
            skLineSegment(sketch, "E1145", {"start": v(13.62, 37.24) * mm, "end": v(13.93, 37.1) * mm});
            skLineSegment(sketch, "E1146", {"start": v(13.93, 37.1) * mm, "end": v(14.31, 37.02) * mm});
            skLineSegment(sketch, "E1147", {"start": v(14.31, 37.02) * mm, "end": v(14.65, 36.99) * mm});
            skLineSegment(sketch, "E1148", {"start": v(14.65, 36.99) * mm, "end": v(14.77, 36.99) * mm});
            skLineSegment(sketch, "E1149", {"start": v(14.77, 36.99) * mm, "end": v(14.98, 36.99) * mm});
            skLineSegment(sketch, "E1150", {"start": v(14.98, 36.99) * mm, "end": v(15.6, 36.99) * mm});
            skLineSegment(sketch, "E1151", {"start": v(15.6, 36.99) * mm, "end": v(16.11, 36.99) * mm});
            skLineSegment(sketch, "E1152", {"start": v(16.11, 36.99) * mm, "end": v(16.38, 36.99) * mm});
            skLineSegment(sketch, "E1153", {"start": v(16.38, 36.99) * mm, "end": v(16.45, 36.99) * mm});
            skLineSegment(sketch, "E1154", {"start": v(16.45, 36.99) * mm, "end": v(16.49, 37) * mm});
            skLineSegment(sketch, "E1155", {"start": v(16.49, 37) * mm, "end": v(16.58, 37.02) * mm});
            skLineSegment(sketch, "E1156", {"start": v(16.58, 37.02) * mm, "end": v(16.73, 37.05) * mm});
            skLineSegment(sketch, "E1157", {"start": v(16.73, 37.05) * mm, "end": v(16.9, 37.11) * mm});
            skLineSegment(sketch, "E1158", {"start": v(16.9, 37.11) * mm, "end": v(17.1, 37.2) * mm});
            skLineSegment(sketch, "E1159", {"start": v(17.1, 37.2) * mm, "end": v(17.3, 37.32) * mm});
            skLineSegment(sketch, "E1160", {"start": v(17.3, 37.32) * mm, "end": v(17.5, 37.48) * mm});
            skLineSegment(sketch, "E1161", {"start": v(17.5, 37.48) * mm, "end": v(17.62, 37.62) * mm});
            skLineSegment(sketch, "E1162", {"start": v(17.62, 37.62) * mm, "end": v(17.66, 37.67) * mm});
            skLineSegment(sketch, "E1163", {"start": v(17.66, 37.67) * mm, "end": v(17.73, 37.76) * mm});
            skLineSegment(sketch, "E1164", {"start": v(17.73, 37.76) * mm, "end": v(17.93, 38.05) * mm});
            skLineSegment(sketch, "E1165", {"start": v(17.93, 38.05) * mm, "end": v(18.14, 38.35) * mm});
            skLineSegment(sketch, "E1166", {"start": v(18.14, 38.35) * mm, "end": v(18.27, 38.53) * mm});
            skLineSegment(sketch, "E1167", {"start": v(18.27, 38.53) * mm, "end": v(18.31, 38.6) * mm});
            skLineSegment(sketch, "E1168", {"start": v(18.31, 38.6) * mm, "end": v(18.32, 38.56) * mm});
            skLineSegment(sketch, "E1169", {"start": v(18.32, 38.56) * mm, "end": v(18.36, 38.48) * mm});
            skLineSegment(sketch, "E1170", {"start": v(18.36, 38.48) * mm, "end": v(18.43, 38.34) * mm});
            skLineSegment(sketch, "E1171", {"start": v(18.43, 38.34) * mm, "end": v(18.52, 38.18) * mm});
            skLineSegment(sketch, "E1172", {"start": v(18.52, 38.18) * mm, "end": v(18.65, 38) * mm});
            skLineSegment(sketch, "E1173", {"start": v(18.65, 38) * mm, "end": v(18.81, 37.8) * mm});
            skLineSegment(sketch, "E1174", {"start": v(18.81, 37.8) * mm, "end": v(19.01, 37.63) * mm});
            skLineSegment(sketch, "E1175", {"start": v(19.01, 37.63) * mm, "end": v(19.19, 37.5) * mm});
            skLineSegment(sketch, "E1176", {"start": v(19.19, 37.5) * mm, "end": v(19.25, 37.46) * mm});
            skLineSegment(sketch, "E1177", {"start": v(19.25, 37.46) * mm, "end": v(19.36, 37.4) * mm});
            skLineSegment(sketch, "E1178", {"start": v(19.36, 37.4) * mm, "end": v(19.7, 37.21) * mm});
            skLineSegment(sketch, "E1179", {"start": v(19.7, 37.21) * mm, "end": v(20.04, 37.07) * mm});
            skLineSegment(sketch, "E1180", {"start": v(20.04, 37.07) * mm, "end": v(20.37, 37) * mm});
            skLineSegment(sketch, "E1181", {"start": v(20.37, 37) * mm, "end": v(20.64, 37) * mm});
            skLineSegment(sketch, "E1182", {"start": v(20.64, 37) * mm, "end": v(20.73, 36.99) * mm});
            skLineSegment(sketch, "E1183", {"start": v(20.73, 36.99) * mm, "end": v(20.8, 36.99) * mm});
            skLineSegment(sketch, "E1184", {"start": v(20.8, 36.99) * mm, "end": v(21.02, 36.99) * mm});
            skLineSegment(sketch, "E1185", {"start": v(21.02, 36.99) * mm, "end": v(21.46, 36.99) * mm});
            skLineSegment(sketch, "E1186", {"start": v(21.46, 36.99) * mm, "end": v(21.99, 36.99) * mm});
            skLineSegment(sketch, "E1187", {"start": v(21.99, 36.99) * mm, "end": v(22.55, 36.99) * mm});
            skLineSegment(sketch, "E1188", {"start": v(22.55, 36.99) * mm, "end": v(23.08, 36.99) * mm});
            skLineSegment(sketch, "E1189", {"start": v(23.08, 36.99) * mm, "end": v(23.54, 36.99) * mm});
            skLineSegment(sketch, "E1190", {"start": v(23.54, 36.99) * mm, "end": v(23.85, 36.99) * mm});
            skLineSegment(sketch, "E1191", {"start": v(23.85, 36.99) * mm, "end": v(23.97, 36.99) * mm});
            skLineSegment(sketch, "E1192", {"start": v(23.97, 36.99) * mm, "end": v(26.63, 43.05) * mm});
            skLineSegment(sketch, "E1193", {"start": v(26.63, 43.05) * mm, "end": v(28.87, 43.05) * mm});
            skLineSegment(sketch, "E1194", {"start": v(28.87, 43.05) * mm, "end": v(28.89, 43.04) * mm});
            skLineSegment(sketch, "E1195", {"start": v(28.89, 43.04) * mm, "end": v(28.93, 43.03) * mm});
            skLineSegment(sketch, "E1196", {"start": v(28.93, 43.03) * mm, "end": v(28.98, 43) * mm});
            skLineSegment(sketch, "E1197", {"start": v(28.98, 43) * mm, "end": v(29.03, 42.96) * mm});
            skLineSegment(sketch, "E1198", {"start": v(29.03, 42.96) * mm, "end": v(29.08, 42.9) * mm});
            skLineSegment(sketch, "E1199", {"start": v(29.08, 42.9) * mm, "end": v(29.1, 42.8) * mm});
            skLineSegment(sketch, "E1200", {"start": v(29.1, 42.8) * mm, "end": v(29.1, 42.68) * mm});
            skLineSegment(sketch, "E1201", {"start": v(29.1, 42.68) * mm, "end": v(29.06, 42.56) * mm});
            skLineSegment(sketch, "E1202", {"start": v(29.06, 42.56) * mm, "end": v(29.05, 42.52) * mm});
            skLineSegment(sketch, "E1203", {"start": v(29.05, 42.52) * mm, "end": v(29.02, 42.46) * mm});
            skLineSegment(sketch, "E1204", {"start": v(29.02, 42.46) * mm, "end": v(28.95, 42.3) * mm});
            skLineSegment(sketch, "E1205", {"start": v(28.95, 42.3) * mm, "end": v(28.82, 42) * mm});
            skLineSegment(sketch, "E1206", {"start": v(28.82, 42) * mm, "end": v(28.67, 41.65) * mm});
            skLineSegment(sketch, "E1207", {"start": v(28.67, 41.65) * mm, "end": v(28.52, 41.3) * mm});
            skLineSegment(sketch, "E1208", {"start": v(28.52, 41.3) * mm, "end": v(28.38, 40.98) * mm});
            skLineSegment(sketch, "E1209", {"start": v(28.38, 40.98) * mm, "end": v(28.26, 40.71) * mm});
            skLineSegment(sketch, "E1210", {"start": v(28.26, 40.71) * mm, "end": v(28.17, 40.53) * mm});
            skLineSegment(sketch, "E1211", {"start": v(28.17, 40.53) * mm, "end": v(28.14, 40.46) * mm});
            skLineSegment(sketch, "E1212", {"start": v(28.14, 40.46) * mm, "end": v(28.13, 40.4) * mm});
            skLineSegment(sketch, "E1213", {"start": v(28.13, 40.4) * mm, "end": v(28.09, 40.28) * mm});
            skLineSegment(sketch, "E1214", {"start": v(28.09, 40.28) * mm, "end": v(28.04, 40.07) * mm});
            skLineSegment(sketch, "E1215", {"start": v(28.04, 40.07) * mm, "end": v(28, 39.8) * mm});
            skLineSegment(sketch, "E1216", {"start": v(28, 39.8) * mm, "end": v(28, 39.5) * mm});
            skLineSegment(sketch, "E1217", {"start": v(28, 39.5) * mm, "end": v(28.02, 39.17) * mm});
            skLineSegment(sketch, "E1218", {"start": v(28.02, 39.17) * mm, "end": v(28.1, 38.83) * mm});
            skLineSegment(sketch, "E1219", {"start": v(28.1, 38.83) * mm, "end": v(28.2, 38.57) * mm});
            skLineSegment(sketch, "E1220", {"start": v(28.2, 38.57) * mm, "end": v(28.25, 38.49) * mm});
            skLineSegment(sketch, "E1221", {"start": v(28.25, 38.49) * mm, "end": v(28.3, 38.4) * mm});
            skLineSegment(sketch, "E1222", {"start": v(28.3, 38.4) * mm, "end": v(28.46, 38.17) * mm});
            skLineSegment(sketch, "E1223", {"start": v(28.46, 38.17) * mm, "end": v(28.72, 37.88) * mm});
            skLineSegment(sketch, "E1224", {"start": v(28.72, 37.88) * mm, "end": v(29.03, 37.62) * mm});
            skLineSegment(sketch, "E1225", {"start": v(29.03, 37.62) * mm, "end": v(29.4, 37.4) * mm});
            skLineSegment(sketch, "E1226", {"start": v(29.4, 37.4) * mm, "end": v(29.83, 37.23) * mm});
            skLineSegment(sketch, "E1227", {"start": v(29.83, 37.23) * mm, "end": v(30.33, 37.1) * mm});
            skLineSegment(sketch, "E1228", {"start": v(30.33, 37.1) * mm, "end": v(30.9, 37.02) * mm});
            skLineSegment(sketch, "E1229", {"start": v(30.9, 37.02) * mm, "end": v(31.4, 36.99) * mm});
            skLineSegment(sketch, "E1230", {"start": v(31.4, 36.99) * mm, "end": v(31.56, 37) * mm});
            skLineSegment(sketch, "E1231", {"start": v(31.56, 37) * mm, "end": v(31.82, 37) * mm});
            skLineSegment(sketch, "E1232", {"start": v(31.82, 37) * mm, "end": v(32.6, 37) * mm});
            skLineSegment(sketch, "E1233", {"start": v(32.6, 37) * mm, "end": v(33.6, 36.99) * mm});
            skLineSegment(sketch, "E1234", {"start": v(33.6, 36.99) * mm, "end": v(34.46, 36.99) * mm});
            skLineSegment(sketch, "E1235", {"start": v(34.46, 36.99) * mm, "end": v(34.95, 36.99) * mm});
            skLineSegment(sketch, "E1236", {"start": v(34.95, 36.99) * mm, "end": v(35.1, 36.99) * mm});
            skLineSegment(sketch, "E1237", {"start": v(11.43, 42.1) * mm, "end": v(11.45, 42.14) * mm});
            skLineSegment(sketch, "E1238", {"start": v(11.45, 42.14) * mm, "end": v(11.51, 42.26) * mm});
            skLineSegment(sketch, "E1239", {"start": v(11.51, 42.26) * mm, "end": v(11.61, 42.43) * mm});
            skLineSegment(sketch, "E1240", {"start": v(11.61, 42.43) * mm, "end": v(11.75, 42.63) * mm});
            skLineSegment(sketch, "E1241", {"start": v(11.75, 42.63) * mm, "end": v(11.92, 42.83) * mm});
            skLineSegment(sketch, "E1242", {"start": v(11.92, 42.83) * mm, "end": v(12.11, 43) * mm});
            skLineSegment(sketch, "E1243", {"start": v(12.11, 43) * mm, "end": v(12.34, 43.13) * mm});
            skLineSegment(sketch, "E1244", {"start": v(12.34, 43.13) * mm, "end": v(12.52, 43.17) * mm});
            skLineSegment(sketch, "E1245", {"start": v(12.52, 43.17) * mm, "end": v(12.58, 43.17) * mm});
            skLineSegment(sketch, "E1246", {"start": v(12.58, 43.17) * mm, "end": v(12.7, 43.17) * mm});
            skLineSegment(sketch, "E1247", {"start": v(12.7, 43.17) * mm, "end": v(13.03, 43.17) * mm});
            skLineSegment(sketch, "E1248", {"start": v(13.03, 43.17) * mm, "end": v(13.34, 43.17) * mm});
            skLineSegment(sketch, "E1249", {"start": v(13.34, 43.17) * mm, "end": v(13.53, 43.17) * mm});
            skLineSegment(sketch, "E1250", {"start": v(13.53, 43.17) * mm, "end": v(13.59, 43.17) * mm});
            skLineSegment(sketch, "E1251", {"start": v(13.59, 43.17) * mm, "end": v(14.7, 45.63) * mm});
            skLineSegment(sketch, "E1252", {"start": v(14.7, 45.63) * mm, "end": v(12.8, 45.63) * mm});
            skLineSegment(sketch, "E1253", {"start": v(12.8, 45.63) * mm, "end": v(12.75, 45.63) * mm});
            skLineSegment(sketch, "E1254", {"start": v(12.75, 45.63) * mm, "end": v(12.63, 45.64) * mm});
            skLineSegment(sketch, "E1255", {"start": v(12.63, 45.64) * mm, "end": v(12.46, 45.65) * mm});
            skLineSegment(sketch, "E1256", {"start": v(12.46, 45.65) * mm, "end": v(12.23, 45.64) * mm});
            skLineSegment(sketch, "E1257", {"start": v(12.23, 45.64) * mm, "end": v(11.98, 45.63) * mm});
            skLineSegment(sketch, "E1258", {"start": v(11.98, 45.63) * mm, "end": v(11.72, 45.59) * mm});
            skLineSegment(sketch, "E1259", {"start": v(11.72, 45.59) * mm, "end": v(11.45, 45.52) * mm});
            skLineSegment(sketch, "E1260", {"start": v(11.45, 45.52) * mm, "end": v(11.27, 45.46) * mm});
            skLineSegment(sketch, "E1261", {"start": v(11.27, 45.46) * mm, "end": v(11.2, 45.43) * mm});
            skLineSegment(sketch, "E1262", {"start": v(11.2, 45.43) * mm, "end": v(11.14, 45.4) * mm});
            skLineSegment(sketch, "E1263", {"start": v(11.14, 45.4) * mm, "end": v(10.96, 45.3) * mm});
            skLineSegment(sketch, "E1264", {"start": v(10.96, 45.3) * mm, "end": v(10.68, 45.15) * mm});
            skLineSegment(sketch, "E1265", {"start": v(10.68, 45.15) * mm, "end": v(10.38, 44.96) * mm});
            skLineSegment(sketch, "E1266", {"start": v(10.38, 44.96) * mm, "end": v(10.07, 44.71) * mm});
            skLineSegment(sketch, "E1267", {"start": v(10.07, 44.71) * mm, "end": v(9.75, 44.4) * mm});
            skLineSegment(sketch, "E1268", {"start": v(9.75, 44.4) * mm, "end": v(9.44, 44.03) * mm});
            skLineSegment(sketch, "E1269", {"start": v(9.44, 44.03) * mm, "end": v(9.14, 43.56) * mm});
            skLineSegment(sketch, "E1270", {"start": v(9.14, 43.56) * mm, "end": v(8.93, 43.14) * mm});
            skLineSegment(sketch, "E1271", {"start": v(8.93, 43.14) * mm, "end": v(8.86, 43) * mm});
            skLineSegment(sketch, "E1272", {"start": v(8.86, 43) * mm, "end": v(8.79, 42.82) * mm});
            skLineSegment(sketch, "E1273", {"start": v(8.79, 42.82) * mm, "end": v(8.56, 42.29) * mm});
            skLineSegment(sketch, "E1274", {"start": v(8.56, 42.29) * mm, "end": v(8.28, 41.63) * mm});
            skLineSegment(sketch, "E1275", {"start": v(8.28, 41.63) * mm, "end": v(8.03, 41.03) * mm});
            skLineSegment(sketch, "E1276", {"start": v(8.03, 41.03) * mm, "end": v(7.82, 40.5) * mm});
            skLineSegment(sketch, "E1277", {"start": v(7.82, 40.5) * mm, "end": v(7.64, 40.08) * mm});
            skLineSegment(sketch, "E1278", {"start": v(7.64, 40.08) * mm, "end": v(7.5, 39.75) * mm});
            skLineSegment(sketch, "E1279", {"start": v(7.5, 39.75) * mm, "end": v(7.42, 39.54) * mm});
            skLineSegment(sketch, "E1280", {"start": v(7.42, 39.54) * mm, "end": v(7.39, 39.47) * mm});
            skLineSegment(sketch, "E1281", {"start": v(7.39, 39.47) * mm, "end": v(5.45, 39.47) * mm});
            skLineSegment(sketch, "E1282", {"start": v(5.45, 39.47) * mm, "end": v(5.42, 39.48) * mm});
            skLineSegment(sketch, "E1283", {"start": v(5.42, 39.48) * mm, "end": v(5.32, 39.5) * mm});
            skLineSegment(sketch, "E1284", {"start": v(5.32, 39.5) * mm, "end": v(5.2, 39.54) * mm});
            skLineSegment(sketch, "E1285", {"start": v(5.2, 39.54) * mm, "end": v(5.07, 39.6) * mm});
            skLineSegment(sketch, "E1286", {"start": v(5.07, 39.6) * mm, "end": v(4.94, 39.69) * mm});
            skLineSegment(sketch, "E1287", {"start": v(4.94, 39.69) * mm, "end": v(4.85, 39.8) * mm});
            skLineSegment(sketch, "E1288", {"start": v(4.85, 39.8) * mm, "end": v(4.82, 39.95) * mm});
            skLineSegment(sketch, "E1289", {"start": v(4.82, 39.95) * mm, "end": v(4.85, 40.09) * mm});
            skLineSegment(sketch, "E1290", {"start": v(4.85, 40.09) * mm, "end": v(4.87, 40.13) * mm});
            skLineSegment(sketch, "E1291", {"start": v(4.87, 40.13) * mm, "end": v(4.9, 40.19) * mm});
            skLineSegment(sketch, "E1292", {"start": v(4.9, 40.19) * mm, "end": v(4.96, 40.35) * mm});
            skLineSegment(sketch, "E1293", {"start": v(4.96, 40.35) * mm, "end": v(5.13, 40.73) * mm});
            skLineSegment(sketch, "E1294", {"start": v(5.13, 40.73) * mm, "end": v(5.33, 41.2) * mm});
            skLineSegment(sketch, "E1295", {"start": v(5.33, 41.2) * mm, "end": v(5.55, 41.71) * mm});
            skLineSegment(sketch, "E1296", {"start": v(5.55, 41.71) * mm, "end": v(5.76, 42.2) * mm});
            skLineSegment(sketch, "E1297", {"start": v(5.76, 42.2) * mm, "end": v(5.94, 42.63) * mm});
            skLineSegment(sketch, "E1298", {"start": v(5.94, 42.63) * mm, "end": v(6.06, 42.93) * mm});
            skLineSegment(sketch, "E1299", {"start": v(6.06, 42.93) * mm, "end": v(6.1, 43.04) * mm});
            skLineSegment(sketch, "E1300", {"start": v(6.1, 43.04) * mm, "end": v(8.77, 43.04) * mm});
            skLineSegment(sketch, "E1301", {"start": v(8.77, 43.04) * mm, "end": v(9.7, 45.63) * mm});
            skLineSegment(sketch, "E1302", {"start": v(9.7, 45.63) * mm, "end": v(7.23, 45.63) * mm});
            skLineSegment(sketch, "E1303", {"start": v(7.23, 45.63) * mm, "end": v(8.69, 49.18) * mm});
            skLineSegment(sketch, "E1304", {"start": v(8.69, 49.18) * mm, "end": v(5.77, 49.18) * mm});
            skLineSegment(sketch, "E1305", {"start": v(5.77, 49.18) * mm, "end": v(4.24, 45.63) * mm});
            skLineSegment(sketch, "E1306", {"start": v(4.24, 45.63) * mm, "end": v(3.06, 45.63) * mm});
            skLineSegment(sketch, "E1307", {"start": v(3.06, 45.63) * mm, "end": v(1.98, 43.07) * mm});
            skLineSegment(sketch, "E1308", {"start": v(1.98, 43.07) * mm, "end": v(3.26, 43.07) * mm});
            skLineSegment(sketch, "E1309", {"start": v(3.26, 43.07) * mm, "end": v(2.2, 40.68) * mm});
            skLineSegment(sketch, "E1310", {"start": v(2.2, 40.68) * mm, "end": v(2.18, 40.65) * mm});
            skLineSegment(sketch, "E1311", {"start": v(2.18, 40.65) * mm, "end": v(2.14, 40.55) * mm});
            skLineSegment(sketch, "E1312", {"start": v(2.14, 40.55) * mm, "end": v(2.08, 40.4) * mm});
            skLineSegment(sketch, "E1313", {"start": v(2.08, 40.4) * mm, "end": v(2.03, 40.19) * mm});
            skLineSegment(sketch, "E1314", {"start": v(2.03, 40.19) * mm, "end": v(1.98, 39.95) * mm});
            skLineSegment(sketch, "E1315", {"start": v(1.98, 39.95) * mm, "end": v(1.96, 39.68) * mm});
            skLineSegment(sketch, "E1316", {"start": v(1.96, 39.68) * mm, "end": v(1.97, 39.4) * mm});
            skLineSegment(sketch, "E1317", {"start": v(1.97, 39.4) * mm, "end": v(2, 39.17) * mm});
            skLineSegment(sketch, "E1318", {"start": v(2, 39.17) * mm, "end": v(2.03, 39.1) * mm});
            skLineSegment(sketch, "E1319", {"start": v(2.03, 39.1) * mm, "end": v(2.05, 39.02) * mm});
            skLineSegment(sketch, "E1320", {"start": v(2.05, 39.02) * mm, "end": v(2.13, 38.78) * mm});
            skLineSegment(sketch, "E1321", {"start": v(2.13, 38.78) * mm, "end": v(2.29, 38.44) * mm});
            skLineSegment(sketch, "E1322", {"start": v(2.29, 38.44) * mm, "end": v(2.5, 38.08) * mm});
            skLineSegment(sketch, "E1323", {"start": v(2.5, 38.08) * mm, "end": v(2.76, 37.74) * mm});
            skLineSegment(sketch, "E1324", {"start": v(2.76, 37.74) * mm, "end": v(3.08, 37.44) * mm});
            skLineSegment(sketch, "E1325", {"start": v(3.08, 37.44) * mm, "end": v(3.48, 37.2) * mm});
            skLineSegment(sketch, "E1326", {"start": v(3.48, 37.2) * mm, "end": v(3.96, 37.04) * mm});
            skLineSegment(sketch, "E1327", {"start": v(3.96, 37.04) * mm, "end": v(4.38, 36.98) * mm});
            skLineSegment(sketch, "E1328", {"start": v(4.38, 36.98) * mm, "end": v(4.52, 36.98) * mm});
            skLineSegment(sketch, "E1329", {"start": v(4.52, 36.98) * mm, "end": v(9.22, 36.98) * mm});
            skLineSegment(sketch, "E1330", {"start": v(9.22, 36.98) * mm, "end": v(11.43, 42.1) * mm});
            skLineSegment(sketch, "E1331", {"start": v(-3.6, 39.48) * mm, "end": v(-3.66, 39.48) * mm});
            skLineSegment(sketch, "E1332", {"start": v(-3.66, 39.48) * mm, "end": v(-3.8, 39.5) * mm});
            skLineSegment(sketch, "E1333", {"start": v(-3.8, 39.5) * mm, "end": v(-3.92, 39.57) * mm});
            skLineSegment(sketch, "E1334", {"start": v(-3.92, 39.57) * mm, "end": v(-4, 39.67) * mm});
            skLineSegment(sketch, "E1335", {"start": v(-4, 39.67) * mm, "end": v(-4.05, 39.8) * mm});
            skLineSegment(sketch, "E1336", {"start": v(-4.05, 39.8) * mm, "end": v(-4.06, 39.94) * mm});
            skLineSegment(sketch, "E1337", {"start": v(-4.06, 39.94) * mm, "end": v(-4.04, 40.08) * mm});
            skLineSegment(sketch, "E1338", {"start": v(-4.04, 40.08) * mm, "end": v(-4, 40.22) * mm});
            skLineSegment(sketch, "E1339", {"start": v(-4, 40.22) * mm, "end": v(-3.96, 40.32) * mm});
            skLineSegment(sketch, "E1340", {"start": v(-3.96, 40.32) * mm, "end": v(-3.94, 40.36) * mm});
            skLineSegment(sketch, "E1341", {"start": v(-3.94, 40.36) * mm, "end": v(-3.9, 40.45) * mm});
            skLineSegment(sketch, "E1342", {"start": v(-3.9, 40.45) * mm, "end": v(-3.75, 40.75) * mm});
            skLineSegment(sketch, "E1343", {"start": v(-3.75, 40.75) * mm, "end": v(-3.56, 41.16) * mm});
            skLineSegment(sketch, "E1344", {"start": v(-3.56, 41.16) * mm, "end": v(-3.35, 41.6) * mm});
            skLineSegment(sketch, "E1345", {"start": v(-3.35, 41.6) * mm, "end": v(-3.15, 42.04) * mm});
            skLineSegment(sketch, "E1346", {"start": v(-3.15, 42.04) * mm, "end": v(-2.95, 42.48) * mm});
            skLineSegment(sketch, "E1347", {"start": v(-2.95, 42.48) * mm, "end": v(-2.75, 42.92) * mm});
            skLineSegment(sketch, "E1348", {"start": v(-2.75, 42.92) * mm, "end": v(-2.56, 43.34) * mm});
            skLineSegment(sketch, "E1349", {"start": v(-2.56, 43.34) * mm, "end": v(-2.38, 43.76) * mm});
            skLineSegment(sketch, "E1350", {"start": v(-2.38, 43.76) * mm, "end": v(-2.21, 44.14) * mm});
            skLineSegment(sketch, "E1351", {"start": v(-2.21, 44.14) * mm, "end": v(-2.06, 44.5) * mm});
            skLineSegment(sketch, "E1352", {"start": v(-2.06, 44.5) * mm, "end": v(-1.92, 44.82) * mm});
            skLineSegment(sketch, "E1353", {"start": v(-1.92, 44.82) * mm, "end": v(-1.8, 45.1) * mm});
            skLineSegment(sketch, "E1354", {"start": v(-1.8, 45.1) * mm, "end": v(-1.7, 45.32) * mm});
            skLineSegment(sketch, "E1355", {"start": v(-1.7, 45.32) * mm, "end": v(-1.63, 45.5) * mm});
            skLineSegment(sketch, "E1356", {"start": v(-1.63, 45.5) * mm, "end": v(-1.58, 45.6) * mm});
            skLineSegment(sketch, "E1357", {"start": v(-1.58, 45.6) * mm, "end": v(-1.57, 45.63) * mm});
            skLineSegment(sketch, "E1358", {"start": v(-1.57, 45.63) * mm, "end": v(-7.31, 45.63) * mm});
            skLineSegment(sketch, "E1359", {"start": v(-7.31, 45.63) * mm, "end": v(-7.37, 45.63) * mm});
            skLineSegment(sketch, "E1360", {"start": v(-7.37, 45.63) * mm, "end": v(-7.54, 45.62) * mm});
            skLineSegment(sketch, "E1361", {"start": v(-7.54, 45.62) * mm, "end": v(-7.78, 45.6) * mm});
            skLineSegment(sketch, "E1362", {"start": v(-7.78, 45.6) * mm, "end": v(-8.08, 45.57) * mm});
            skLineSegment(sketch, "E1363", {"start": v(-8.08, 45.57) * mm, "end": v(-8.4, 45.52) * mm});
            skLineSegment(sketch, "E1364", {"start": v(-8.4, 45.52) * mm, "end": v(-8.72, 45.46) * mm});
            skLineSegment(sketch, "E1365", {"start": v(-8.72, 45.46) * mm, "end": v(-9, 45.37) * mm});
            skLineSegment(sketch, "E1366", {"start": v(-9, 45.37) * mm, "end": v(-9.2, 45.3) * mm});
            skLineSegment(sketch, "E1367", {"start": v(-9.2, 45.3) * mm, "end": v(-9.25, 45.26) * mm});
            skLineSegment(sketch, "E1368", {"start": v(-9.25, 45.26) * mm, "end": v(-9.3, 45.22) * mm});
            skLineSegment(sketch, "E1369", {"start": v(-9.3, 45.22) * mm, "end": v(-9.47, 45.12) * mm});
            skLineSegment(sketch, "E1370", {"start": v(-9.47, 45.12) * mm, "end": v(-9.72, 44.97) * mm});
            skLineSegment(sketch, "E1371", {"start": v(-9.72, 44.97) * mm, "end": v(-9.98, 44.78) * mm});
            skLineSegment(sketch, "E1372", {"start": v(-9.98, 44.78) * mm, "end": v(-10.26, 44.55) * mm});
            skLineSegment(sketch, "E1373", {"start": v(-10.26, 44.55) * mm, "end": v(-10.54, 44.27) * mm});
            skLineSegment(sketch, "E1374", {"start": v(-10.54, 44.27) * mm, "end": v(-10.81, 43.93) * mm});
            skLineSegment(sketch, "E1375", {"start": v(-10.81, 43.93) * mm, "end": v(-11.07, 43.53) * mm});
            skLineSegment(sketch, "E1376", {"start": v(-11.07, 43.53) * mm, "end": v(-11.26, 43.17) * mm});
            skLineSegment(sketch, "E1377", {"start": v(-11.26, 43.17) * mm, "end": v(-11.3, 43.04) * mm});
            skLineSegment(sketch, "E1378", {"start": v(-11.3, 43.04) * mm, "end": v(-11.36, 42.93) * mm});
            skLineSegment(sketch, "E1379", {"start": v(-11.36, 42.93) * mm, "end": v(-11.5, 42.59) * mm});
            skLineSegment(sketch, "E1380", {"start": v(-11.5, 42.59) * mm, "end": v(-11.64, 42.24) * mm});
            skLineSegment(sketch, "E1381", {"start": v(-11.64, 42.24) * mm, "end": v(-11.75, 41.96) * mm});
            skLineSegment(sketch, "E1382", {"start": v(-11.75, 41.96) * mm, "end": v(-11.83, 41.73) * mm});
            skLineSegment(sketch, "E1383", {"start": v(-11.83, 41.73) * mm, "end": v(-11.91, 41.5) * mm});
            skLineSegment(sketch, "E1384", {"start": v(-11.91, 41.5) * mm, "end": v(-12, 41.26) * mm});
            skLineSegment(sketch, "E1385", {"start": v(-12, 41.26) * mm, "end": v(-12.13, 40.96) * mm});
            skLineSegment(sketch, "E1386", {"start": v(-12.13, 40.96) * mm, "end": v(-12.26, 40.67) * mm});
            skLineSegment(sketch, "E1387", {"start": v(-12.26, 40.67) * mm, "end": v(-12.3, 40.58) * mm});
            skLineSegment(sketch, "E1388", {"start": v(-12.3, 40.58) * mm, "end": v(-12.34, 40.5) * mm});
            skLineSegment(sketch, "E1389", {"start": v(-12.34, 40.5) * mm, "end": v(-12.46, 40.06) * mm});
            skLineSegment(sketch, "E1390", {"start": v(-12.46, 40.06) * mm, "end": v(-12.52, 39.6) * mm});
            skLineSegment(sketch, "E1391", {"start": v(-12.52, 39.6) * mm, "end": v(-12.52, 39.5) * mm});
            skLineSegment(sketch, "E1392", {"start": v(-12.52, 39.5) * mm, "end": v(-14.73, 39.48) * mm});
            skLineSegment(sketch, "E1393", {"start": v(-14.73, 39.48) * mm, "end": v(-14.77, 39.47) * mm});
            skLineSegment(sketch, "E1394", {"start": v(-14.77, 39.47) * mm, "end": v(-14.95, 39.5) * mm});
            skLineSegment(sketch, "E1395", {"start": v(-14.95, 39.5) * mm, "end": v(-15.12, 39.58) * mm});
            skLineSegment(sketch, "E1396", {"start": v(-15.12, 39.58) * mm, "end": v(-15.15, 39.6) * mm});
            skLineSegment(sketch, "E1397", {"start": v(-15.15, 39.6) * mm, "end": v(-15.18, 39.64) * mm});
            skLineSegment(sketch, "E1398", {"start": v(-15.18, 39.64) * mm, "end": v(-15.26, 39.74) * mm});
            skLineSegment(sketch, "E1399", {"start": v(-15.26, 39.74) * mm, "end": v(-15.32, 39.88) * mm});
            skLineSegment(sketch, "E1400", {"start": v(-15.32, 39.88) * mm, "end": v(-15.33, 40.04) * mm});
            skLineSegment(sketch, "E1401", {"start": v(-15.33, 40.04) * mm, "end": v(-15.31, 40.18) * mm});
            skLineSegment(sketch, "E1402", {"start": v(-15.31, 40.18) * mm, "end": v(-15.3, 40.23) * mm});
            skLineSegment(sketch, "E1403", {"start": v(-15.3, 40.23) * mm, "end": v(-15.28, 40.31) * mm});
            skLineSegment(sketch, "E1404", {"start": v(-15.28, 40.31) * mm, "end": v(-15.18, 40.7) * mm});
            skLineSegment(sketch, "E1405", {"start": v(-15.18, 40.7) * mm, "end": v(-15.05, 41.06) * mm});
            skLineSegment(sketch, "E1406", {"start": v(-15.05, 41.06) * mm, "end": v(-15.01, 41.15) * mm});
            skLineSegment(sketch, "E1407", {"start": v(-15.01, 41.15) * mm, "end": v(-14.95, 41.3) * mm});
            skLineSegment(sketch, "E1408", {"start": v(-14.95, 41.3) * mm, "end": v(-14.76, 41.75) * mm});
            skLineSegment(sketch, "E1409", {"start": v(-14.76, 41.75) * mm, "end": v(-14.54, 42.3) * mm});
            skLineSegment(sketch, "E1410", {"start": v(-14.54, 42.3) * mm, "end": v(-14.32, 42.81) * mm});
            skLineSegment(sketch, "E1411", {"start": v(-14.32, 42.81) * mm, "end": v(-14.12, 43.3) * mm});
            skLineSegment(sketch, "E1412", {"start": v(-14.12, 43.3) * mm, "end": v(-13.9, 43.8) * mm});
            skLineSegment(sketch, "E1413", {"start": v(-13.9, 43.8) * mm, "end": v(-13.7, 44.3) * mm});
            skLineSegment(sketch, "E1414", {"start": v(-13.7, 44.3) * mm, "end": v(-13.45, 44.83) * mm});
            skLineSegment(sketch, "E1415", {"start": v(-13.45, 44.83) * mm, "end": v(-13.26, 45.27) * mm});
            skLineSegment(sketch, "E1416", {"start": v(-13.26, 45.27) * mm, "end": v(-13.19, 45.42) * mm});
            skLineSegment(sketch, "E1417", {"start": v(-13.19, 45.42) * mm, "end": v(-13.18, 45.45) * mm});
            skLineSegment(sketch, "E1418", {"start": v(-13.18, 45.45) * mm, "end": v(-13.15, 45.55) * mm});
            skLineSegment(sketch, "E1419", {"start": v(-13.15, 45.55) * mm, "end": v(-13.1, 45.65) * mm});
            skLineSegment(sketch, "E1420", {"start": v(-13.1, 45.65) * mm, "end": v(-13.1, 45.67) * mm});
            skLineSegment(sketch, "E1421", {"start": v(-13.1, 45.67) * mm, "end": v(-13.05, 45.77) * mm});
            skLineSegment(sketch, "E1422", {"start": v(-13.05, 45.77) * mm, "end": v(-12.86, 46.02) * mm});
            skLineSegment(sketch, "E1423", {"start": v(-12.86, 46.02) * mm, "end": v(-12.56, 46.25) * mm});
            skLineSegment(sketch, "E1424", {"start": v(-12.56, 46.25) * mm, "end": v(-12.2, 46.4) * mm});
            skLineSegment(sketch, "E1425", {"start": v(-12.2, 46.4) * mm, "end": v(-11.88, 46.48) * mm});
            skLineSegment(sketch, "E1426", {"start": v(-11.88, 46.48) * mm, "end": v(-11.77, 46.5) * mm});
            skLineSegment(sketch, "E1427", {"start": v(-11.77, 46.5) * mm, "end": v(-11.73, 46.51) * mm});
            skLineSegment(sketch, "E1428", {"start": v(-11.73, 46.51) * mm, "end": v(-11.6, 46.52) * mm});
            skLineSegment(sketch, "E1429", {"start": v(-11.6, 46.52) * mm, "end": v(-11.41, 46.53) * mm});
            skLineSegment(sketch, "E1430", {"start": v(-11.41, 46.53) * mm, "end": v(-11.27, 46.53) * mm});
            skLineSegment(sketch, "E1431", {"start": v(-11.27, 46.53) * mm, "end": v(-11.22, 46.53) * mm});
            skLineSegment(sketch, "E1432", {"start": v(-11.22, 46.53) * mm, "end": v(-7, 46.53) * mm});
            skLineSegment(sketch, "E1433", {"start": v(-7, 46.53) * mm, "end": v(-5.79, 49.22) * mm});
            skLineSegment(sketch, "E1434", {"start": v(-5.79, 49.22) * mm, "end": v(-6, 49.22) * mm});
            skLineSegment(sketch, "E1435", {"start": v(-6, 49.22) * mm, "end": v(-6.67, 49.23) * mm});
            skLineSegment(sketch, "E1436", {"start": v(-6.67, 49.23) * mm, "end": v(-7.43, 49.23) * mm});
            skLineSegment(sketch, "E1437", {"start": v(-7.43, 49.23) * mm, "end": v(-8.1, 49.23) * mm});
            skLineSegment(sketch, "E1438", {"start": v(-8.1, 49.23) * mm, "end": v(-8.71, 49.23) * mm});
            skLineSegment(sketch, "E1439", {"start": v(-8.71, 49.23) * mm, "end": v(-9.27, 49.23) * mm});
            skLineSegment(sketch, "E1440", {"start": v(-9.27, 49.23) * mm, "end": v(-9.82, 49.23) * mm});
            skLineSegment(sketch, "E1441", {"start": v(-9.82, 49.23) * mm, "end": v(-10.38, 49.23) * mm});
            skLineSegment(sketch, "E1442", {"start": v(-10.38, 49.23) * mm, "end": v(-10.82, 49.22) * mm});
            skLineSegment(sketch, "E1443", {"start": v(-10.82, 49.22) * mm, "end": v(-10.97, 49.22) * mm});
            skLineSegment(sketch, "E1444", {"start": v(-10.97, 49.22) * mm, "end": v(-11.13, 49.22) * mm});
            skLineSegment(sketch, "E1445", {"start": v(-11.13, 49.22) * mm, "end": v(-11.62, 49.2) * mm});
            skLineSegment(sketch, "E1446", {"start": v(-11.62, 49.2) * mm, "end": v(-12.25, 49.1) * mm});
            skLineSegment(sketch, "E1447", {"start": v(-12.25, 49.1) * mm, "end": v(-12.87, 48.96) * mm});
            skLineSegment(sketch, "E1448", {"start": v(-12.87, 48.96) * mm, "end": v(-13.45, 48.73) * mm});
            skLineSegment(sketch, "E1449", {"start": v(-13.45, 48.73) * mm, "end": v(-14, 48.42) * mm});
            skLineSegment(sketch, "E1450", {"start": v(-14, 48.42) * mm, "end": v(-14.5, 48) * mm});
            skLineSegment(sketch, "E1451", {"start": v(-14.5, 48) * mm, "end": v(-14.96, 47.46) * mm});
            skLineSegment(sketch, "E1452", {"start": v(-14.96, 47.46) * mm, "end": v(-15.27, 46.97) * mm});
            skLineSegment(sketch, "E1453", {"start": v(-15.27, 46.97) * mm, "end": v(-15.35, 46.8) * mm});
            skLineSegment(sketch, "E1454", {"start": v(-15.35, 46.8) * mm, "end": v(-15.4, 46.7) * mm});
            skLineSegment(sketch, "E1455", {"start": v(-15.4, 46.7) * mm, "end": v(-15.54, 46.4) * mm});
            skLineSegment(sketch, "E1456", {"start": v(-15.54, 46.4) * mm, "end": v(-15.74, 45.97) * mm});
            skLineSegment(sketch, "E1457", {"start": v(-15.74, 45.97) * mm, "end": v(-15.95, 45.5) * mm});
            skLineSegment(sketch, "E1458", {"start": v(-15.95, 45.5) * mm, "end": v(-16.18, 45) * mm});
            skLineSegment(sketch, "E1459", {"start": v(-16.18, 45) * mm, "end": v(-16.4, 44.48) * mm});
            skLineSegment(sketch, "E1460", {"start": v(-16.4, 44.48) * mm, "end": v(-16.62, 43.96) * mm});
            skLineSegment(sketch, "E1461", {"start": v(-16.62, 43.96) * mm, "end": v(-16.84, 43.44) * mm});
            skLineSegment(sketch, "E1462", {"start": v(-16.84, 43.44) * mm, "end": v(-17.06, 42.93) * mm});
            skLineSegment(sketch, "E1463", {"start": v(-17.06, 42.93) * mm, "end": v(-17.26, 42.45) * mm});
            skLineSegment(sketch, "E1464", {"start": v(-17.26, 42.45) * mm, "end": v(-17.45, 42) * mm});
            skLineSegment(sketch, "E1465", {"start": v(-17.45, 42) * mm, "end": v(-17.61, 41.59) * mm});
            skLineSegment(sketch, "E1466", {"start": v(-17.61, 41.59) * mm, "end": v(-17.76, 41.23) * mm});
            skLineSegment(sketch, "E1467", {"start": v(-17.76, 41.23) * mm, "end": v(-17.88, 40.93) * mm});
            skLineSegment(sketch, "E1468", {"start": v(-17.88, 40.93) * mm, "end": v(-17.97, 40.71) * mm});
            skLineSegment(sketch, "E1469", {"start": v(-17.97, 40.71) * mm, "end": v(-18.03, 40.57) * mm});
            skLineSegment(sketch, "E1470", {"start": v(-18.03, 40.57) * mm, "end": v(-18.05, 40.52) * mm});
            skLineSegment(sketch, "E1471", {"start": v(-18.05, 40.52) * mm, "end": v(-18.06, 40.48) * mm});
            skLineSegment(sketch, "E1472", {"start": v(-18.06, 40.48) * mm, "end": v(-18.1, 40.36) * mm});
            skLineSegment(sketch, "E1473", {"start": v(-18.1, 40.36) * mm, "end": v(-18.14, 40.19) * mm});
            skLineSegment(sketch, "E1474", {"start": v(-18.14, 40.19) * mm, "end": v(-18.18, 39.98) * mm});
            skLineSegment(sketch, "E1475", {"start": v(-18.18, 39.98) * mm, "end": v(-18.23, 39.75) * mm});
            skLineSegment(sketch, "E1476", {"start": v(-18.23, 39.75) * mm, "end": v(-18.27, 39.53) * mm});
            skLineSegment(sketch, "E1477", {"start": v(-18.27, 39.53) * mm, "end": v(-18.3, 39.32) * mm});
            skLineSegment(sketch, "E1478", {"start": v(-18.3, 39.32) * mm, "end": v(-18.3, 39.2) * mm});
            skLineSegment(sketch, "E1479", {"start": v(-18.3, 39.2) * mm, "end": v(-18.3, 39.15) * mm});
            skLineSegment(sketch, "E1480", {"start": v(-18.3, 39.15) * mm, "end": v(-18.29, 39.08) * mm});
            skLineSegment(sketch, "E1481", {"start": v(-18.29, 39.08) * mm, "end": v(-18.25, 38.85) * mm});
            skLineSegment(sketch, "E1482", {"start": v(-18.25, 38.85) * mm, "end": v(-18.15, 38.5) * mm});
            skLineSegment(sketch, "E1483", {"start": v(-18.15, 38.5) * mm, "end": v(-18, 38.15) * mm});
            skLineSegment(sketch, "E1484", {"start": v(-18, 38.15) * mm, "end": v(-17.75, 37.8) * mm});
            skLineSegment(sketch, "E1485", {"start": v(-17.75, 37.8) * mm, "end": v(-17.41, 37.48) * mm});
            skLineSegment(sketch, "E1486", {"start": v(-17.41, 37.48) * mm, "end": v(-16.96, 37.23) * mm});
            skLineSegment(sketch, "E1487", {"start": v(-16.96, 37.23) * mm, "end": v(-16.4, 37.05) * mm});
            skLineSegment(sketch, "E1488", {"start": v(-16.4, 37.05) * mm, "end": v(-15.85, 37) * mm});
            skLineSegment(sketch, "E1489", {"start": v(-15.85, 37) * mm, "end": v(-15.67, 37) * mm});
            skLineSegment(sketch, "E1490", {"start": v(-15.67, 37) * mm, "end": v(-15.54, 37) * mm});
            skLineSegment(sketch, "E1491", {"start": v(-15.54, 37) * mm, "end": v(-15.13, 37) * mm});
            skLineSegment(sketch, "E1492", {"start": v(-15.13, 37) * mm, "end": v(-14.45, 36.99) * mm});
            skLineSegment(sketch, "E1493", {"start": v(-14.45, 36.99) * mm, "end": v(-13.67, 36.99) * mm});
            skLineSegment(sketch, "E1494", {"start": v(-13.67, 36.99) * mm, "end": v(-12.79, 36.98) * mm});
            skLineSegment(sketch, "E1495", {"start": v(-12.79, 36.98) * mm, "end": v(-11.83, 36.98) * mm});
            skLineSegment(sketch, "E1496", {"start": v(-11.83, 36.98) * mm, "end": v(-10.8, 36.98) * mm});
            skLineSegment(sketch, "E1497", {"start": v(-10.8, 36.98) * mm, "end": v(-9.72, 36.98) * mm});
            skLineSegment(sketch, "E1498", {"start": v(-9.72, 36.98) * mm, "end": v(-8.9, 36.99) * mm});
            skLineSegment(sketch, "E1499", {"start": v(-8.9, 36.99) * mm, "end": v(-8.62, 36.99) * mm});
            skLineSegment(sketch, "E1500", {"start": v(-8.62, 36.99) * mm, "end": v(-8.58, 37) * mm});
            skLineSegment(sketch, "E1501", {"start": v(-8.58, 37) * mm, "end": v(-8.49, 37.01) * mm});
            skLineSegment(sketch, "E1502", {"start": v(-8.49, 37.01) * mm, "end": v(-8.34, 37.05) * mm});
            skLineSegment(sketch, "E1503", {"start": v(-8.34, 37.05) * mm, "end": v(-8.17, 37.11) * mm});
            skLineSegment(sketch, "E1504", {"start": v(-8.17, 37.11) * mm, "end": v(-7.97, 37.2) * mm});
            skLineSegment(sketch, "E1505", {"start": v(-7.97, 37.2) * mm, "end": v(-7.77, 37.32) * mm});
            skLineSegment(sketch, "E1506", {"start": v(-7.77, 37.32) * mm, "end": v(-7.58, 37.47) * mm});
            skLineSegment(sketch, "E1507", {"start": v(-7.58, 37.47) * mm, "end": v(-7.45, 37.62) * mm});
            skLineSegment(sketch, "E1508", {"start": v(-7.45, 37.62) * mm, "end": v(-7.41, 37.67) * mm});
            skLineSegment(sketch, "E1509", {"start": v(-7.41, 37.67) * mm, "end": v(-7.34, 37.76) * mm});
            skLineSegment(sketch, "E1510", {"start": v(-7.34, 37.76) * mm, "end": v(-7.14, 38.05) * mm});
            skLineSegment(sketch, "E1511", {"start": v(-7.14, 38.05) * mm, "end": v(-6.93, 38.34) * mm});
            skLineSegment(sketch, "E1512", {"start": v(-6.93, 38.34) * mm, "end": v(-6.8, 38.53) * mm});
            skLineSegment(sketch, "E1513", {"start": v(-6.8, 38.53) * mm, "end": v(-6.76, 38.6) * mm});
            skLineSegment(sketch, "E1514", {"start": v(-6.76, 38.6) * mm, "end": v(-6.75, 38.56) * mm});
            skLineSegment(sketch, "E1515", {"start": v(-6.75, 38.56) * mm, "end": v(-6.71, 38.47) * mm});
            skLineSegment(sketch, "E1516", {"start": v(-6.71, 38.47) * mm, "end": v(-6.65, 38.34) * mm});
            skLineSegment(sketch, "E1517", {"start": v(-6.65, 38.34) * mm, "end": v(-6.55, 38.18) * mm});
            skLineSegment(sketch, "E1518", {"start": v(-6.55, 38.18) * mm, "end": v(-6.42, 38) * mm});
            skLineSegment(sketch, "E1519", {"start": v(-6.42, 38) * mm, "end": v(-6.26, 37.8) * mm});
            skLineSegment(sketch, "E1520", {"start": v(-6.26, 37.8) * mm, "end": v(-6.06, 37.62) * mm});
            skLineSegment(sketch, "E1521", {"start": v(-6.06, 37.62) * mm, "end": v(-5.89, 37.5) * mm});
            skLineSegment(sketch, "E1522", {"start": v(-5.89, 37.5) * mm, "end": v(-5.82, 37.46) * mm});
            skLineSegment(sketch, "E1523", {"start": v(-5.82, 37.46) * mm, "end": v(-5.72, 37.4) * mm});
            skLineSegment(sketch, "E1524", {"start": v(-5.72, 37.4) * mm, "end": v(-5.38, 37.21) * mm});
            skLineSegment(sketch, "E1525", {"start": v(-5.38, 37.21) * mm, "end": v(-5.03, 37.07) * mm});
            skLineSegment(sketch, "E1526", {"start": v(-5.03, 37.07) * mm, "end": v(-4.7, 37) * mm});
            skLineSegment(sketch, "E1527", {"start": v(-4.7, 37) * mm, "end": v(-4.44, 36.99) * mm});
            skLineSegment(sketch, "E1528", {"start": v(-4.44, 36.99) * mm, "end": v(-4.35, 36.99) * mm});
            skLineSegment(sketch, "E1529", {"start": v(-4.35, 36.99) * mm, "end": v(-3.8, 36.95) * mm});
            skLineSegment(sketch, "E1530", {"start": v(-3.8, 36.95) * mm, "end": v(-3.7, 36.95) * mm});
            skLineSegment(sketch, "E1531", {"start": v(-3.7, 36.95) * mm, "end": v(-3.37, 36.95) * mm});
            skLineSegment(sketch, "E1532", {"start": v(-3.37, 36.95) * mm, "end": v(-2.93, 36.95) * mm});
            skLineSegment(sketch, "E1533", {"start": v(-2.93, 36.95) * mm, "end": v(-2.48, 36.94) * mm});
            skLineSegment(sketch, "E1534", {"start": v(-2.48, 36.94) * mm, "end": v(-2.07, 36.94) * mm});
            skLineSegment(sketch, "E1535", {"start": v(-2.07, 36.94) * mm, "end": v(-1.7, 36.95) * mm});
            skLineSegment(sketch, "E1536", {"start": v(-1.7, 36.95) * mm, "end": v(-1.41, 36.95) * mm});
            skLineSegment(sketch, "E1537", {"start": v(-1.41, 36.95) * mm, "end": v(-1.22, 36.95) * mm});
            skLineSegment(sketch, "E1538", {"start": v(-1.22, 36.95) * mm, "end": v(-1.15, 36.95) * mm});
            skLineSegment(sketch, "E1539", {"start": v(-1.15, 36.95) * mm, "end": v(4.07, 49.2) * mm});
            skLineSegment(sketch, "E1540", {"start": v(4.07, 49.2) * mm, "end": v(1.14, 49.18) * mm});
            skLineSegment(sketch, "E1541", {"start": v(1.14, 49.18) * mm, "end": v(-3.05, 39.5) * mm});
            skLineSegment(sketch, "E1542", {"start": v(-3.05, 39.5) * mm, "end": v(-3.6, 39.48) * mm});
            skSolve(sketch);
        }
        {
            var Q0;
            Q0 = qSketchRegion(id + "F20", true);
            extrude(context, id + "F21", {"entities" : qUnion([Q0]), "operationType" : NewBodyOperationType.REMOVE, "oppositeDirection" : true, "depth" : 1.52 * mm, "offsetDistance" : 25.4 * mm});
        }
    });
